FCSTD DOCUMENT  (FreeCAD 1.0R39319 (Git))
Label: Robot 2026 Aichi
License: All rights reserved
LicenseURL: https://en.wikipedia.org/wiki/All_rights_reserved
objects: Part::Feature×493, Part::Box×130, Part::Cylinder×120, Part::MultiFuse×91, Part::Cut×91, App::Part×63, Part::Fillet×11, Part::Chamfer×9, Part::FeaturePython×6, Part::Fuse×2, Part::Part2DObjectPython×2, Part::Extrusion×2, Part::MultiCommon×1, App::FeaturePython×1
note: 958 computed .brp shape members not serialized (recipe doc carries the construction recipe); baked Part::Feature solids carry a one-line shape summary decoded from their .brp

FEATURE [Part::Feature] Part__Feature  label="Tyre Axle LB"
  Placement = pos=(-4,-10,0) rot=(0,0,1;0rad)
  shape: bbox 40.5 x 10 x 10 mm, 8 faces (baked)
FEATURE [Part::Feature] Part__Feature001  label="Bearing LB"
  Placement = pos=(143,0,0) rot=(0,0,1;0rad)
  shape: bbox 4 x 15.6 x 15.6 mm, 6 faces (baked)
FEATURE [Part::Feature] Part__Feature002  label="Gear Axle LB"
  Placement = pos=(-4,-10,0) rot=(0,0,1;0rad)
  shape: bbox 21 x 30 x 30 mm, 121 faces (baked)
FEATURE [Part::Feature] Part__Feature003  label="Gear Motor LB"
  shape: bbox 4 x 26.99 x 26.94 mm, 202 faces (baked)
FEATURE [Part::Feature] Part__Feature004  label="Wheel LB"
  Placement = pos=(42.6,52,10) rot=(0,1,0;1.5708rad)
  shape: bbox 17 x 61.05 x 60.97 mm, 273 faces (baked)
FEATURE [Part::Feature] Part__Feature005  label="Silicon Tires LB"
  Placement = pos=(42.6,53,10) rot=(0,1,0;1.5708rad)
  shape: bbox 15 x 67.95 x 67.92 mm, 56 faces (baked)
FEATURE [App::Part] robot___robcup_ber_5__a  label="Drivetrain LB"
  Group = -> [Part__Feature,Part__Feature001,Part__Feature002,Part__Feature003,Part__Feature004,Part__Feature005]
  Origin = -> Origin
FEATURE [Part::Feature] Part__Feature006  label="Gear Motor LF"
  Placement = pos=(0,-74,0) rot=(0,0,1;0rad)
  shape: bbox 4 x 26.99 x 26.94 mm, 202 faces (baked)
FEATURE [Part::Feature] Part__Feature007  label="Tyre Axle LF001"
  Placement = pos=(-4,10,0) rot=(0,0,1;0rad)
  shape: bbox 40.5 x 10 x 10 mm, 8 faces (baked)
FEATURE [Part::Feature] Part__Feature008  label="Bearing LF"
  Placement = pos=(143,-124,0) rot=(0,0,1;0rad)
  shape: bbox 4 x 15.6 x 15.6 mm, 6 faces (baked)
FEATURE [Part::Feature] Part__Feature009  label="Gear Axle LF"
  Placement = pos=(-4,10,0) rot=(0,0,1;0rad)
  shape: bbox 21 x 30 x 30 mm, 121 faces (baked)
FEATURE [Part::Feature] Part__Feature010  label="Wheel LF"
  Placement = pos=(42.6,-72,10) rot=(0,1,0;1.5708rad)
  shape: bbox 17 x 61.05 x 60.97 mm, 273 faces (baked)
FEATURE [Part::Feature] Part__Feature011  label="Silicon Tires LF"
  Placement = pos=(42.6,-71,10) rot=(0,1,0;1.5708rad)
  shape: bbox 15 x 67.95 x 67.92 mm, 56 faces (baked)
FEATURE [App::Part] robot___robcup_ber_5__a001  label="Drivetrain LF"
  Group = -> [Part__Feature006,Part__Feature007,Part__Feature008,Part__Feature009,Part__Feature010,Part__Feature011]
  Origin = -> Origin001
FEATURE [Part::Feature] Part__Feature012  label="Tyre Axle RB"
  Placement = pos=(4,-10,0) rot=(0,0,1;0rad)
  shape: bbox 40.5 x 10 x 10 mm, 8 faces (baked)
FEATURE [Part::Feature] Part__Feature013  label="Gear Motor RB"
  Placement = pos=(-143,0,0) rot=(0,0,1;0rad)
  shape: bbox 4 x 26.99 x 26.94 mm, 202 faces (baked)
FEATURE [Part::Feature] Part__Feature014  label="Bearing RB"
  shape: bbox 4 x 15.6 x 15.6 mm, 6 faces (baked)
FEATURE [Part::Feature] Part__Feature015  label="Gear Axle RB"
  Placement = pos=(4,-10,0) rot=(0,0,1;0rad)
  shape: bbox 21 x 30 x 30 mm, 121 faces (baked)
FEATURE [Part::Feature] Part__Feature016  label="Wheel RB"
  Placement = pos=(-127.4,52,10) rot=(0,1,0;1.5708rad)
  shape: bbox 17 x 61.05 x 60.97 mm, 273 faces (baked)
FEATURE [Part::Feature] Part__Feature017  label="Silicon Tires RB"
  Placement = pos=(-127.4,53,10) rot=(0,1,0;1.5708rad)
  shape: bbox 15 x 67.95 x 67.92 mm, 56 faces (baked)
FEATURE [App::Part] robot___robcup_ber_5__a002  label="Drivetrain RB"
  Group = -> [Part__Feature012,Part__Feature013,Part__Feature014,Part__Feature015,Part__Feature016,Part__Feature017]
  Origin = -> Origin002
FEATURE [Part::Feature] Part__Feature018  label="Gear Motor RF"
  Placement = pos=(-143,-74,0) rot=(0,0,1;0rad)
  shape: bbox 4 x 26.99 x 26.94 mm, 202 faces (baked)
FEATURE [Part::Feature] Part__Feature019  label="Gear Axle RF"
  Placement = pos=(4,10,0) rot=(0,0,1;0rad)
  shape: bbox 21 x 30 x 30 mm, 121 faces (baked)
FEATURE [Part::Feature] Part__Feature020  label="Bearing RF"
  Placement = pos=(0,-124,0) rot=(0,0,1;0rad)
  shape: bbox 4 x 15.6 x 15.6 mm, 6 faces (baked)
FEATURE [Part::Feature] Part__Feature021  label="Tyre Axle RF"
  Placement = pos=(4,10,0) rot=(0,0,1;0rad)
  shape: bbox 40.5 x 10 x 10 mm, 8 faces (baked)
FEATURE [Part::Feature] Part__Feature022  label="Wheel RF"
  Placement = pos=(-127.4,-72,10) rot=(0,1,0;1.5708rad)
  shape: bbox 17 x 61.05 x 60.97 mm, 273 faces (baked)
FEATURE [Part::Feature] Part__Feature023  label="Silicon Tires RF"
  Placement = pos=(-127.4,-71,10) rot=(0,1,0;1.5708rad)
  shape: bbox 15 x 67.95 x 67.92 mm, 56 faces (baked)
FEATURE [App::Part] robot___robcup_ber_5__a003  label="Drivetrain RF"
  Group = -> [Part__Feature018,Part__Feature019,Part__Feature020,Part__Feature021,Part__Feature022,Part__Feature023]
  Origin = -> Origin003
FEATURE [Part::Box] Box069  label="立方体048"
  AttacherType = Attacher::AttachEngine3D
  Height = 20.1
  Length = 38.8
  Placement = pos=(82,-93,0) rot=(0,0,1;0rad)
  Width = 40.1
FEATURE [Part::Box] Box084  label="立方体063"
  AttacherType = Attacher::AttachEngine3D
  Height = 20.1
  Length = 2.7
  Placement = pos=(90.8,-99.95,0) rot=(0,0,1;0rad)
  Width = 54
FEATURE [Part::FeaturePython] CycloidGear025  # WARN: FeaturePython — macro-defined, semantics opaque (R4)
  AttacherType = Attacher::AttachEngine3D
  Placement = pos=(-107.4,-47,10) rot=(0,1,0;1.5708rad)
  angular_backlash = 0
  backlash = 0
  clearance = 0.25
  double_helix = false
  head = 0
  head_fillet = 0
  height = 6
  helix_angle = 0
  inner_diameter = 12.5
  module = 0.24
  num_teeth = 25
  numpoints = 20
  outer_diameter = 7.5
  pitch_diameter = 6
  root_fillet = 0
  version = 1.3.0
  expr: angular_backlash = backlash / pitch_diameter * 360 ° / pi
  expr: inner_diameter = num_teeth / 2
  expr: pitch_diameter = num_teeth * module
FEATURE [Part::Cylinder] Cylinder175  label="円柱175"
  Angle = 360
  AttacherType = Attacher::AttachEngine3D
  FirstAngle = 0
  Height = 20
  Placement = pos=(-97.2,-22.1,5) rot=(0,1,0;1.5708rad)
  Radius = 2
  SecondAngle = 0
FEATURE [Part::Cylinder] Cylinder176  label="円柱176"
  Angle = 360
  AttacherType = Attacher::AttachEngine3D
  FirstAngle = 0
  Height = 20
  Placement = pos=(-97.2,-22.1,15) rot=(0,1,0;1.5708rad)
  Radius = 2
  SecondAngle = 0
FEATURE [Part::Cylinder] Cylinder177  label="円柱177"
  Angle = 360
  AttacherType = Attacher::AttachEngine3D
  FirstAngle = 0
  Height = 20
  Placement = pos=(-97.2,-71.8,15) rot=(0,1,0;1.5708rad)
  Radius = 2
  SecondAngle = 0
FEATURE [Part::Cylinder] Cylinder178  label="円柱178"
  Angle = 360
  AttacherType = Attacher::AttachEngine3D
  FirstAngle = 0
  Height = 20
  Placement = pos=(-97.2,-71.8,5) rot=(0,1,0;1.5708rad)
  Radius = 2
  SecondAngle = 0
FEATURE [Part::MultiFuse] Fusion084
  Placement = pos=(-188,26,0) rot=(0,0,1;0rad)
  Shapes = -> [Box084,Box069]
FEATURE [Part::Cut] Cut128
  Base = -> Fusion084
  Tool = -> Cylinder176
FEATURE [Part::Cut] Cut129
  Base = -> Cut128
  Tool = -> Cylinder175
FEATURE [Part::Cut] Cut130
  Base = -> Cut129
  Tool = -> Cylinder177
FEATURE [Part::Cut] Cut131
  Base = -> Cut130
  Placement = pos=(4,10,0) rot=(0,0,1;0rad)
  Tool = -> Cylinder178
FEATURE [Part::MultiFuse] Fusion344  label="Motor RF"
  Refine = true
  Shapes = -> [Cut131,CycloidGear025]
FEATURE [Part::Box] Box075  label="立方体054"
  AttacherType = Attacher::AttachEngine3D
  Height = 20.1
  Length = 38.8
  Placement = pos=(82,-93,0) rot=(0,0,1;0rad)
  Width = 40.1
FEATURE [Part::Box] Box223  label="立方体201"
  AttacherType = Attacher::AttachEngine3D
  Height = 20.1
  Length = 2.7
  Placement = pos=(90.8,-99.95,0) rot=(0,0,1;0rad)
  Width = 54
FEATURE [Part::FeaturePython] CycloidGear019  # WARN: FeaturePython — macro-defined, semantics opaque (R4)
  AttacherType = Attacher::AttachEngine3D
  Placement = pos=(-107.4,27,10) rot=(0,1,0;1.5708rad)
  angular_backlash = 0
  backlash = 0
  clearance = 0.25
  double_helix = false
  head = 0
  head_fillet = 0
  height = 6
  helix_angle = 0
  inner_diameter = 12.5
  module = 0.24
  num_teeth = 25
  numpoints = 20
  outer_diameter = 7.5
  pitch_diameter = 6
  root_fillet = 0
  version = 1.3.0
  expr: angular_backlash = backlash / pitch_diameter * 360 ° / pi
  expr: inner_diameter = num_teeth / 2
  expr: pitch_diameter = num_teeth * module
FEATURE [Part::Cylinder] Cylinder171  label="円柱171"
  Angle = 360
  AttacherType = Attacher::AttachEngine3D
  FirstAngle = 0
  Height = 20
  Placement = pos=(-97.2,51.9,5) rot=(0,1,0;1.5708rad)
  Radius = 2
  SecondAngle = 0
FEATURE [Part::Cylinder] Cylinder172  label="円柱172"
  Angle = 360
  AttacherType = Attacher::AttachEngine3D
  FirstAngle = 0
  Height = 20
  Placement = pos=(-97.2,51.9,15) rot=(0,1,0;1.5708rad)
  Radius = 2
  SecondAngle = 0
FEATURE [Part::Cylinder] Cylinder173  label="円柱173"
  Angle = 360
  AttacherType = Attacher::AttachEngine3D
  FirstAngle = 0
  Height = 20
  Placement = pos=(-97.2,2.2,15) rot=(0,1,0;1.5708rad)
  Radius = 2
  SecondAngle = 0
FEATURE [Part::Cylinder] Cylinder174  label="円柱174"
  Angle = 360
  AttacherType = Attacher::AttachEngine3D
  FirstAngle = 0
  Height = 20
  Placement = pos=(-97.2,2.2,5) rot=(0,1,0;1.5708rad)
  Radius = 2
  SecondAngle = 0
FEATURE [Part::MultiFuse] Fusion085
  Placement = pos=(-188,100,0) rot=(0,0,1;0rad)
  Shapes = -> [Box223,Box075]
FEATURE [Part::Cut] Cut124
  Base = -> Fusion085
  Tool = -> Cylinder172
FEATURE [Part::Cut] Cut125
  Base = -> Cut124
  Tool = -> Cylinder171
FEATURE [Part::Cut] Cut126
  Base = -> Cut125
  Tool = -> Cylinder173
FEATURE [Part::Cut] Cut127
  Base = -> Cut126
  Placement = pos=(4,-10,0) rot=(0,0,1;0rad)
  Tool = -> Cylinder174
FEATURE [Part::MultiFuse] Fusion345  label="Motor RB"
  Refine = true
  Shapes = -> [CycloidGear019,Cut127]
FEATURE [Part::Box] Box225  label="立方体203"
  AttacherType = Attacher::AttachEngine3D
  Height = 20.1
  Length = 2.7
  Placement = pos=(109.3,-99.95,0) rot=(0,0,1;0rad)
  Width = 54
FEATURE [Part::Box] Box226  label="立方体204"
  AttacherType = Attacher::AttachEngine3D
  Height = 20.1
  Length = 38.8
  Placement = pos=(82,-93,0) rot=(0,0,1;0rad)
  Width = 40.1
FEATURE [Part::FeaturePython] CycloidGear022  # WARN: FeaturePython — macro-defined, semantics opaque (R4)
  AttacherType = Attacher::AttachEngine3D
  Placement = pos=(33.6,-47,10) rot=(0,1,0;1.5708rad)
  angular_backlash = 0
  backlash = 0
  clearance = 0.25
  double_helix = false
  head = 0
  head_fillet = 0
  height = 6
  helix_angle = 0
  inner_diameter = 12.5
  module = 0.24
  num_teeth = 25
  numpoints = 20
  outer_diameter = 7.5
  pitch_diameter = 6
  root_fillet = 0
  version = 1.3.0
  expr: angular_backlash = backlash / pitch_diameter * 360 ° / pi
  expr: inner_diameter = num_teeth / 2
  expr: pitch_diameter = num_teeth * module
FEATURE [Part::Cylinder] Cylinder167  label="円柱167"
  Angle = 360
  AttacherType = Attacher::AttachEngine3D
  FirstAngle = 0
  Height = 20
  Placement = pos=(9.4,-22.1,5) rot=(0,1,0;1.5708rad)
  Radius = 2
  SecondAngle = 0
FEATURE [Part::Cylinder] Cylinder168  label="円柱168"
  Angle = 360
  AttacherType = Attacher::AttachEngine3D
  FirstAngle = 0
  Height = 20
  Placement = pos=(9.4,-22.1,15) rot=(0,1,0;1.5708rad)
  Radius = 2
  SecondAngle = 0
FEATURE [Part::Cylinder] Cylinder169  label="円柱169"
  Angle = 360
  AttacherType = Attacher::AttachEngine3D
  FirstAngle = 0
  Height = 20
  Placement = pos=(9.4,-71.8,15) rot=(0,1,0;1.5708rad)
  Radius = 2
  SecondAngle = 0
FEATURE [Part::Cylinder] Cylinder170  label="円柱170"
  Angle = 360
  AttacherType = Attacher::AttachEngine3D
  FirstAngle = 0
  Height = 20
  Placement = pos=(9.4,-71.8,5) rot=(0,1,0;1.5708rad)
  Radius = 2
  SecondAngle = 0
FEATURE [Part::MultiFuse] Fusion086
  Placement = pos=(-82.6,26,0) rot=(0,0,1;0rad)
  Shapes = -> [Box226,Box225]
FEATURE [Part::Cut] Cut120
  Base = -> Fusion086
  Tool = -> Cylinder168
FEATURE [Part::Cut] Cut121
  Base = -> Cut120
  Tool = -> Cylinder167
FEATURE [Part::Cut] Cut122
  Base = -> Cut121
  Tool = -> Cylinder169
FEATURE [Part::Cut] Cut123
  Base = -> Cut122
  Placement = pos=(-4,10,0) rot=(0,0,1;0rad)
  Tool = -> Cylinder170
FEATURE [Part::MultiFuse] Fusion347  label="Motor LF"
  Refine = true
  Shapes = -> [Cut123,CycloidGear022]
FEATURE [Part::Box] Box076  label="立方体055"
  AttacherType = Attacher::AttachEngine3D
  Height = 20.1
  Length = 2.7
  Placement = pos=(109.3,-99.95,0) rot=(0,0,1;0rad)
  Width = 54
FEATURE [Part::Box] Box227  label="立方体205"
  AttacherType = Attacher::AttachEngine3D
  Height = 20.1
  Length = 38.8
  Placement = pos=(82,-93,0) rot=(0,0,1;0rad)
  Width = 40.1
FEATURE [Part::FeaturePython] CycloidGear017  # WARN: FeaturePython — macro-defined, semantics opaque (R4)
  AttacherType = Attacher::AttachEngine3D
  Placement = pos=(33.6,27,10) rot=(0,1,0;1.5708rad)
  angular_backlash = 0
  backlash = 0
  clearance = 0.25
  double_helix = false
  head = 0
  head_fillet = 0
  height = 6
  helix_angle = 0
  inner_diameter = 12.5
  module = 0.24
  num_teeth = 25
  numpoints = 20
  outer_diameter = 7.5
  pitch_diameter = 6
  root_fillet = 0
  version = 1.3.0
  expr: angular_backlash = backlash / pitch_diameter * 360 ° / pi
  expr: inner_diameter = num_teeth / 2
  expr: pitch_diameter = num_teeth * module
FEATURE [Part::Cylinder] Cylinder163  label="円柱163"
  Angle = 360
  AttacherType = Attacher::AttachEngine3D
  FirstAngle = 0
  Height = 20
  Placement = pos=(9.4,51.9,5) rot=(0,1,0;1.5708rad)
  Radius = 2
  SecondAngle = 0
FEATURE [Part::Cylinder] Cylinder164  label="円柱164"
  Angle = 360
  AttacherType = Attacher::AttachEngine3D
  FirstAngle = 0
  Height = 20
  Placement = pos=(9.4,51.9,15) rot=(0,1,0;1.5708rad)
  Radius = 2
  SecondAngle = 0
FEATURE [Part::Cylinder] Cylinder165  label="円柱165"
  Angle = 360
  AttacherType = Attacher::AttachEngine3D
  FirstAngle = 0
  Height = 20
  Placement = pos=(9.4,2.2,15) rot=(0,1,0;1.5708rad)
  Radius = 2
  SecondAngle = 0
FEATURE [Part::Cylinder] Cylinder166  label="円柱166"
  Angle = 360
  AttacherType = Attacher::AttachEngine3D
  FirstAngle = 0
  Height = 20
  Placement = pos=(9.4,2.2,5) rot=(0,1,0;1.5708rad)
  Radius = 2
  SecondAngle = 0
FEATURE [Part::MultiFuse] Fusion087
  Placement = pos=(-82.6,100,0) rot=(0,0,1;0rad)
  Shapes = -> [Box076,Box227]
FEATURE [Part::Cut] Cut116
  Base = -> Fusion087
  Tool = -> Cylinder164
FEATURE [Part::Cut] Cut117
  Base = -> Cut116
  Tool = -> Cylinder163
FEATURE [Part::Cut] Cut118
  Base = -> Cut117
  Tool = -> Cylinder165
FEATURE [Part::Cut] Cut119
  Base = -> Cut118
  Placement = pos=(-4,-10,0) rot=(0,0,1;0rad)
  Tool = -> Cylinder166
FEATURE [Part::MultiFuse] Fusion346  label="Motor LB"
  Refine = true
  Shapes = -> [CycloidGear017,Cut119]
FEATURE [Part::Box] Box016  label="機体底面"
  AttacherType = Attacher::AttachEngine3D
  Height = 5
  Length = 136.2
  Placement = pos=(-102,-108,-5) rot=(0,0,1;0rad)
  Width = 184
FEATURE [Part::Box] Box027  label="立方体007"
  AttacherType = Attacher::AttachEngine3D
  Height = 20.4
  Length = 45.2
  Placement = pos=(-48.6,-98,10) rot=(0,0,1;0rad)
  Width = 5
FEATURE [Part::Box] Box102  label="立方体081"
  AttacherType = Attacher::AttachEngine3D
  Height = 5
  Length = 60
  Placement = pos=(-63.9,-96,-5) rot=(0,0,1;0rad)
  Width = 64
FEATURE [Part::Box] Box213  label="立方体191"
  AttacherType = Attacher::AttachEngine3D
  Height = 12
  Length = 3
  Placement = pos=(-65.9,-16.9,0) rot=(0,0,1;0rad)
  Width = 13.9
FEATURE [Part::Box] Box214  label="立方体192"
  AttacherType = Attacher::AttachEngine3D
  Height = 12
  Length = 3
  Placement = pos=(-4.9,-16.9,0) rot=(0,0,1;0rad)
  Width = 13.9
FEATURE [Part::Box] Box229  label="立方体208"
  AttacherType = Attacher::AttachEngine3D
  Height = 20
  Length = 10
  Placement = pos=(16.7,47.1,0) rot=(0,0,1;0rad)
  Width = 7
FEATURE [Part::Box] Box235  label="立方体214"
  AttacherType = Attacher::AttachEngine3D
  Height = 12
  Length = 58.6
  Placement = pos=(-63.2,-30,0) rot=(0,0,1;0rad)
  Width = 3
FEATURE [Part::Box] Box242  label="立方体220"
  AttacherType = Attacher::AttachEngine3D
  Height = 20
  Length = 21.5
  Placement = pos=(16,57.1,0) rot=(0,0,1;0rad)
  Width = 13
FEATURE [Part::Box] Box254  label="立方体229"
  AttacherType = Attacher::AttachEngine3D
  Height = 22
  Length = 54
  Placement = pos=(-60.9,-108,-3) rot=(0,0,1;0rad)
  Width = 12
FEATURE [Part::Box] Box302  label="立方体274"
  AttacherType = Attacher::AttachEngine3D
  Height = 20
  Length = 21.5
  Placement = pos=(-106,-90,0) rot=(0,0,1;0rad)
  Width = 13
FEATURE [Part::Box] Box307  label="立方体279"
  AttacherType = Attacher::AttachEngine3D
  Height = 20
  Length = 21.5
  Placement = pos=(16.7,-90,0) rot=(0,0,1;0rad)
  Width = 13
FEATURE [Part::Box] Box312  label="立方体284"
  AttacherType = Attacher::AttachEngine3D
  Height = 20
  Length = 21.5
  Placement = pos=(-106,57.1,0) rot=(0,0,1;0rad)
  Width = 13
FEATURE [Part::Box] Box315  label="立方体287"
  AttacherType = Attacher::AttachEngine3D
  Height = 20
  Length = 12.7
  Placement = pos=(16.7,54.1,0) rot=(0,0,1;0rad)
  Width = 3
FEATURE [Part::Box] Box344  label="立方体316"
  AttacherType = Attacher::AttachEngine3D
  Height = 20
  Length = 10
  Placement = pos=(16.7,-74,0) rot=(0,0,1;0rad)
  Width = 7
FEATURE [Part::Box] Box345  label="立方体317"
  AttacherType = Attacher::AttachEngine3D
  Height = 20
  Length = 10
  Placement = pos=(-94.5,47.1,0) rot=(0,0,1;0rad)
  Width = 7
FEATURE [Part::Box] Box346  label="立方体318"
  AttacherType = Attacher::AttachEngine3D
  Height = 20
  Length = 10
  Placement = pos=(-94.5,-74,0) rot=(0,0,1;0rad)
  Width = 7
FEATURE [Part::Box] Box347  label="立方体319"
  AttacherType = Attacher::AttachEngine3D
  Height = 20
  Length = 12.7
  Placement = pos=(16.7,-77,0) rot=(0,0,1;0rad)
  Width = 3
FEATURE [Part::Box] Box348  label="立方体320"
  AttacherType = Attacher::AttachEngine3D
  Height = 20
  Length = 12.7
  Placement = pos=(-97.2,54.1,0) rot=(0,0,1;0rad)
  Width = 3
FEATURE [Part::Box] Box349  label="立方体321"
  AttacherType = Attacher::AttachEngine3D
  Height = 20
  Length = 12.7
  Placement = pos=(-97.2,-77,0) rot=(0,0,1;0rad)
  Width = 3
FEATURE [Part::Box] Box351  label="立方体323"
  AttacherType = Attacher::AttachEngine3D
  Height = 20.1
  Length = 12
  Placement = pos=(10.7,-16.9,0) rot=(0,0,1;0rad)
  Width = 13.9
FEATURE [Part::Box] Box358  label="立方体330"
  AttacherType = Attacher::AttachEngine3D
  Height = 27
  Length = 3
  Placement = pos=(-4.9,-14.9,0) rot=(0,0,1;0rad)
  Width = 10
FEATURE [Part::Box] Box360  label="立方体331"
  AttacherType = Attacher::AttachEngine3D
  Height = 27
  Length = 3
  Placement = pos=(-65.9,-14.9,0) rot=(0,0,1;0rad)
  Width = 10
FEATURE [Part::Box] Box361  label="立方体332"
  AttacherType = Attacher::AttachEngine3D
  Height = 2
  Length = 64
  Placement = pos=(-65.9,-14.9,27) rot=(0,0,1;0rad)
  Width = 10
FEATURE [Part::Box] Box362  label="立方体333"
  AttacherType = Attacher::AttachEngine3D
  Height = 20.1
  Length = 8.8
  Placement = pos=(25.4,-16.9,0) rot=(0,0,1;0rad)
  Width = 13.9
FEATURE [Part::Box] Box363  label="立方体334"
  AttacherType = Attacher::AttachEngine3D
  Height = 20.1
  Length = 12
  Placement = pos=(-90.5,-16.9,0) rot=(0,0,1;0rad)
  Width = 13.9
FEATURE [Part::Box] Box364  label="立方体335"
  AttacherType = Attacher::AttachEngine3D
  Height = 20.1
  Length = 8.8
  Placement = pos=(-102,-16.9,0) rot=(0,0,1;0rad)
  Width = 13.9
FEATURE [Part::Box] Box388  label="立方体358"
  AttacherType = Attacher::AttachEngine3D
  Height = 32
  Length = 6
  Placement = pos=(-66.9,-96,0) rot=(0,0,1;0rad)
  Width = 16
FEATURE [Part::Box] Box390  label="立方体360"
  AttacherType = Attacher::AttachEngine3D
  Height = 32
  Length = 6
  Placement = pos=(-6.9,-96,0) rot=(0,0,1;0rad)
  Width = 16
FEATURE [Part::Box] Box391  label="立方体361"
  AttacherType = Attacher::AttachEngine3D
  Height = 32
  Length = 60
  Placement = pos=(-63.9,-93,0) rot=(0,0,1;0rad)
  Width = 13
FEATURE [Part::Box] Box401  label="立方体371"
  AttacherType = Attacher::AttachEngine3D
  Height = 12
  Length = 3
  Placement = pos=(-65.9,-16.9,0) rot=(0,0,1;0rad)
  Width = 10
FEATURE [Part::Box] Box402  label="立方体372"
  AttacherType = Attacher::AttachEngine3D
  Height = 12
  Length = 3
  Placement = pos=(-4.9,-16.9,0) rot=(0,0,1;0rad)
  Width = 10
FEATURE [Part::Cylinder] Cylinder004  label="円柱004"
  Angle = 360
  AttacherType = Attacher::AttachEngine3D
  FirstAngle = 0
  Height = 15
  Placement = pos=(-13,-93,20.2) rot=(1,0,0;1.5708rad)
  Radius = 8
  SecondAngle = 0
FEATURE [Part::Cylinder] Cylinder005  label="円柱005"
  Angle = 360
  AttacherType = Attacher::AttachEngine3D
  FirstAngle = 0
  Height = 15
  Placement = pos=(-39,-93,20.2) rot=(1,0,0;1.5708rad)
  Radius = 8
  SecondAngle = 0
FEATURE [Part::Cylinder] Cylinder137  label="円柱137"
  Angle = 360
  AttacherType = Attacher::AttachEngine3D
  FirstAngle = 0
  Height = 47.8
  Placement = pos=(9.4,62,10) rot=(0,1,0;1.5708rad)
  Radius = 4
  SecondAngle = 0
FEATURE [Part::Cut] Cut093
  Base = -> Box242
  Placement = pos=(-3.3,-10,0) rot=(0,0,1;0rad)
  Tool = -> Cylinder137
FEATURE [Part::Cylinder] Cylinder139  label="円柱139"
  Angle = 360
  AttacherType = Attacher::AttachEngine3D
  FirstAngle = 0
  Height = 47.8
  Placement = pos=(-125,62,10) rot=(0,1,0;1.5708rad)
  Radius = 4
  SecondAngle = 0
FEATURE [Part::Cut] Cut245
  Base = -> Box312
  Placement = pos=(4,-10,0) rot=(0,0,1;0rad)
  Tool = -> Cylinder139
FEATURE [Part::Cylinder] Cylinder140  label="円柱140"
  Angle = 360
  AttacherType = Attacher::AttachEngine3D
  FirstAngle = 0
  Height = 47.8
  Placement = pos=(9.4,-82,10) rot=(0,1,0;1.5708rad)
  Radius = 4
  SecondAngle = 0
FEATURE [Part::Cut] Cut247
  Base = -> Box307
  Placement = pos=(-4,10,0) rot=(0,0,1;0rad)
  Tool = -> Cylinder140
FEATURE [Part::Cylinder] Cylinder146  label="円柱146"
  Angle = 360
  AttacherType = Attacher::AttachEngine3D
  FirstAngle = 0
  Height = 47.8
  Placement = pos=(-125,-82,10) rot=(0,1,0;1.5708rad)
  Radius = 4
  SecondAngle = 0
FEATURE [Part::Cut] Cut246
  Base = -> Box302
  Placement = pos=(4,10,0) rot=(0,0,1;0rad)
  Tool = -> Cylinder146
FEATURE [Part::Cylinder] Cylinder147  label="円柱147"
  Angle = 360
  AttacherType = Attacher::AttachEngine3D
  FirstAngle = 0
  Height = 20
  Placement = pos=(9.4,51.9,5) rot=(0,1,0;1.5708rad)
  Radius = 2
  SecondAngle = 0
FEATURE [Part::Cylinder] Cylinder148  label="円柱148"
  Angle = 360
  AttacherType = Attacher::AttachEngine3D
  FirstAngle = 0
  Height = 20
  Placement = pos=(9.4,51.9,15) rot=(0,1,0;1.5708rad)
  Radius = 2
  SecondAngle = 0
FEATURE [Part::Cylinder] Cylinder153  label="円柱153"
  Angle = 360
  AttacherType = Attacher::AttachEngine3D
  FirstAngle = 0
  Height = 20
  Placement = pos=(9.4,-71.8,15) rot=(0,1,0;1.5708rad)
  Radius = 2
  SecondAngle = 0
FEATURE [Part::Cylinder] Cylinder154  label="円柱154"
  Angle = 360
  AttacherType = Attacher::AttachEngine3D
  FirstAngle = 0
  Height = 20
  Placement = pos=(9.4,-71.8,5) rot=(0,1,0;1.5708rad)
  Radius = 2
  SecondAngle = 0
FEATURE [Part::Cylinder] Cylinder155  label="円柱155"
  Angle = 360
  AttacherType = Attacher::AttachEngine3D
  FirstAngle = 0
  Height = 20
  Placement = pos=(-97.2,51.9,5) rot=(0,1,0;1.5708rad)
  Radius = 2
  SecondAngle = 0
FEATURE [Part::Cylinder] Cylinder156  label="円柱156"
  Angle = 360
  AttacherType = Attacher::AttachEngine3D
  FirstAngle = 0
  Height = 20
  Placement = pos=(-97.2,51.9,15) rot=(0,1,0;1.5708rad)
  Radius = 2
  SecondAngle = 0
FEATURE [Part::Cylinder] Cylinder161  label="円柱161"
  Angle = 360
  AttacherType = Attacher::AttachEngine3D
  FirstAngle = 0
  Height = 20
  Placement = pos=(-97.2,-71.8,15) rot=(0,1,0;1.5708rad)
  Radius = 2
  SecondAngle = 0
FEATURE [Part::Cylinder] Cylinder162  label="円柱162"
  Angle = 360
  AttacherType = Attacher::AttachEngine3D
  FirstAngle = 0
  Height = 20
  Placement = pos=(-97.2,-71.8,5) rot=(0,1,0;1.5708rad)
  Radius = 2
  SecondAngle = 0
FEATURE [Part::Cylinder] Cylinder212  label="円柱212"
  Angle = 360
  AttacherType = Attacher::AttachEngine3D
  FirstAngle = 0
  Height = 47
  Placement = pos=(7,-98,-5) rot=(0,0,1;0rad)
  Radius = 2
  SecondAngle = 0
FEATURE [Part::Cylinder] Cylinder227  label="円柱227"
  Angle = 360
  AttacherType = Attacher::AttachEngine3D
  FirstAngle = 0
  Height = 42
  Placement = pos=(-81.9,72,-5) rot=(0,0,1;0rad)
  Radius = 2
  SecondAngle = 0
FEATURE [Part::Cylinder] Cylinder229  label="円柱229"
  Angle = 360
  AttacherType = Attacher::AttachEngine3D
  FirstAngle = 0
  Height = 42
  Placement = pos=(14.1,72,-5) rot=(0,0,1;0rad)
  Radius = 2
  SecondAngle = 0
FEATURE [Part::Cylinder] Cylinder279  label="円柱279"
  Angle = 360
  AttacherType = Attacher::AttachEngine3D
  FirstAngle = 0
  Height = 5
  Placement = pos=(30.2,-10,15.1) rot=(0,0,1;0rad)
  Radius = 4
  SecondAngle = 0
FEATURE [Part::Cut] Cut262
  Base = -> Box362
  Tool = -> Cylinder279
FEATURE [Part::Cylinder] Cylinder280  label="円柱280"
  Angle = 360
  AttacherType = Attacher::AttachEngine3D
  FirstAngle = 0
  Height = 25.1
  Placement = pos=(17.2,-10,-5) rot=(0,0,1;0rad)
  Radius = 2
  SecondAngle = 0
FEATURE [Part::Cut] Cut261
  Base = -> Box351
  Tool = -> Cylinder280
FEATURE [Part::Cylinder] Cylinder283  label="円柱283"
  Angle = 360
  AttacherType = Attacher::AttachEngine3D
  FirstAngle = 0
  Height = 5
  Placement = pos=(17.2,-10,-5) rot=(0,0,1;0rad)
  Radius = 4
  SecondAngle = 0
FEATURE [Part::Cylinder] Cylinder287  label="円柱287"
  Angle = 360
  AttacherType = Attacher::AttachEngine3D
  FirstAngle = 0
  Height = 10
  Placement = pos=(-98,-10,15.1) rot=(0,0,1;0rad)
  Radius = 4
  SecondAngle = 0
FEATURE [Part::Cut] Cut263
  Base = -> Box364
  Tool = -> Cylinder287
FEATURE [Part::Cylinder] Cylinder288  label="円柱288"
  Angle = 360
  AttacherType = Attacher::AttachEngine3D
  FirstAngle = 0
  Height = 30.1
  Placement = pos=(-85,-10,-5) rot=(0,0,1;0rad)
  Radius = 2
  SecondAngle = 0
FEATURE [Part::Cut] Cut264
  Base = -> Box363
  Tool = -> Cylinder288
FEATURE [Part::Cylinder] Cylinder289  label="円柱289"
  Angle = 360
  AttacherType = Attacher::AttachEngine3D
  FirstAngle = 0
  Height = 5
  Placement = pos=(-85,-10,-5) rot=(0,0,1;0rad)
  Radius = 4
  SecondAngle = 0
FEATURE [Part::Cylinder] Cylinder304  label="円柱304"
  Angle = 360
  AttacherType = Attacher::AttachEngine3D
  FirstAngle = 0
  Height = 12
  Placement = pos=(1.4,70,0) rot=(0,0,1;0rad)
  Radius = 2
  SecondAngle = 0
FEATURE [Part::Cylinder] Cylinder305  label="円柱305"
  Angle = 360
  AttacherType = Attacher::AttachEngine3D
  FirstAngle = 0
  Height = 12
  Placement = pos=(-70.2,70,0) rot=(0,0,1;0rad)
  Radius = 2
  SecondAngle = 0
FEATURE [Part::Cylinder] Cylinder311  label="円柱311"
  Angle = 360
  AttacherType = Attacher::AttachEngine3D
  FirstAngle = 0
  Height = 47
  Placement = pos=(-75,-98,-5) rot=(0,0,1;0rad)
  Radius = 2
  SecondAngle = 0
FEATURE [Part::Fillet] Fillet
  Base = -> Box102
  EdgeLinks = -> Box102 [Edge1,Edge3,Edge5,Edge7]
  Edges = 4 edges r=2: [Edge1,Edge3,Edge5,Edge7]
FEATURE [Part::Cut] Cut334
  Base = -> Box016
  Refine = true
  Tool = -> Fillet
FEATURE [Part::Fillet] Fillet015
  Base = -> Box391
  EdgeLinks = -> Box391 [Edge1,Edge5]
  Edges = 2 edges r=2: [Edge1,Edge5]
FEATURE [Part::MultiFuse] Fusion040
  Placement = pos=(-7.9,-3,-13) rot=(0,0,1;0rad)
  Refine = true
  Shapes = -> [Box027,Cylinder004,Cylinder005]
FEATURE [Part::MultiFuse] Fusion184
  Shapes = -> [Box344,Box347]
FEATURE [Part::Cut] Cut229
  Base = -> Fusion184
  Tool = -> Cylinder153
FEATURE [Part::Cut] Cut230
  Base = -> Cut229
  Placement = pos=(-4,10,0) rot=(0,0,1;0rad)
  Tool = -> Cylinder154
FEATURE [Part::MultiFuse] Fusion187
  Shapes = -> [Box315,Box229]
FEATURE [Part::Cut] Cut235
  Base = -> Fusion187
  Tool = -> Cylinder148
FEATURE [Part::Cut] Cut236
  Base = -> Cut235
  Placement = pos=(-4,-10,0) rot=(0,0,1;0rad)
  Tool = -> Cylinder147
FEATURE [Part::MultiFuse] Fusion188
  Shapes = -> [Box349,Box346]
FEATURE [Part::Cut] Cut237
  Base = -> Fusion188
  Tool = -> Cylinder161
FEATURE [Part::Cut] Cut238
  Base = -> Cut237
  Placement = pos=(4,10,0) rot=(0,0,1;0rad)
  Tool = -> Cylinder162
FEATURE [Part::MultiFuse] Fusion191
  Shapes = -> [Box348,Box345]
FEATURE [Part::Cut] Cut243
  Base = -> Fusion191
  Tool = -> Cylinder156
FEATURE [Part::Cut] Cut244
  Base = -> Cut243
  Placement = pos=(4,-10,0) rot=(0,0,1;0rad)
  Tool = -> Cylinder155
FEATURE [Part::MultiFuse] Fusion216
  Shapes = -> [Cylinder289,Cylinder283]
FEATURE [Part::MultiFuse] Fusion234
  Shapes = -> [Box360,Box361,Box358]
FEATURE [Part::MultiFuse] Fusion235
  Shapes = -> [Box213,Box214]
FEATURE [Part::MultiFuse] Fusion236
  Placement = pos=(0,54,0) rot=(0,0,1;0rad)
  Shapes = -> [Box401,Box402]
FEATURE [Part::MultiFuse] Fusion237
  Shapes = -> [Box235,Fusion234,Fusion235,Fusion236]
FEATURE [Part::MultiFuse] Fusion238
  Shapes = -> [Cut264,Cut261]
FEATURE [Part::MultiFuse] Fusion239
  Shapes = -> [Cut262,Cut263]
FEATURE [Part::MultiFuse] Fusion240
  Shapes = -> [Fusion238,Fusion239]
FEATURE [Part::MultiFuse] Fusion241
  Shapes = -> [Cut246,Cut247,Cut093,Cut245]
FEATURE [Part::MultiFuse] Fusion242
  Shapes = -> [Cut238,Cut244,Cut230,Cut236]
FEATURE [Part::MultiFuse] Fusion243
  Shapes = -> [Fusion240,Fusion241,Fusion242]
FEATURE [Part::MultiFuse] Fusion271
  Shapes = -> [Cylinder305,Cylinder304]
FEATURE [Part::MultiFuse] Fusion273
  Placement = pos=(0,-5,0) rot=(0,0,1;0rad)
  Shapes = -> [Cylinder227,Cylinder229]
FEATURE [Part::MultiFuse] Fusion307
  Refine = true
  Shapes = -> [Box390,Box388]
FEATURE [Part::Cut] Cut331
  Base = -> Fusion307
  Placement = pos=(0,-3,0) rot=(0,0,1;0rad)
  Refine = true
  Tool = -> Fillet015
FEATURE [Part::Chamfer] Chamfer
  Base = -> Cut331
  EdgeLinks = -> Cut331 [Edge8,Edge29]
  Edges = 2 edges r=10: [Edge8,Edge29]
FEATURE [Part::MultiFuse] Fusion311
  Refine = true
  Shapes = -> [Box254,Cut334]
FEATURE [Part::Cut] Cut335
  Base = -> Fusion311
  Refine = true
  Tool = -> Fusion040
FEATURE [Part::Chamfer] Chamfer036
  Base = -> Cut335
  EdgeLinks = -> Cut335 [Edge1,Edge8]
  Edges = 2 edges r=20: [Edge1,Edge8]
FEATURE [Part::Chamfer] Chamfer037
  Base = -> Chamfer036
  EdgeLinks = -> Chamfer036 [Edge3,Edge25]
  Edges = 2 edges r=15: [Edge3,Edge25]
FEATURE [Part::MultiFuse] Fusion313
  Refine = true
  Shapes = -> [Cylinder212,Cylinder311]
FEATURE [Part::MultiFuse] Fusion318
  Refine = true
  Shapes = -> [Fusion273,Fusion313]
FEATURE [Part::MultiFuse] Fusion320
  Refine = true
  Shapes = -> [Fusion243,Fusion237,Fusion271,Chamfer]
FEATURE [Part::MultiFuse] Fusion327
  Refine = true
  Shapes = -> [Fusion216,Fusion318]
FEATURE [Part::MultiFuse] Fusion333
  Refine = true
  Shapes = -> [Chamfer037,Fusion320]
FEATURE [Part::Cut] Cut340  label="Chassis 1"
  Base = -> Fusion333
  Refine = true
  Tool = -> Fusion327
FEATURE [Part::Box] Box  label="リポバッテリー"
  AttacherType = Attacher::AttachEngine3D
  Height = 17
  Length = 36
  Placement = pos=(-11,-17,37) rot=(0,0,1;0rad)
  Width = 80
FEATURE [Part::Box] Box100  label="立方体079"
  AttacherType = Attacher::AttachEngine3D
  Height = 25
  Length = 25
  Placement = pos=(-38.5,-94,16) rot=(0,0,1;0rad)
  Width = 1
FEATURE [Part::Box] Box101  label="立方体080"
  AttacherType = Attacher::AttachEngine3D
  Height = 25
  Length = 15
  Placement = pos=(-33.5,-101,16) rot=(0,0,1;0rad)
  Width = 7
FEATURE [Part::Box] Box211  label="二段目　"
  AttacherType = Attacher::AttachEngine3D
  Height = 5
  Length = 144.2
  Placement = pos=(-106,-108,32) rot=(0,0,1;0rad)
  Width = 184
FEATURE [Part::Box] Box215  label="立方体193"
  AttacherType = Attacher::AttachEngine3D
  Height = 5
  Length = 54
  Placement = pos=(-60.9,-108,32) rot=(0,0,1;0rad)
  Width = 71
FEATURE [Part::Box] Box263  label="立方体237"
  AttacherType = Attacher::AttachEngine3D
  Height = 20.4
  Length = 45.2
  Placement = pos=(-48.6,-98,10) rot=(0,0,1;0rad)
  Width = 5
FEATURE [Part::Box] Box264  label="立方体238"
  AttacherType = Attacher::AttachEngine3D
  Height = 20.4
  Length = 45.2
  Placement = pos=(-48.6,-98,10) rot=(0,0,1;0rad)
  Width = 5
FEATURE [Part::Box] Box266  label="立方体240"
  AttacherType = Attacher::AttachEngine3D
  Height = 50
  Length = 12
  Placement = pos=(-106,-58,37) rot=(1,0,0;1.5708rad)
  Width = 36
FEATURE [Part::Box] Box268  label="立方体242"
  AttacherType = Attacher::AttachEngine3D
  Height = 50
  Length = 12
  Placement = pos=(26.2,-58,37) rot=(1,0,0;1.5708rad)
  Width = 36
FEATURE [Part::Box] Box294  label="立方体266"
  AttacherType = Attacher::AttachEngine3D
  Height = 3
  Length = 3
  Placement = pos=(-57,-22,37) rot=(0,0,1;0rad)
  Width = 68
FEATURE [Part::Box] Box296  label="立方体268"
  AttacherType = Attacher::AttachEngine3D
  Height = 3
  Length = 36
  Placement = pos=(-90,43,37) rot=(0,0,1;0rad)
  Width = 3
FEATURE [Part::Box] Box298  label="立方体270"
  AttacherType = Attacher::AttachEngine3D
  Height = 12
  Length = 10
  Placement = pos=(-62,66,37) rot=(0,0,1;0rad)
  Width = 10
FEATURE [Part::Box] Box299  label="立方体271"
  AttacherType = Attacher::AttachEngine3D
  Height = 12
  Length = 10
  Placement = pos=(-62,-32,37) rot=(0,0,1;0rad)
  Width = 10
FEATURE [Part::Box] Box300  label="立方体272"
  AttacherType = Attacher::AttachEngine3D
  Height = 12
  Length = 10
  Placement = pos=(-106,-32,37) rot=(0,0,1;0rad)
  Width = 10
FEATURE [Part::Box] Box301  label="立方体273"
  AttacherType = Attacher::AttachEngine3D
  Height = 12
  Length = 10
  Placement = pos=(-106,66,37) rot=(0,0,1;0rad)
  Width = 10
FEATURE [Part::Box] Box324  label="立方体296"
  AttacherType = Attacher::AttachEngine3D
  Height = 3
  Length = 3
  Placement = pos=(-90,-22,37) rot=(0,0,1;0rad)
  Width = 68
FEATURE [Part::Box] Box327  label="立方体299"
  AttacherType = Attacher::AttachEngine3D
  Height = 20
  Length = 10
  Placement = pos=(28,-32,37) rot=(0,0,1;0rad)
  Width = 10
FEATURE [Part::Box] Box328  label="立方体300"
  AttacherType = Attacher::AttachEngine3D
  Height = 20
  Length = 10
  Placement = pos=(-52,-32,37) rot=(0,0,1;0rad)
  Width = 10
FEATURE [Part::Box] Box329  label="立方体301"
  AttacherType = Attacher::AttachEngine3D
  Height = 20
  Length = 10
  Placement = pos=(28,58,37) rot=(0,0,1;0rad)
  Width = 10
FEATURE [Part::Box] Box330  label="立方体302"
  AttacherType = Attacher::AttachEngine3D
  Height = 20
  Length = 10
  Placement = pos=(-52,58,37) rot=(0,0,1;0rad)
  Width = 10
FEATURE [Part::Box] Box343  label="立方体315"
  AttacherType = Attacher::AttachEngine3D
  Height = 25
  Length = 54
  Placement = pos=(-60.9,-98,22) rot=(0,0,1;0rad)
  Width = 5
FEATURE [Part::Box] Box359  label="リボバッテリーケース"
  AttacherType = Attacher::AttachEngine3D
  Height = 20
  Length = 42
  Placement = pos=(-14,-20,37) rot=(0,0,1;0rad)
  Width = 83
FEATURE [Part::Box] Box377  label="立方体"
  AttacherType = Attacher::AttachEngine3D
  Height = 8
  Length = 74
  Placement = pos=(-71,-79,37) rot=(0,0,1;0rad)
  Width = 35
FEATURE [Part::Box] Box378  label="立方体348"
  AttacherType = Attacher::AttachEngine3D
  Height = 8
  Length = 36
  Placement = pos=(-52,-55,32) rot=(0,0,1;0rad)
  Width = 31
FEATURE [Part::Box] Box379  label="立方体349"
  AttacherType = Attacher::AttachEngine3D
  Height = 6.9
  Length = 16
  Placement = pos=(22.2,-14,25.1) rot=(0,0,1;0rad)
  Width = 8
FEATURE [Part::Box] Box380  label="立方体350"
  AttacherType = Attacher::AttachEngine3D
  Height = 6.9
  Length = 16
  Placement = pos=(-106,-14,25.1) rot=(0,0,1;0rad)
  Width = 8
FEATURE [Part::Box] Box381  label="立方体351"
  AttacherType = Attacher::AttachEngine3D
  Height = 25
  Length = 15
  Placement = pos=(-41.9,-108,30) rot=(0,0,1;0rad)
  Width = 15
FEATURE [Part::Box] Box382  label="立方体352"
  AttacherType = Attacher::AttachEngine3D
  Height = 25
  Length = 25
  Placement = pos=(-46.9,-94,30) rot=(0,0,1;0rad)
  Width = 1
FEATURE [Part::Box] Box383  label="立方体353"
  AttacherType = Attacher::AttachEngine3D
  Height = 7
  Length = 84
  Placement = pos=(-75.9,-86,32) rot=(0,0,1;0rad)
  Width = 10
FEATURE [Part::Box] Box386  label="立方体356"
  AttacherType = Attacher::AttachEngine3D
  Height = 31
  Length = 54
  Placement = pos=(-60.9,-108,19) rot=(0,0,1;0rad)
  Width = 12
FEATURE [Part::Box] Box387  label="立方体357"
  AttacherType = Attacher::AttachEngine3D
  Height = 3
  Length = 54
  Placement = pos=(-60.9,-98,47) rot=(0,0,1;0rad)
  Width = 5
FEATURE [Part::Box] Box392  label="立方体362"
  AttacherType = Attacher::AttachEngine3D
  Height = 14
  Length = 84
  Placement = pos=(-75.9,-87,32) rot=(-1,0,0;1.22173rad)
  Width = 10
FEATURE [Part::Box] Box395  label="立方体365"
  AttacherType = Attacher::AttachEngine3D
  Height = 10
  Length = 120
  Placement = pos=(-93.9,-86,27) rot=(0,0,1;0rad)
  Width = 10
FEATURE [Part::Box] Box398  label="立方体368"
  AttacherType = Attacher::AttachEngine3D
  Height = 3
  Length = 6
  Placement = pos=(-9,59,54) rot=(0,0,1;0rad)
  Width = 4
FEATURE [Part::Box] Box399  label="立方体369"
  AttacherType = Attacher::AttachEngine3D
  Height = 20
  Length = 3
  Placement = pos=(-3,59,37) rot=(0,0,1;0rad)
  Width = 4
FEATURE [Part::Box] Box403  label="立方体373"
  AttacherType = Attacher::AttachEngine3D
  Height = 25
  Length = 30
  Placement = pos=(-48.9,-108,22) rot=(0,0,1;0rad)
  Width = 5
FEATURE [Part::Box] Box404  label="立方体374"
  AttacherType = Attacher::AttachEngine3D
  Height = 15
  Length = 10
  Placement = pos=(-70.9,-108,22) rot=(0,0,1;0rad)
  Width = 9
FEATURE [Part::Box] Box405  label="立方体375"
  AttacherType = Attacher::AttachEngine3D
  Height = 15
  Length = 10
  Placement = pos=(-6.9,-108,22) rot=(0,0,1;0rad)
  Width = 9
FEATURE [Part::Box] Box413  label="立方体383"
  AttacherType = Attacher::AttachEngine3D
  Height = 5
  Length = 8.9
  Placement = pos=(-60.9,-45,32) rot=(0,0,1;0rad)
  Width = 8
FEATURE [Part::Box] Box414  label="立方体384"
  AttacherType = Attacher::AttachEngine3D
  Height = 5
  Length = 9.1
  Placement = pos=(-16,-45,32) rot=(0,0,1;0rad)
  Width = 8
FEATURE [Part::Box] Box415  label="立方体385"
  AttacherType = Attacher::AttachEngine3D
  Height = 3
  Length = 36
  Placement = pos=(-52,-45,54) rot=(0,0,1;0rad)
  Width = 21
FEATURE [Part::Box] Box416  label="立方体386"
  AttacherType = Attacher::AttachEngine3D
  Height = 25
  Length = 3
  Placement = pos=(-52,-45,32) rot=(0,0,1;0rad)
  Width = 21
FEATURE [Part::Box] Box417  label="立方体387"
  AttacherType = Attacher::AttachEngine3D
  Height = 25
  Length = 3
  Placement = pos=(-19,-45,32) rot=(0,0,1;0rad)
  Width = 21
FEATURE [Part::Box] Box427  label="立方体397"
  AttacherType = Attacher::AttachEngine3D
  Height = 13
  Length = 30
  Placement = pos=(-94,-22,34) rot=(0,0,1;0rad)
  Width = 65
FEATURE [Part::Box] Box428  label="立方体398"
  AttacherType = Attacher::AttachEngine3D
  Height = 13
  Length = 12
  Placement = pos=(-85,-32,34) rot=(0,0,1;0rad)
  Width = 10
FEATURE [Part::Box] Box435  label="立方体405"
  AttacherType = Attacher::AttachEngine3D
  Height = 5
  Length = 22
  Placement = pos=(0,-24,32) rot=(0,0,1;0rad)
  Width = 84
FEATURE [Part::Box] Box436  label="立方体406"
  AttacherType = Attacher::AttachEngine3D
  Height = 5
  Length = 28
  Placement = pos=(-70,-14,32) rot=(0,0,1;0rad)
  Width = 75
FEATURE [Part::Box] Box437  label="立方体407"
  AttacherType = Attacher::AttachEngine3D
  Height = 10
  Length = 12
  Placement = pos=(26.2,-90,37) rot=(0,0,1;0rad)
  Width = 34
FEATURE [Part::Box] Box438  label="立方体408"
  AttacherType = Attacher::AttachEngine3D
  Height = 10
  Length = 12
  Placement = pos=(-106,-90,37) rot=(0,0,1;0rad)
  Width = 34
FEATURE [Part::Box] Box439  label="立方体409"
  AttacherType = Attacher::AttachEngine3D
  Height = 25
  Length = 6
  Placement = pos=(-66.9,-64.9,37) rot=(0,0,1;0rad)
  Width = 15
FEATURE [Part::Box] Box440  label="立方体410"
  AttacherType = Attacher::AttachEngine3D
  Height = 5
  Length = 16
  Placement = pos=(-82.9,-64.9,37) rot=(0,0,1;0rad)
  Width = 15
FEATURE [Part::Box] Box441  label="立方体411"
  AttacherType = Attacher::AttachEngine3D
  Height = 25
  Length = 6
  Placement = pos=(-6.9,-64.9,37) rot=(0,0,1;0rad)
  Width = 15
FEATURE [Part::Box] Box442  label="立方体412"
  AttacherType = Attacher::AttachEngine3D
  Height = 5
  Length = 16
  Placement = pos=(-0.9,-64.9,37) rot=(0,0,1;0rad)
  Width = 15
FEATURE [Part::Chamfer] Chamfer029
  Base = -> Box404
  EdgeLinks = -> Box404 [Edge4]
  Edges = 1 edges r=9.99: [Edge4]
FEATURE [Part::Chamfer] Chamfer030
  Base = -> Box405
  EdgeLinks = -> Box405 [Edge8]
  Edges = 1 edges r=9.99: [Edge8]
FEATURE [Part::Cut] Cut250  label="リボケース"
  Base = -> Box359
  Placement = pos=(-28,-4,0) rot=(0,0,1;0rad)
  Tool = -> Box
FEATURE [Part::Cut] Cut257
  Base = -> Box211
  Tool = -> Box215
FEATURE [Part::Cut] Cut269
  Base = -> Box386
  Tool = -> Box343
FEATURE [Part::Cut] Cut273
  Base = -> Box383
  Tool = -> Box392
FEATURE [Part::Cut] Cut324
  Base = -> Cut257
  Refine = true
  Tool = -> Box378
FEATURE [Part::Cut] Cut345
  Base = -> Cut324
  Refine = true
  Tool = -> Box395
FEATURE [Part::Cylinder] Cylinder068  label="円柱068"
  Angle = 360
  AttacherType = Attacher::AttachEngine3D
  FirstAngle = 0
  Height = 15
  Placement = pos=(-13,-93,20.2) rot=(1,0,0;1.5708rad)
  Radius = 8
  SecondAngle = 0
FEATURE [Part::Cylinder] Cylinder069  label="円柱069"
  Angle = 360
  AttacherType = Attacher::AttachEngine3D
  FirstAngle = 0
  Height = 15
  Placement = pos=(-39,-93,20.2) rot=(1,0,0;1.5708rad)
  Radius = 8
  SecondAngle = 0
FEATURE [Part::Cylinder] Cylinder070  label="円柱070"
  Angle = 360
  AttacherType = Attacher::AttachEngine3D
  FirstAngle = 0
  Height = 15
  Placement = pos=(-13,-93,20.2) rot=(1,0,0;1.5708rad)
  Radius = 8
  SecondAngle = 0
FEATURE [Part::Cylinder] Cylinder071  label="円柱071"
  Angle = 360
  AttacherType = Attacher::AttachEngine3D
  FirstAngle = 0
  Height = 15
  Placement = pos=(-39,-93,20.2) rot=(1,0,0;1.5708rad)
  Radius = 8
  SecondAngle = 0
FEATURE [Part::Cylinder] Cylinder189  label="円柱189"
  Angle = 360
  AttacherType = Attacher::AttachEngine3D
  FirstAngle = 0
  Height = 20
  Placement = pos=(-53,-88,43) rot=(1,0,0;1.5708rad)
  Radius = 2
  SecondAngle = 0
FEATURE [Part::Cylinder] Cylinder190  label="円柱190"
  Angle = 360
  AttacherType = Attacher::AttachEngine3D
  FirstAngle = 0
  Height = 20
  Placement = pos=(-16,-88,43) rot=(1,0,0;1.5708rad)
  Radius = 2
  SecondAngle = 0
FEATURE [Part::Cylinder] Cylinder191  label="円柱191"
  Angle = 360
  AttacherType = Attacher::AttachEngine3D
  FirstAngle = 0
  Height = 13
  Placement = pos=(-55,-69,-5) rot=(0,0,1;0rad)
  Radius = 2
  SecondAngle = 0
FEATURE [Part::Cylinder] Cylinder192  label="円柱192"
  Angle = 360
  AttacherType = Attacher::AttachEngine3D
  FirstAngle = 0
  Height = 13
  Placement = pos=(-12,-69,-5) rot=(0,0,1;0rad)
  Radius = 2
  SecondAngle = 0
FEATURE [Part::Cylinder] Cylinder195  label="円柱195"
  Angle = 360
  AttacherType = Attacher::AttachEngine3D
  FirstAngle = 0
  Height = 19
  Placement = pos=(-101,-27,32) rot=(0,0,1;0rad)
  Radius = 2
  SecondAngle = 0
FEATURE [Part::Cylinder] Cylinder200  label="円柱200"
  Angle = 360
  AttacherType = Attacher::AttachEngine3D
  FirstAngle = 0
  Height = 19
  Placement = pos=(-57,-27,32) rot=(0,0,1;0rad)
  Radius = 2
  SecondAngle = 0
FEATURE [Part::Cylinder] Cylinder201  label="円柱201"
  Angle = 360
  AttacherType = Attacher::AttachEngine3D
  FirstAngle = 0
  Height = 19
  Placement = pos=(-101,71,32) rot=(0,0,1;0rad)
  Radius = 2
  SecondAngle = 0
FEATURE [Part::Cylinder] Cylinder202  label="円柱202"
  Angle = 360
  AttacherType = Attacher::AttachEngine3D
  FirstAngle = 0
  Height = 19
  Placement = pos=(-57,71,32) rot=(0,0,1;0rad)
  Radius = 2
  SecondAngle = 0
FEATURE [Part::Cylinder] Cylinder207  label="円柱207"
  Angle = 360
  AttacherType = Attacher::AttachEngine3D
  FirstAngle = 0
  Height = 25
  Placement = pos=(33,-27,32) rot=(0,0,1;0rad)
  Radius = 2
  SecondAngle = 0
FEATURE [Part::Cylinder] Cylinder208  label="円柱208"
  Angle = 360
  AttacherType = Attacher::AttachEngine3D
  FirstAngle = 0
  Height = 25
  Placement = pos=(33,63,32) rot=(0,0,1;0rad)
  Radius = 2
  SecondAngle = 0
FEATURE [Part::Cylinder] Cylinder209  label="円柱209"
  Angle = 360
  AttacherType = Attacher::AttachEngine3D
  FirstAngle = 0
  Height = 25
  Placement = pos=(-47,63,32) rot=(0,0,1;0rad)
  Radius = 2
  SecondAngle = 0
FEATURE [Part::Cylinder] Cylinder210  label="円柱210"
  Angle = 360
  AttacherType = Attacher::AttachEngine3D
  FirstAngle = 0
  Height = 25
  Placement = pos=(-47,-27,32) rot=(0,0,1;0rad)
  Radius = 2
  SecondAngle = 0
FEATURE [Part::Cylinder] Cylinder271  label="円柱271"
  Angle = 360
  AttacherType = Attacher::AttachEngine3D
  FirstAngle = 0
  Height = 5
  Placement = pos=(-101,-27,32) rot=(0,0,1;0rad)
  Radius = 4
  SecondAngle = 0
FEATURE [Part::Cylinder] Cylinder272  label="円柱272"
  Angle = 360
  AttacherType = Attacher::AttachEngine3D
  FirstAngle = 0
  Height = 5
  Placement = pos=(-57,-27,32) rot=(0,0,1;0rad)
  Radius = 4
  SecondAngle = 0
FEATURE [Part::Cylinder] Cylinder273  label="円柱273"
  Angle = 360
  AttacherType = Attacher::AttachEngine3D
  FirstAngle = 0
  Height = 5
  Placement = pos=(-57,71,32) rot=(0,0,1;0rad)
  Radius = 4
  SecondAngle = 0
FEATURE [Part::Cylinder] Cylinder274  label="円柱274"
  Angle = 360
  AttacherType = Attacher::AttachEngine3D
  FirstAngle = 0
  Height = 5
  Placement = pos=(-101,71,32) rot=(0,0,1;0rad)
  Radius = 4
  SecondAngle = 0
FEATURE [Part::Cylinder] Cylinder275  label="円柱275"
  Angle = 360
  AttacherType = Attacher::AttachEngine3D
  FirstAngle = 0
  Height = 5
  Placement = pos=(-47,-27,32) rot=(0,0,1;0rad)
  Radius = 4
  SecondAngle = 0
FEATURE [Part::Cylinder] Cylinder276  label="円柱276"
  Angle = 360
  AttacherType = Attacher::AttachEngine3D
  FirstAngle = 0
  Height = 5
  Placement = pos=(33,-27,32) rot=(0,0,1;0rad)
  Radius = 4
  SecondAngle = 0
FEATURE [Part::Cylinder] Cylinder277  label="円柱277"
  Angle = 360
  AttacherType = Attacher::AttachEngine3D
  FirstAngle = 0
  Height = 5
  Placement = pos=(-47,63,32) rot=(0,0,1;0rad)
  Radius = 4
  SecondAngle = 0
FEATURE [Part::Cylinder] Cylinder278  label="円柱278"
  Angle = 360
  AttacherType = Attacher::AttachEngine3D
  FirstAngle = 0
  Height = 5
  Placement = pos=(33,63,32) rot=(0,0,1;0rad)
  Radius = 4
  SecondAngle = 0
FEATURE [Part::Cylinder] Cylinder285  label="円柱285"
  Angle = 360
  AttacherType = Attacher::AttachEngine3D
  FirstAngle = 0
  Height = 10
  Placement = pos=(30.2,-10,15.1) rot=(0,0,1;0rad)
  Radius = 4
  SecondAngle = 0
FEATURE [Part::Cylinder] Cylinder286  label="円柱286"
  Angle = 360
  AttacherType = Attacher::AttachEngine3D
  FirstAngle = 0
  Height = 10
  Placement = pos=(-98,-10,15.1) rot=(0,0,1;0rad)
  Radius = 4
  SecondAngle = 0
FEATURE [Part::Cylinder] Cylinder292  label="円柱292"
  Angle = 360
  AttacherType = Attacher::AttachEngine3D
  FirstAngle = 0
  Height = 10
  Placement = pos=(-36,72,32) rot=(0,0,1;0rad)
  Radius = 2
  SecondAngle = 0
FEATURE [Part::Cylinder] Cylinder293  label="円柱293"
  Angle = 360
  AttacherType = Attacher::AttachEngine3D
  FirstAngle = 0
  Height = 10
  Placement = pos=(-15,72,32) rot=(0,0,1;0rad)
  Radius = 2
  SecondAngle = 0
FEATURE [Part::Cylinder] Cylinder308  label="円柱308"
  Angle = 360
  AttacherType = Attacher::AttachEngine3D
  FirstAngle = 0
  Height = 42
  Placement = pos=(-81.9,72,-5) rot=(0,0,1;0rad)
  Radius = 2
  SecondAngle = 0
FEATURE [Part::Cylinder] Cylinder309  label="円柱309"
  Angle = 360
  AttacherType = Attacher::AttachEngine3D
  FirstAngle = 0
  Height = 42
  Placement = pos=(14.1,72,-5) rot=(0,0,1;0rad)
  Radius = 2
  SecondAngle = 0
FEATURE [Part::Cylinder] Cylinder327  label="円柱327"
  Angle = 360
  AttacherType = Attacher::AttachEngine3D
  FirstAngle = 0
  Height = 47
  Placement = pos=(7,-98,-5) rot=(0,0,1;0rad)
  Radius = 2
  SecondAngle = 0
FEATURE [Part::Cylinder] Cylinder328  label="円柱328"
  Angle = 360
  AttacherType = Attacher::AttachEngine3D
  FirstAngle = 0
  Height = 47
  Placement = pos=(-75,-98,-5) rot=(0,0,1;0rad)
  Radius = 2
  SecondAngle = 0
FEATURE [Part::Cylinder] Cylinder329  label="円柱329"
  Angle = 360
  AttacherType = Attacher::AttachEngine3D
  FirstAngle = 0
  Height = 47
  Placement = pos=(7,-98,-5) rot=(0,0,1;0rad)
  Radius = 2
  SecondAngle = 0
FEATURE [Part::Cylinder] Cylinder330  label="円柱330"
  Angle = 360
  AttacherType = Attacher::AttachEngine3D
  FirstAngle = 0
  Height = 47
  Placement = pos=(-75,-98,-5) rot=(0,0,1;0rad)
  Radius = 2
  SecondAngle = 0
FEATURE [Part::Fillet] Fillet007
  Base = -> Cut273
  EdgeLinks = -> Cut273 [Edge5]
  Edges = 1 edges r=1: [Edge5]
FEATURE [Part::MultiFuse] Fusion112
  Placement = pos=(-1,-109,40) rot=(0,0,-1;1.5708rad)
  Refine = true
  Shapes = -> [Box263,Cylinder069,Cylinder068]
FEATURE [Part::Cut] Cut333
  Base = -> Box266
  Refine = true
  Tool = -> Fusion112
FEATURE [Part::Chamfer] Chamfer038
  Base = -> Cut333
  EdgeLinks = -> Cut333 [Edge16,Edge18]
  Edges = 2 edges r=1.5: [Edge16,Edge18]
  Placement = pos=(0,10,0) rot=(0,0,1;0rad)
FEATURE [Part::Cut] Cut346
  Base = -> Chamfer038
  Placement = pos=(0,10,0) rot=(0,0,1;0rad)
  Refine = true
  Tool = -> Box438
FEATURE [Part::MultiFuse] Fusion113
  Placement = pos=(-66.8,-57,40) rot=(0,0,1;1.5708rad)
  Refine = true
  Shapes = -> [Box264,Cylinder071,Cylinder070]
FEATURE [Part::Cut] Cut332
  Base = -> Box268
  Refine = true
  Tool = -> Fusion113
FEATURE [Part::Chamfer] Chamfer035
  Base = -> Cut332
  EdgeLinks = -> Cut332 [Edge27,Edge28]
  Edges = 2 edges r=1.5: [Edge27,Edge28]
  Placement = pos=(0,10,0) rot=(0,0,1;0rad)
FEATURE [Part::Cut] Cut344
  Base = -> Chamfer035
  Placement = pos=(0,10,0) rot=(0,0,1;0rad)
  Refine = true
  Tool = -> Box437
FEATURE [Part::MultiFuse] Fusion192
  Placement = pos=(-16,0,0) rot=(0,0,1;0rad)
  Shapes = -> [Box294,Box296,Box324]
FEATURE [Part::MultiFuse] Fusion198
  Shapes = -> [Cylinder271,Cylinder272,Cylinder273,Cylinder274]
FEATURE [Part::MultiFuse] Fusion199
  Shapes = -> [Cylinder200,Cylinder195,Cylinder201,Cylinder202]
FEATURE [Part::MultiFuse] Fusion200
  Shapes = -> [Box300,Box299,Box298,Box301]
FEATURE [Part::Cut] Cut328
  Base = -> Fusion200
  Refine = true
  Tool = -> Fusion199
FEATURE [Part::MultiFuse] Fusion204
  Shapes = -> [Box328,Box327,Box329,Box330]
FEATURE [Part::MultiFuse] Fusion207
  Shapes = -> [Cylinder210,Cylinder207,Cylinder208,Cylinder209]
FEATURE [Part::Cut] Cut322
  Base = -> Fusion204
  Placement = pos=(0,8,0) rot=(0,0,1;0rad)
  Refine = true
  Tool = -> Fusion207
FEATURE [Part::MultiFuse] Fusion208
  Placement = pos=(0,8,0) rot=(0,0,1;0rad)
  Shapes = -> [Cylinder275,Cylinder276,Cylinder277,Cylinder278]
FEATURE [Part::MultiFuse] Fusion209
  Placement = pos=(0,5,42) rot=(0,0,1;0rad)
  Shapes = -> [Cylinder192,Cylinder191]
FEATURE [Part::MultiFuse] Fusion211
  Placement = pos=(-8.5,-35,138) rot=(1,0,0;1.5708rad)
  Shapes = -> [Box100,Box101]
FEATURE [Part::Cut] Cut259
  Base = -> Box377
  Tool = -> Fusion211
FEATURE [Part::Cut] Cut260
  Base = -> Cut259
  Placement = pos=(0,3,0) rot=(0,0,1;0rad)
  Tool = -> Fusion209
FEATURE [Part::Chamfer] Chamfer025
  Base = -> Cut260
  EdgeLinks = -> Cut260 [Edge2,Edge9]
  Edges = 2 edges r=7.99: [Edge2,Edge9]
FEATURE [Part::MultiFuse] Fusion217
  Shapes = -> [Cylinder285,Box379]
FEATURE [Part::MultiFuse] Fusion218
  Shapes = -> [Cylinder286,Box380]
FEATURE [Part::MultiFuse] Fusion219
  Shapes = -> [Fusion217,Fusion218]
FEATURE [Part::MultiFuse] Fusion221
  Placement = pos=(0,-5,-8) rot=(0,0,1;0rad)
  Shapes = -> [Box381,Box382]
FEATURE [Part::Cut] Cut270
  Base = -> Cut269
  Tool = -> Fusion221
FEATURE [Part::Cut] Cut279
  Base = -> Cut270
  Tool = -> Box387
FEATURE [Part::MultiFuse] Fusion228
  Shapes = -> [Box398,Box399,Cut250]
FEATURE [Part::MultiFuse] Fusion230
  Shapes = -> [Cylinder292,Cylinder293]
FEATURE [Part::MultiFuse] Fusion232
  Shapes = -> [Cylinder189,Cylinder190]
FEATURE [Part::Cut] Cut281
  Base = -> Cut279
  Tool = -> Fusion232
FEATURE [Part::Cut] Cut282
  Base = -> Cut281
  Tool = -> Box403
FEATURE [Part::MultiFuse] Fusion244
  Shapes = -> [Cut282,Chamfer029,Chamfer030]
FEATURE [Part::MultiFuse] Fusion257
  Shapes = -> [Box413,Box414,Box415,Box416,Box417]
FEATURE [Part::MultiFuse] Fusion275
  Placement = pos=(0,-5,0) rot=(0,0,1;0rad)
  Shapes = -> [Cylinder308,Cylinder309]
FEATURE [Part::MultiFuse] Fusion281  label=" Coral001"
  Placement = pos=(-9,0,0) rot=(0,0,1;0rad)
  Shapes = -> [Box427,Box428]
FEATURE [Part::Cut] Cut347
  Base = -> Cut345
  Refine = true
  Tool = -> Fusion281
FEATURE [Part::Chamfer] Chamfer039
  Base = -> Cut347
  EdgeLinks = -> Cut347 [Edge1,Edge54]
  Edges = 2 edges r=20: [Edge1,Edge54]
FEATURE [Part::Fuse] Fusion300
  Base = -> Fusion198
  Refine = true
  Tool = -> Fusion208
FEATURE [Part::Fuse] Fusion301
  Base = -> Fusion230
  Refine = true
  Tool = -> Fusion300
FEATURE [Part::MultiFuse] Fusion304
  Refine = true
  Shapes = -> [Fusion219,Cut322]
FEATURE [Part::MultiFuse] Fusion305
  Refine = true
  Shapes = -> [Fusion304,Cut328]
FEATURE [Part::MultiFuse] Fusion316
  Refine = true
  Shapes = -> [Cylinder327,Cylinder328]
FEATURE [Part::MultiFuse] Fusion317
  Placement = pos=(0,41,0) rot=(0,0,1;0rad)
  Refine = true
  Shapes = -> [Cylinder329,Cylinder330]
FEATURE [Part::MultiFuse] Fusion328
  Refine = true
  Shapes = -> [Fusion316,Fusion317,Fusion275]
FEATURE [Part::Cut] Cut349
  Base = -> Chamfer039
  Refine = true
  Tool = -> Fusion328
FEATURE [Part::MultiFuse] Fusion335
  Refine = true
  Shapes = -> [Cut346,Chamfer025,Fillet007,Fusion244,Cut344]
FEATURE [Part::MultiFuse] Fusion336
  Refine = true
  Shapes = -> [Fusion192,Fusion228,Fusion257]
FEATURE [Part::MultiFuse] Fusion337
  Refine = true
  Shapes = -> [Fusion335,Fusion336,Fusion305]
FEATURE [Part::MultiFuse] Fusion338
  Refine = true
  Shapes = -> [Box442,Box441,Box439,Box440]
FEATURE [Part::Cut] Cut348
  Base = -> Fusion337
  Refine = true
  Tool = -> Fusion338
FEATURE [Part::MultiFuse] Fusion339
  Refine = true
  Shapes = -> [Cut348,Cut349]
FEATURE [Part::Cut] Cut350
  Base = -> Fusion339
  Refine = true
  Tool = -> Fusion301
FEATURE [Part::MultiFuse] Fusion340
  Refine = true
  Shapes = -> [Box435,Box436]
FEATURE [Part::Cut] Cut351  label="Chassis 2"
  Base = -> Cut350
  Refine = true
  Tool = -> Fusion340
FEATURE [Part::Box] Box309  label="立方体281"
  AttacherType = Attacher::AttachEngine3D
  Height = 5
  Length = 43
  Placement = pos=(8,-18,0) rot=(0,0,1;0rad)
  Width = 16
FEATURE [Part::Box] Box310  label="立方体282"
  AttacherType = Attacher::AttachEngine3D
  Height = 5
  Length = 43
  Placement = pos=(-119,-18,0) rot=(0,0,1;0rad)
  Width = 16
FEATURE [Part::Cylinder] Cylinder033  label="円柱033"
  Angle = 360
  AttacherType = Attacher::AttachEngine3D
  FirstAngle = 0
  Height = 32
  Placement = pos=(30.2,-10,0) rot=(0,0,1;0rad)
  Radius = 4
  SecondAngle = 0
FEATURE [Part::Cut] Cut187
  Base = -> Box309
  Tool = -> Cylinder033
FEATURE [Part::Cylinder] Cylinder034  label="円柱034"
  Angle = 360
  AttacherType = Attacher::AttachEngine3D
  FirstAngle = 0
  Height = 32
  Placement = pos=(-98,-10,0) rot=(0,0,1;0rad)
  Radius = 4
  SecondAngle = 0
FEATURE [Part::Cut] Cut183
  Base = -> Box310
  Tool = -> Cylinder034
FEATURE [Part::Cylinder] Cylinder127  label="円柱127"
  Angle = 360
  AttacherType = Attacher::AttachEngine3D
  FirstAngle = 0
  Height = 170.2
  Placement = pos=(-119.1,28,146.3) rot=(0,1,0;1.5708rad)
  Radius = 10
  SecondAngle = 0
FEATURE [Part::Cylinder] Cylinder236  label="円柱236"
  Angle = 360
  AttacherType = Attacher::AttachEngine3D
  FirstAngle = 0
  Height = 42
  Placement = pos=(-85,-10,-5) rot=(0,0,1;0rad)
  Radius = 2
  SecondAngle = 0
FEATURE [Part::Cut] Cut202
  Base = -> Cut183
  Tool = -> Cylinder236
FEATURE [Part::Cylinder] Cylinder237  label="円柱237"
  Angle = 360
  AttacherType = Attacher::AttachEngine3D
  FirstAngle = 0
  Height = 42
  Placement = pos=(17.2,-10,-5) rot=(0,0,1;0rad)
  Radius = 2
  SecondAngle = 0
FEATURE [Part::Cut] Cut203
  Base = -> Cut187
  Tool = -> Cylinder237
FEATURE [Part::Part2DObjectPython] Wire004  # Draft 2D object (typed FeaturePython)
  Area = 2400
  ChamferSize = 0
  Closed = true
  End = (40,150,0)
  FilletRadius = 0
  Length = 342.483
  MakeFace = true
  Points = (4) [(0,0,0),(16,0,0),(56,150,0),(40,150,0)]
  Start = (0,0,0)
  Subdivisions = 0
FEATURE [Part::Extrusion] Extrude009
  Base = -> Wire004
  Dir = (0,0,1)
  DirMode = 2
  FaceMakerClass = Part::FaceMakerBullseye
  FaceMakerMode = 3
  LengthFwd = 10
  LengthRev = 0
  Solid = false
  Symmetric = false
FEATURE [Part::Fillet] Fillet002
  Base = -> Extrude009
  EdgeLinks = -> Extrude009 [Edge5,Edge8]
  Edges = 2 edges r=7.72: [Edge5,Edge8]
  Placement = pos=(41,-18,5) rot=(0.57735,0.57735,0.57735;2.0944rad)
FEATURE [Part::Part2DObjectPython] Wire005  # Draft 2D object (typed FeaturePython)
  Area = 2400
  ChamferSize = 0
  Closed = true
  End = (40,150,0)
  FilletRadius = 0
  Length = 342.483
  MakeFace = true
  Points = (4) [(0,0,0),(16,0,0),(56,150,0),(40,150,0)]
  Start = (0,0,0)
  Subdivisions = 0
FEATURE [Part::Extrusion] Extrude010
  Base = -> Wire005
  Dir = (0,0,1)
  DirMode = 2
  FaceMakerClass = Part::FaceMakerBullseye
  FaceMakerMode = 3
  LengthFwd = 10
  LengthRev = 0
  Solid = false
  Symmetric = false
FEATURE [Part::Fillet] Fillet003
  Base = -> Extrude010
  EdgeLinks = -> Extrude010 [Edge5,Edge8]
  Edges = 2 edges r=7.72: [Edge5,Edge8]
  Placement = pos=(-119,-18,5) rot=(0.57735,0.57735,0.57735;2.0944rad)
FEATURE [Part::MultiFuse] Fusion167
  Shapes = -> [Fillet002,Cylinder127,Fillet003]
FEATURE [Part::MultiFuse] Fusion169  label="Handle"
  Placement = pos=(0,0,20.1) rot=(0,0,1;0rad)
  Shapes = -> [Cut202,Fusion167,Cut203]
FEATURE [Part::Box] Box281  label="立方体253"
  AttacherType = Attacher::AttachEngine3D
  Height = 20.1
  Length = 27.3
  Placement = pos=(-71.6,-108,62) rot=(0,0,1;0rad)
  Width = 9
FEATURE [Part::Box] Box283  label="立方体255"
  AttacherType = Attacher::AttachEngine3D
  Height = 3
  Length = 66
  Placement = pos=(-71.6,-108,59) rot=(0,0,1;0rad)
  Width = 58.1
FEATURE [Part::Box] Box286  label="立方体258"
  AttacherType = Attacher::AttachEngine3D
  Height = 25
  Length = 6
  Placement = pos=(-66.9,-108,37) rot=(0,0,1;0rad)
  Width = 20
FEATURE [Part::Box] Box288  label="立方体260"
  AttacherType = Attacher::AttachEngine3D
  Height = 25
  Length = 6
  Placement = pos=(-6.9,-108,37) rot=(0,0,1;0rad)
  Width = 20
FEATURE [Part::Box] Box406  label="立方体376"
  AttacherType = Attacher::AttachEngine3D
  Height = 5
  Length = 16
  Placement = pos=(-82.9,-108,37) rot=(0,0,1;0rad)
  Width = 20
FEATURE [Part::Box] Box407  label="立方体377"
  AttacherType = Attacher::AttachEngine3D
  Height = 5
  Length = 16
  Placement = pos=(-0.9,-108,37) rot=(0,0,1;0rad)
  Width = 20
FEATURE [Part::Box] Box408  label="立方体378"
  AttacherType = Attacher::AttachEngine3D
  Height = 20.1
  Length = 27.3
  Placement = pos=(-71.6,-58.9,62) rot=(0,0,1;0rad)
  Width = 9
FEATURE [Part::Box] Box409  label="立方体379"
  AttacherType = Attacher::AttachEngine3D
  Height = 25
  Length = 6
  Placement = pos=(-66.9,-64.9,37) rot=(0,0,1;0rad)
  Width = 15
FEATURE [Part::Box] Box410  label="立方体380"
  AttacherType = Attacher::AttachEngine3D
  Height = 5
  Length = 16
  Placement = pos=(-82.9,-64.9,37) rot=(0,0,1;0rad)
  Width = 15
FEATURE [Part::Box] Box411  label="立方体381"
  AttacherType = Attacher::AttachEngine3D
  Height = 25
  Length = 6
  Placement = pos=(-6.9,-64.9,37) rot=(0,0,1;0rad)
  Width = 15
FEATURE [Part::Box] Box412  label="立方体382"
  AttacherType = Attacher::AttachEngine3D
  Height = 5
  Length = 16
  Placement = pos=(-0.9,-64.9,37) rot=(0,0,1;0rad)
  Width = 15
FEATURE [Part::Box] Box430  label="立方体400"
  AttacherType = Attacher::AttachEngine3D
  Height = 20.1
  Length = 6
  Placement = pos=(-66.5,-108,62) rot=(0,0,1;0rad)
  Width = 9
FEATURE [Part::Cylinder] Cylinder179  label="円柱179"
  Angle = 360
  AttacherType = Attacher::AttachEngine3D
  FirstAngle = 0
  Height = 30
  Placement = pos=(-71.6,-105.8,73) rot=(0,1,0;1.5708rad)
  Radius = 2
  SecondAngle = 0
FEATURE [Part::Cylinder] Cylinder180  label="円柱180"
  Angle = 360
  AttacherType = Attacher::AttachEngine3D
  FirstAngle = 0
  Height = 33
  Placement = pos=(-74.6,-105.8,63) rot=(0,1,0;1.5708rad)
  Radius = 2
  SecondAngle = 0
FEATURE [Part::Cylinder] Cylinder181  label="円柱181"
  Angle = 360
  AttacherType = Attacher::AttachEngine3D
  FirstAngle = 0
  Height = 30
  Placement = pos=(-71.6,-56.2,73) rot=(0,1,0;1.5708rad)
  Radius = 2
  SecondAngle = 0
FEATURE [Part::Cylinder] Cylinder182  label="円柱182"
  Angle = 360
  AttacherType = Attacher::AttachEngine3D
  FirstAngle = 0
  Height = 33
  Placement = pos=(-74.6,-56.2,63) rot=(0,1,0;1.5708rad)
  Radius = 2
  SecondAngle = 0
FEATURE [Part::Cylinder] Cylinder323  label="円柱323"
  Angle = 360
  AttacherType = Attacher::AttachEngine3D
  FirstAngle = 0
  Height = 47
  Placement = pos=(7,-98,-5) rot=(0,0,1;0rad)
  Radius = 2
  SecondAngle = 0
FEATURE [Part::Cylinder] Cylinder324  label="円柱324"
  Angle = 360
  AttacherType = Attacher::AttachEngine3D
  FirstAngle = 0
  Height = 47
  Placement = pos=(-75,-98,-5) rot=(0,0,1;0rad)
  Radius = 2
  SecondAngle = 0
FEATURE [Part::Cylinder] Cylinder325  label="円柱325"
  Angle = 360
  AttacherType = Attacher::AttachEngine3D
  FirstAngle = 0
  Height = 47
  Placement = pos=(7,-98,-5) rot=(0,0,1;0rad)
  Radius = 2
  SecondAngle = 0
FEATURE [Part::Cylinder] Cylinder326  label="円柱326"
  Angle = 360
  AttacherType = Attacher::AttachEngine3D
  FirstAngle = 0
  Height = 47
  Placement = pos=(-75,-98,-5) rot=(0,0,1;0rad)
  Radius = 2
  SecondAngle = 0
FEATURE [Part::MultiFuse] Fusion246
  Placement = pos=(0,2,4) rot=(0,0,1;0rad)
  Shapes = -> [Cylinder181,Cylinder182]
FEATURE [Part::MultiFuse] Fusion247
  Placement = pos=(0,2,4) rot=(0,0,1;0rad)
  Shapes = -> [Cylinder179,Cylinder180]
FEATURE [Part::MultiFuse] Fusion249
  Shapes = -> [Box406,Box286,Box407,Box288]
FEATURE [Part::MultiFuse] Fusion251
  Shapes = -> [Box283,Box281,Box408]
FEATURE [Part::MultiFuse] Fusion252
  Shapes = -> [Fusion246,Fusion247]
FEATURE [Part::Cut] Cut283
  Base = -> Fusion251
  Tool = -> Fusion252
FEATURE [Part::Cut] Cut336
  Base = -> Cut283
  Placement = pos=(4.7,0,0) rot=(0,0,1;0rad)
  Refine = true
  Tool = -> Box430
FEATURE [Part::MultiFuse] Fusion314
  Placement = pos=(0,41,0) rot=(0,0,1;0rad)
  Refine = true
  Shapes = -> [Cylinder323,Cylinder324]
FEATURE [Part::MultiFuse] Fusion315
  Refine = true
  Shapes = -> [Cylinder325,Cylinder326]
FEATURE [Part::MultiFuse] Fusion322
  Refine = true
  Shapes = -> [Box412,Box411,Box409,Box410]
FEATURE [Part::Cut] Cut338
  Base = -> Fusion322
  Refine = true
  Tool = -> Fusion314
FEATURE [Part::MultiFuse] Fusion323
  Refine = true
  Shapes = -> [Fusion249]
FEATURE [Part::Cut] Cut337
  Base = -> Fusion323
  Refine = true
  Tool = -> Fusion315
FEATURE [Part::MultiFuse] Fusion324  label="Arm saport"
  Refine = true
  Shapes = -> [Cut337,Cut338,Cut336]
FEATURE [Part::Box] Box273  label="立方体246"
  AttacherType = Attacher::AttachEngine3D
  Height = 20.1
  Length = 2.7
  Placement = pos=(109.3,-99.95,0) rot=(0,0,1;0rad)
  Width = 54
FEATURE [Part::Box] Box274  label="立方体247"
  AttacherType = Attacher::AttachEngine3D
  Height = 20.1
  Length = 38.8
  Placement = pos=(82,-93,0) rot=(0,0,1;0rad)
  Width = 40.1
FEATURE [Part::FeaturePython] CycloidGear  # WARN: FeaturePython — macro-defined, semantics opaque (R4)
  AttacherType = Attacher::AttachEngine3D
  Placement = pos=(-32.8,-91,71) rot=(0,1,0;1.5708rad)
  angular_backlash = 0
  backlash = 0
  clearance = 0.25
  double_helix = false
  head = 0
  head_fillet = 0
  height = 5.5
  helix_angle = 0
  inner_diameter = 12.5
  module = 0.24
  num_teeth = 25
  numpoints = 20
  outer_diameter = 7.5
  pitch_diameter = 6
  root_fillet = 0
  version = 1.3.0
  expr: angular_backlash = backlash / pitch_diameter * 360 ° / pi
  expr: inner_diameter = num_teeth / 2
  expr: pitch_diameter = num_teeth * module
FEATURE [Part::Cylinder] Cylinder183  label="円柱183"
  Angle = 360
  AttacherType = Attacher::AttachEngine3D
  FirstAngle = 0
  Height = 30
  Placement = pos=(-71.6,-105.8,73) rot=(0,1,0;1.5708rad)
  Radius = 2
  SecondAngle = 0
FEATURE [Part::Cylinder] Cylinder184  label="円柱184"
  Angle = 360
  AttacherType = Attacher::AttachEngine3D
  FirstAngle = 0
  Height = 33
  Placement = pos=(-74.6,-105.8,63) rot=(0,1,0;1.5708rad)
  Radius = 2
  SecondAngle = 0
FEATURE [Part::Cylinder] Cylinder185  label="円柱185"
  Angle = 360
  AttacherType = Attacher::AttachEngine3D
  FirstAngle = 0
  Height = 30
  Placement = pos=(-71.6,-56.2,73) rot=(0,1,0;1.5708rad)
  Radius = 2
  SecondAngle = 0
FEATURE [Part::Cylinder] Cylinder186  label="円柱186"
  Angle = 360
  AttacherType = Attacher::AttachEngine3D
  FirstAngle = 0
  Height = 33
  Placement = pos=(-74.6,-56.2,63) rot=(0,1,0;1.5708rad)
  Radius = 2
  SecondAngle = 0
FEATURE [Part::MultiFuse] Fusion118
  Placement = pos=(-153.6,-8,61) rot=(0,0,1;0rad)
  Shapes = -> [Box274,Box273]
FEATURE [Part::MultiFuse] Fusion121
  Placement = pos=(0,0,-3) rot=(0,0,1;0rad)
  Shapes = -> [Fusion118,CycloidGear]
FEATURE [Part::Cut] Cut140
  Base = -> Fusion121
  Tool = -> Cylinder183
FEATURE [Part::Cut] Cut141
  Base = -> Cut140
  Tool = -> Cylinder184
FEATURE [Part::Cut] Cut142
  Base = -> Cut141
  Tool = -> Cylinder185
FEATURE [Part::Cut] Cut143  label="Motor Arm"
  Base = -> Cut142
  Placement = pos=(4.7,2,4) rot=(0,0,1;0rad)
  Tool = -> Cylinder186
FEATURE [Part::Box] Box443  label="立方体413"
  AttacherType = Attacher::AttachEngine3D
  Height = 13
  Length = 7
  Placement = pos=(-26.6,-100,65.5) rot=(0,0,1;0rad)
  Width = 30
FEATURE [Part::Box] Box444  label="立方体414"
  AttacherType = Attacher::AttachEngine3D
  Height = 13
  Length = 7
  Placement = pos=(-26.6,-94,65.5) rot=(0,0,1;0rad)
  Width = 25
FEATURE [Part::Box] Box445  label="立方体415"
  AttacherType = Attacher::AttachEngine3D
  Height = 20.1
  Length = 38.8
  Placement = pos=(-66.9,-108,62) rot=(0,0,1;0rad)
  Width = 58.1
FEATURE [Part::Box] Box446  label="立方体416"
  AttacherType = Attacher::AttachEngine3D
  Height = 20.1
  Length = 2.7
  Placement = pos=(109.3,-99.95,0) rot=(0,0,1;0rad)
  Width = 54
FEATURE [Part::Box] Box447  label="立方体417"
  AttacherType = Attacher::AttachEngine3D
  Height = 20.1
  Length = 38.8
  Placement = pos=(82,-93,0) rot=(0,0,1;0rad)
  Width = 40.1
FEATURE [Part::FeaturePython] CycloidGear028  # WARN: FeaturePython — macro-defined, semantics opaque (R4)
  AttacherType = Attacher::AttachEngine3D
  Placement = pos=(-32.8,-91,71) rot=(0,1,0;1.5708rad)
  angular_backlash = 0
  backlash = 0
  clearance = 0.25
  double_helix = false
  head = 0
  head_fillet = 0
  height = 5.5
  helix_angle = 0
  inner_diameter = 12.5
  module = 0.24
  num_teeth = 25
  numpoints = 20
  outer_diameter = 7.5
  pitch_diameter = 6
  root_fillet = 0
  version = 1.3.0
  expr: angular_backlash = backlash / pitch_diameter * 360 ° / pi
  expr: inner_diameter = num_teeth / 2
  expr: pitch_diameter = num_teeth * module
FEATURE [Part::Cylinder] Cylinder344  label="円柱344"
  Angle = 360
  AttacherType = Attacher::AttachEngine3D
  FirstAngle = 0
  Height = 3
  Placement = pos=(-14.6,-89,72) rot=(0,1,0;1.5708rad)
  Radius = 5
  SecondAngle = 0
FEATURE [Part::Cylinder] Cylinder345  label="円柱345"
  Angle = 360
  AttacherType = Attacher::AttachEngine3D
  FirstAngle = 0
  Height = 3
  Placement = pos=(-14.6,-89,72) rot=(0,1,0;1.5708rad)
  Radius = 1.5
  SecondAngle = 0
FEATURE [Part::Cut] Cut363  label="Bearing Arm"
  Base = -> Cylinder344
  Refine = true
  Tool = -> Cylinder345
FEATURE [Part::Cylinder] Cylinder346  label="円柱346"
  Angle = 360
  AttacherType = Attacher::AttachEngine3D
  FirstAngle = 0
  Height = 15
  Placement = pos=(-26.6,-89,72) rot=(0,1,0;1.5708rad)
  Radius = 10
  SecondAngle = 0
FEATURE [Part::MultiCommon] Common
  Refine = true
  Shapes = -> [Cylinder346,Box443]
FEATURE [Part::Cylinder] Cylinder347  label="円柱347"
  Angle = 360
  AttacherType = Attacher::AttachEngine3D
  FirstAngle = 0
  Height = 30
  Placement = pos=(-71.6,-105.8,73) rot=(0,1,0;1.5708rad)
  Radius = 2
  SecondAngle = 0
FEATURE [Part::Cylinder] Cylinder348  label="円柱348"
  Angle = 360
  AttacherType = Attacher::AttachEngine3D
  FirstAngle = 0
  Height = 33
  Placement = pos=(-74.6,-105.8,63) rot=(0,1,0;1.5708rad)
  Radius = 2
  SecondAngle = 0
FEATURE [Part::Cylinder] Cylinder349  label="円柱349"
  Angle = 360
  AttacherType = Attacher::AttachEngine3D
  FirstAngle = 0
  Height = 30
  Placement = pos=(-71.6,-56.2,73) rot=(0,1,0;1.5708rad)
  Radius = 2
  SecondAngle = 0
FEATURE [Part::Cylinder] Cylinder350  label="円柱350"
  Angle = 360
  AttacherType = Attacher::AttachEngine3D
  FirstAngle = 0
  Height = 33
  Placement = pos=(-74.6,-56.2,63) rot=(0,1,0;1.5708rad)
  Radius = 2
  SecondAngle = 0
FEATURE [Part::MultiFuse] Fusion348
  Refine = true
  Shapes = -> [Common,Box444]
FEATURE [Part::MultiFuse] Fusion349
  Placement = pos=(-153.6,-8,61) rot=(0,0,1;0rad)
  Shapes = -> [Box447,Box446]
FEATURE [Part::MultiFuse] Fusion350
  Placement = pos=(0,0,-3) rot=(0,0,1;0rad)
  Shapes = -> [Fusion349,CycloidGear028]
FEATURE [Part::Cut] Cut364
  Base = -> Fusion350
  Tool = -> Cylinder347
FEATURE [Part::Cut] Cut365
  Base = -> Cut364
  Tool = -> Cylinder348
FEATURE [Part::Cut] Cut366
  Base = -> Cut365
  Tool = -> Cylinder349
FEATURE [Part::Cut] Cut367  label="Motor Arm001"
  Base = -> Cut366
  Placement = pos=(4.7,2,4) rot=(0,0,1;0rad)
  Tool = -> Cylinder350
FEATURE [Part::Cut] Cut368
  Base = -> Cut367
  Refine = true
  Tool = -> Box445
FEATURE [Part::Cut] Cut369  label="Servo horn Arm Motor"
  Base = -> Fusion348
  Refine = true
  Tool = -> Cut368
FEATURE [Part::Feature] Part__Feature024  label="SG09 (NoRescueTime)"
  Placement = pos=(0.8,-48,140.3) rot=(0,0.707107,-0.707107;3.14159rad)
  shape: bbox 13.64 x 30.4 x 32.4 mm, 869 faces (baked)
FEATURE [Part::Feature] Part__Feature025  label="Arm (No rescue time)"
  Placement = pos=(0,-178,144) rot=(1,0,0;3.14159rad)
  shape: bbox 77.54 x 115.5 x 104.3 mm, 80 faces (baked)
FEATURE [App::Part] robot___robcup_ber_5__a004  label="Rescue Arm (No rescue time)"
  Group = -> [Part__Feature024,Part__Feature025]
  Origin = -> Origin004
FEATURE [Part::Feature] Part__Feature026  label="SG90 (RescueTime)"
  Placement = pos=(0.8,-130,3.9) rot=(0,0.707107,0.707107;3.14159rad)
  shape: bbox 13.64 x 30.4 x 32.4 mm, 869 faces (baked)
FEATURE [Part::Feature] Part__Feature027  label="Arm (rescue time)"
  shape: bbox 77.54 x 115.5 x 104.3 mm, 80 faces (baked)
FEATURE [App::Part] robot___robcup_ber_5__a005  label="Rescue Arm (Rescue time)"
  Group = -> [Part__Feature026,Part__Feature027]
  Origin = -> Origin005
FEATURE [Part::Cylinder] Cylinder  label="円柱"
  Angle = 360
  AttacherType = Attacher::AttachEngine3D
  FirstAngle = 0
  Height = 14.5
  Radius = 2
  SecondAngle = 0
FEATURE [Part::Cylinder] Cylinder001  label="円柱001"
  Angle = 360
  AttacherType = Attacher::AttachEngine3D
  FirstAngle = 0
  Height = 14.5
  Radius = 4
  SecondAngle = 0
FEATURE [Part::Cut] Cut  label="spacer1"
  Base = -> Cylinder001
  Placement = pos=(-57,71,49) rot=(0,0,1;0rad)
  Refine = true
  Tool = -> Cylinder
FEATURE [Part::Cylinder] Cylinder351  label="円柱351"
  Angle = 360
  AttacherType = Attacher::AttachEngine3D
  FirstAngle = 0
  Height = 14.5
  Radius = 2
  SecondAngle = 0
FEATURE [Part::Cylinder] Cylinder352  label="円柱352"
  Angle = 360
  AttacherType = Attacher::AttachEngine3D
  FirstAngle = 0
  Height = 14.5
  Radius = 4
  SecondAngle = 0
FEATURE [Part::Cut] Cut370  label="spacer2"
  Base = -> Cylinder352
  Placement = pos=(-57,-27,49) rot=(0,0,1;0rad)
  Refine = true
  Tool = -> Cylinder351
FEATURE [Part::Feature] Part__Feature174  label="R_Axial_DIN0204_L3.6mm_D1.6mm_P7.62mm_Horizontal"
  Placement = pos=(180.38,-120.5,1.595) rot=(0,0,1;0rad)
  shape: bbox 8.285 x 1.732 x 4.666 mm, 17 faces (baked)
FEATURE [Part::Feature] Part__Feature175  label="R_Axial_DIN0204_L3.6mm_D1.6mm_P7.62mm_Horizontal001"
  Placement = pos=(168.38,-118.5,1.595) rot=(0,0,1;0rad)
  shape: bbox 8.285 x 1.732 x 4.666 mm, 17 faces (baked)
FEATURE [Part::Feature] Part__Feature176  label="R_Axial_DIN0204_L3.6mm_D1.6mm_P7.62mm_Horizontal002"
  Placement = pos=(180.38,-115,1.595) rot=(0,0,1;0rad)
  shape: bbox 8.285 x 1.732 x 4.666 mm, 17 faces (baked)
FEATURE [Part::Feature] Part__Feature177  label="robocup2025_kicad_data (1)_copper"
  shape: bbox 71.03 x 69.3 x 1.58 mm, 120 faces, 30 solids (baked)
FEATURE [Part::Feature] Part__Feature178  label="robocup2025_kicad_data (1)_pad"
  shape: bbox 79.83 x 81.91 x 1.59 mm, 1418 faces, 285 solids (baked)
FEATURE [Part::Feature] Part__Feature179  label="robocup2025_kicad_data (1)_via"
  shape: bbox 70.73 x 69 x 1.58 mm, 60 faces, 15 solids (baked)
FEATURE [Part::Feature] Part__Feature180  label="robocup2025_kicad_data (1)_silkscreen"
  shape: bbox 84.09 x 92.95 x 2e-07 mm, 244 faces, 0 solids (baked)
FEATURE [Part::Feature] Part__Feature181  label="robocup2025_kicad_data (1)_silkscreen001"
  shape: bbox 12.41 x 2.689 x 2e-07 mm, 22 faces, 0 solids (baked)
FEATURE [Part::Feature] Part__Feature182  label="robocup2025_kicad_data (1)_PCB"
  shape: bbox 88.11 x 96.95 x 1.51 mm, 117 faces (baked)
FEATURE [App::Part] robocup2025_kicad_data__1__1  label="robocup2025_kicad_data (1) 1"
  Group = -> [Part__Feature174,Part__Feature175,Part__Feature176,Part__Feature177,Part__Feature178,Part__Feature179,Part__Feature180,Part__Feature181,Part__Feature182]
  Origin = -> Origin048
  Placement = pos=(141.8,-59,59) rot=(0,0,1;3.14159rad)
FEATURE [Part::Cylinder] Cylinder353  label="円柱353"
  Angle = 360
  AttacherType = Attacher::AttachEngine3D
  FirstAngle = 0
  Height = 2
  Radius = 2
  SecondAngle = 0
FEATURE [Part::Cylinder] Cylinder354  label="円柱354"
  Angle = 360
  AttacherType = Attacher::AttachEngine3D
  FirstAngle = 0
  Height = 2
  Radius = 4
  SecondAngle = 0
FEATURE [Part::Cut] Cut371  label="spacer3"
  Base = -> Cylinder354
  Placement = pos=(-47,-19,57) rot=(0,0,1;0rad)
  Refine = true
  Tool = -> Cylinder353
FEATURE [Part::Cylinder] Cylinder355  label="円柱355"
  Angle = 360
  AttacherType = Attacher::AttachEngine3D
  FirstAngle = 0
  Height = 2
  Radius = 2
  SecondAngle = 0
FEATURE [Part::Cylinder] Cylinder356  label="円柱356"
  Angle = 360
  AttacherType = Attacher::AttachEngine3D
  FirstAngle = 0
  Height = 2
  Radius = 4
  SecondAngle = 0
FEATURE [Part::Cut] Cut372  label="spacer4"
  Base = -> Cylinder356
  Placement = pos=(-47,71,57) rot=(0,0,1;0rad)
  Refine = true
  Tool = -> Cylinder355
FEATURE [Part::Cylinder] Cylinder357  label="円柱357"
  Angle = 360
  AttacherType = Attacher::AttachEngine3D
  FirstAngle = 0
  Height = 2
  Radius = 2
  SecondAngle = 0
FEATURE [Part::Cylinder] Cylinder358  label="円柱358"
  Angle = 360
  AttacherType = Attacher::AttachEngine3D
  FirstAngle = 0
  Height = 2
  Radius = 4
  SecondAngle = 0
FEATURE [Part::Cut] Cut373  label="spacer5"
  Base = -> Cylinder358
  Placement = pos=(33,-19,57) rot=(0,0,1;0rad)
  Refine = true
  Tool = -> Cylinder357
FEATURE [Part::Cylinder] Cylinder359  label="円柱359"
  Angle = 360
  AttacherType = Attacher::AttachEngine3D
  FirstAngle = 0
  Height = 2
  Radius = 2
  SecondAngle = 0
FEATURE [Part::Cylinder] Cylinder360  label="円柱360"
  Angle = 360
  AttacherType = Attacher::AttachEngine3D
  FirstAngle = 0
  Height = 2
  Radius = 4
  SecondAngle = 0
FEATURE [Part::Cut] Cut374  label="spacer6"
  Base = -> Cylinder360
  Placement = pos=(33,71,57) rot=(0,0,1;0rad)
  Refine = true
  Tool = -> Cylinder359
FEATURE [Part::Feature] Part__Feature183  label="Main-PCB"
  Placement = pos=(0,0,0) rot=(-1,0,0;1.5708rad)
  shape: bbox 28.1 x 1.6 x 48.26 mm, 82 faces (baked)
FEATURE [Part::Feature] Part__Feature184  label="zl201-19_p2-54_l48-3_w2-54_h8-9"
  Placement = pos=(-12.78,-0.25,22.86) rot=(0.57735,-0.57735,0.57735;2.0944rad)
  shape: bbox 2.54 x 11.94 x 48.26 mm, 608 faces, 38 solids (baked)
FEATURE [Part::Feature] Part__Feature185  label="zl201-19_p2-54_l48-3_w2-54_h8-010"
  Placement = pos=(12.78,-0.25,-22.86) rot=(0.57735,0.57735,-0.57735;2.0944rad)
  shape: bbox 2.54 x 11.94 x 48.26 mm, 608 faces, 38 solids (baked)
FEATURE [Part::Feature] Part__Feature186  label="Soldering-Contacts"
  Placement = pos=(0,1.6,0) rot=(-1,0,0;1.5708rad)
  shape: bbox 27.34 x 2 x 47.52 mm, 836 faces, 76 solids (baked)
FEATURE [Part::Feature] Part__Feature187  label="ab2_usb_micro_smd.wrl"
  Placement = pos=(0,2.585,24.73) rot=(-1,0,0;1.5708rad)
  shape: bbox 8 x 3.57 x 5.6 mm, 862 faces (baked)
FEATURE [Part::Feature] Part__Feature188  label="ESP32-chip"
  Placement = pos=(0,1.6,0) rot=(-1,0,0;1.5708rad)
  shape: bbox 18 x 3.2 x 25.8 mm, 342 faces, 2 solids (baked)
FEATURE [Part::Feature] Part__Feature189  label="3x4x2mm_tact_button"
  Placement = pos=(9.13466,1.6,18.3459) rot=(0,-1,0;1.5708rad)
  shape: bbox 2.9 x 2 x 5 mm, 81 faces (baked)
FEATURE [Part::Feature] Part__Feature190  label="3x4x2mm_tact_button001"
  Placement = pos=(-7.70534,1.6,18.3459) rot=(0,-1,0;1.5708rad)
  shape: bbox 2.9 x 2 x 5 mm, 81 faces (baked)
FEATURE [App::Part] ESP_WROOM_32D_Assembly  label="ESP-WROOM-32D-Assembly"
  Group = -> [Part__Feature183,Part__Feature184,Part__Feature185,Part__Feature186,Part__Feature187,Part__Feature188,Part__Feature189,Part__Feature190]
  Origin = -> Origin049
  Placement = pos=(14,23.4,63) rot=(0,0.707107,0.707107;3.14159rad)
FEATURE [Part::Feature] Part__Feature191  label="Ultrasonic Sensor Front"
  Placement = pos=(-33.9,-95,7.2) rot=(0,-0.707107,0.707107;3.14159rad)
  shape: bbox 45 x 18 x 26.6 mm, 955 faces, 4 solids (baked)
FEATURE [Part::Feature] Part__Feature192  label="Ultrasonic Sensor Right"
  Placement = pos=(-93.5,-63,60.2) rot=(-0.57735,-0.57735,0.57735;2.0944rad)
  shape: bbox 18 x 45 x 26.6 mm, 955 faces, 4 solids (baked)
  expr: .Placement.Base.x = -93.5 mm
FEATURE [Part::Feature] Part__Feature193  label="Ultrasonic Sensor Left"
  Placement = pos=(25.7,-63,60.2) rot=(-0.57735,0.57735,-0.57735;2.0944rad)
  shape: bbox 18 x 45 x 26.6 mm, 955 faces, 4 solids (baked)
FEATURE [Part::Feature] Part__Feature194  label="/PWDN"
  shape: bbox 0.63 x 0.22 x 0.03048 mm, 6 faces (baked)
FEATURE [Part::Feature] Part__Feature195  label="1"
  shape: bbox 1 x 0.95 x 0.03048 mm, 6 faces (baked)
FEATURE [Part::Feature] Part__Feature196  label="1001"
  shape: bbox 0.95 x 1 x 0.03048 mm, 6 faces (baked)
FEATURE [Part::Feature] Part__Feature197  label="1002"
  shape: bbox 0.57 x 0.58 x 0.03048 mm, 6 faces (baked)
FEATURE [Part::Feature] Part__Feature198  label="1003"
  shape: bbox 0.57 x 0.58 x 0.03048 mm, 6 faces (baked)
FEATURE [Part::Feature] Part__Feature199  label="1004"
  shape: bbox 0.58 x 0.57 x 0.03048 mm, 6 faces (baked)
FEATURE [Part::Feature] Part__Feature200  label="1005"
  shape: bbox 0.57 x 0.58 x 0.03048 mm, 6 faces (baked)
FEATURE [Part::Feature] Part__Feature201  label="1006"
  shape: bbox 0.57 x 0.58 x 0.03048 mm, 6 faces (baked)
FEATURE [Part::Feature] Part__Feature202  label="1007"
  shape: bbox 0.58 x 0.57 x 0.03048 mm, 6 faces (baked)
FEATURE [Part::Feature] Part__Feature203  label="1008"
  shape: bbox 0.45 x 0.275 x 0.03048 mm, 6 faces (baked)
FEATURE [Part::Feature] Part__Feature204  label="1009"
  shape: bbox 0.57 x 0.58 x 0.03048 mm, 6 faces (baked)
FEATURE [Part::Feature] Part__Feature205  label="1010"
  shape: bbox 0.275 x 0.45 x 0.03048 mm, 6 faces (baked)
FEATURE [Part::Feature] Part__Feature206  label="1011"
  shape: bbox 0.57 x 0.58 x 0.03048 mm, 6 faces (baked)
FEATURE [Part::Feature] Part__Feature207  label="1012"
  shape: bbox 0.58 x 0.57 x 0.03048 mm, 6 faces (baked)
FEATURE [Part::Feature] Part__Feature208  label="1013"
  shape: bbox 0.58 x 0.57 x 0.03048 mm, 6 faces (baked)
FEATURE [Part::Feature] Part__Feature209  label="1014"
  shape: bbox 0.57 x 0.58 x 0.03048 mm, 6 faces (baked)
FEATURE [Part::Feature] Part__Feature210  label="1015"
  shape: bbox 1.15 x 1.45 x 0.03048 mm, 6 faces (baked)
FEATURE [Part::Feature] Part__Feature211  label="1016"
  shape: bbox 0.57 x 0.58 x 0.03048 mm, 6 faces (baked)
FEATURE [Part::Feature] Part__Feature212  label="1017"
  shape: bbox 0.85 x 0.9 x 0.03048 mm, 6 faces (baked)
FEATURE [Part::Feature] Part__Feature213  label="1018"
  shape: bbox 0.58 x 0.57 x 0.03048 mm, 6 faces (baked)
FEATURE [Part::Feature] Part__Feature214  label="1019"
  shape: bbox 0.95 x 2.3 x 0.03048 mm, 6 faces (baked)
FEATURE [Part::Feature] Part__Feature215  label="1020"
  shape: bbox 2 x 0.5999 x 0.03048 mm, 6 faces (baked)
FEATURE [Part::Feature] Part__Feature216  label="1021"
  shape: bbox 0.57 x 0.58 x 0.03048 mm, 6 faces (baked)
FEATURE [Part::Feature] Part__Feature217  label="1022"
  shape: bbox 0.57 x 0.58 x 0.03048 mm, 6 faces (baked)
FEATURE [Part::Feature] Part__Feature218  label="1023"
  shape: bbox 0.57 x 0.58 x 0.03048 mm, 6 faces (baked)
FEATURE [Part::Feature] Part__Feature219  label="1024"
  shape: bbox 0.58 x 0.57 x 0.03048 mm, 6 faces (baked)
FEATURE [Part::Feature] Part__Feature220  label="10"
  shape: bbox 2 x 0.5999 x 0.03048 mm, 6 faces (baked)
FEATURE [Part::Feature] Part__Feature221  label="11"
  shape: bbox 2 x 0.5999 x 0.03048 mm, 6 faces (baked)
FEATURE [Part::Feature] Part__Feature222  label="12"
  shape: bbox 2 x 0.5999 x 0.03048 mm, 6 faces (baked)
FEATURE [Part::Feature] Part__Feature223  label="13"
  shape: bbox 2 x 0.5999 x 0.03048 mm, 6 faces (baked)
FEATURE [Part::Feature] Part__Feature224  label="14"
  shape: bbox 2 x 0.5999 x 0.03048 mm, 6 faces (baked)
FEATURE [Part::Feature] Part__Feature225  label="15"
  shape: bbox 2 x 0.5999 x 0.03048 mm, 6 faces (baked)
FEATURE [Part::Feature] Part__Feature226  label="2"
  shape: bbox 0.58 x 0.57 x 0.03048 mm, 6 faces (baked)
FEATURE [Part::Feature] Part__Feature227  label="2001"
  shape: bbox 1.15 x 1.45 x 0.03048 mm, 6 faces (baked)
FEATURE [Part::Feature] Part__Feature228  label="2002"
  shape: bbox 0.85 x 0.9 x 0.03048 mm, 6 faces (baked)
FEATURE [Part::Feature] Part__Feature229  label="2003"
  shape: bbox 0.95 x 2.3 x 0.03048 mm, 6 faces (baked)
FEATURE [Part::Feature] Part__Feature230  label="2004"
  shape: bbox 2 x 0.5999 x 0.03048 mm, 6 faces (baked)
FEATURE [Part::Feature] Part__Feature231  label="2005"
  shape: bbox 0.58 x 0.57 x 0.03048 mm, 6 faces (baked)
FEATURE [Part::Feature] Part__Feature232  label="2006"
  shape: bbox 0.95 x 1 x 0.03048 mm, 6 faces (baked)
FEATURE [Part::Feature] Part__Feature233  label="2007"
  shape: bbox 0.58 x 0.57 x 0.03048 mm, 6 faces (baked)
FEATURE [Part::Feature] Part__Feature234  label="2008"
  shape: bbox 0.57 x 0.58 x 0.03048 mm, 6 faces (baked)
FEATURE [Part::Feature] Part__Feature235  label="2009"
  shape: bbox 0.57 x 0.58 x 0.03048 mm, 6 faces (baked)
FEATURE [Part::Feature] Part__Feature236  label="2010"
  shape: bbox 0.57 x 0.58 x 0.03048 mm, 6 faces (baked)
FEATURE [Part::Feature] Part__Feature237  label="2011"
  shape: bbox 0.57 x 0.58 x 0.03048 mm, 6 faces (baked)
FEATURE [Part::Feature] Part__Feature238  label="2012"
  shape: bbox 0.58 x 0.57 x 0.03048 mm, 6 faces (baked)
FEATURE [Part::Feature] Part__Feature239  label="2013"
  shape: bbox 0.58 x 0.57 x 0.03048 mm, 6 faces (baked)
FEATURE [Part::Feature] Part__Feature240  label="2014"
  shape: bbox 0.57 x 0.58 x 0.03048 mm, 6 faces (baked)
FEATURE [Part::Feature] Part__Feature241  label="2015"
  shape: bbox 0.57 x 0.58 x 0.03048 mm, 6 faces (baked)
FEATURE [Part::Feature] Part__Feature242  label="2016"
  shape: bbox 0.58 x 0.57 x 0.03048 mm, 6 faces (baked)
FEATURE [Part::Feature] Part__Feature243  label="2017"
  shape: bbox 0.57 x 0.58 x 0.03048 mm, 6 faces (baked)
FEATURE [Part::Feature] Part__Feature244  label="2018"
  shape: bbox 0.57 x 0.58 x 0.03048 mm, 6 faces (baked)
FEATURE [Part::Feature] Part__Feature245  label="2019"
  shape: bbox 1 x 0.95 x 0.03048 mm, 6 faces (baked)
FEATURE [Part::Feature] Part__Feature246  label="2020"
  shape: bbox 0.57 x 0.58 x 0.03048 mm, 6 faces (baked)
FEATURE [Part::Feature] Part__Feature247  label="2021"
  shape: bbox 0.57 x 0.58 x 0.03048 mm, 6 faces (baked)
FEATURE [Part::Feature] Part__Feature248  label="2022"
  shape: bbox 0.45 x 0.275 x 0.03048 mm, 6 faces (baked)
FEATURE [Part::Feature] Part__Feature249  label="2023"
  shape: bbox 0.57 x 0.58 x 0.03048 mm, 6 faces (baked)
FEATURE [Part::Feature] Part__Feature250  label="2024"
  shape: bbox 0.275 x 0.45 x 0.03048 mm, 6 faces (baked)
FEATURE [Part::Feature] Part__Feature251  label="3"
  shape: bbox 2 x 0.5999 x 0.03048 mm, 6 faces (baked)
FEATURE [Part::Feature] Part__Feature252  label="4"
  shape: bbox 2 x 0.5999 x 0.03048 mm, 6 faces (baked)
FEATURE [Part::Feature] Part__Feature253  label="5"
  shape: bbox 2 x 0.5999 x 0.03048 mm, 6 faces (baked)
FEATURE [Part::Feature] Part__Feature254  label="6"
  shape: bbox 2 x 0.5999 x 0.03048 mm, 6 faces (baked)
FEATURE [Part::Feature] Part__Feature255  label="7"
  shape: bbox 2 x 0.5999 x 0.03048 mm, 6 faces (baked)
FEATURE [Part::Feature] Part__Feature256  label="8"
  shape: bbox 2 x 0.5999 x 0.03048 mm, 6 faces (baked)
FEATURE [Part::Feature] Part__Feature257  label="9"
  shape: bbox 2 x 0.5999 x 0.03048 mm, 6 faces (baked)
FEATURE [Part::Feature] Part__Feature258  label="AFVDD"
  shape: bbox 0.63 x 0.22 x 0.03048 mm, 6 faces (baked)
FEATURE [Part::Feature] Part__Feature259  label="AGND"
  shape: bbox 0.63 x 0.22 x 0.03048 mm, 6 faces (baked)
FEATURE [Part::Feature] Part__Feature260  label="D2"
  shape: bbox 0.3 x 0.5 x 0.03048 mm, 6 faces (baked)
FEATURE [Part::Feature] Part__Feature261  label="D003"
  shape: bbox 0.3 x 0.5 x 0.03048 mm, 6 faces (baked)
FEATURE [Part::Feature] Part__Feature262  label="DGND1"
  shape: bbox 0.63 x 0.22 x 0.03048 mm, 6 faces (baked)
FEATURE [Part::Feature] Part__Feature263  label="DGND2"
  shape: bbox 0.63 x 0.22 x 0.03048 mm, 6 faces (baked)
FEATURE [Part::Feature] Part__Feature264  label="DGND3"
  shape: bbox 0.63 x 0.22 x 0.03048 mm, 6 faces (baked)
FEATURE [Part::Feature] Part__Feature265  label="DGND4"
  shape: bbox 0.63 x 0.22 x 0.03048 mm, 6 faces (baked)
FEATURE [Part::Feature] Part__Feature266  label="DGND5"
  shape: bbox 0.63 x 0.22 x 0.03048 mm, 6 faces (baked)
FEATURE [Part::Feature] Part__Feature267  label="DGND6"
  shape: bbox 0.63 x 0.22 x 0.03048 mm, 6 faces (baked)
FEATURE [Part::Feature] Part__Feature268  label="DGND7"
  shape: bbox 0.63 x 0.22 x 0.03048 mm, 6 faces (baked)
FEATURE [Part::Feature] Part__Feature269  label="DGND8"
  shape: bbox 0.63 x 0.22 x 0.03048 mm, 6 faces (baked)
FEATURE [Part::Feature] Part__Feature270  label="DGND9"
  shape: bbox 0.63 x 0.22 x 0.03048 mm, 6 faces (baked)
FEATURE [Part::Feature] Part__Feature271  label="DVDD"
  shape: bbox 0.63 x 0.22 x 0.03048 mm, 6 faces (baked)
FEATURE [Part::Feature] Part__Feature272  label="DVDD/GPIO"
  shape: bbox 0.63 x 0.22 x 0.03048 mm, 6 faces (baked)
FEATURE [Part::Feature] Part__Feature273  label="EN"
  shape: bbox 1.1 x 0.6 x 0.03048 mm, 6 faces (baked)
FEATURE [Part::Feature] Part__Feature274  label="EN001"
  shape: bbox 1.1 x 0.6 x 0.03048 mm, 6 faces (baked)
FEATURE [Part::Feature] Part__Feature275  label="EN002"
  shape: bbox 1.1 x 0.6 x 0.03048 mm, 6 faces (baked)
FEATURE [Part::Feature] Part__Feature276  label="EXP_PAD"
  shape: bbox 1.6 x 1.4 x 0.03048 mm, 6 faces (baked)
FEATURE [Part::Feature] Part__Feature277  label="FB"
  shape: bbox 1.1 x 0.6 x 0.03048 mm, 6 faces (baked)
FEATURE [Part::Feature] Part__Feature278  label="G2"
  shape: bbox 0.3 x 0.5 x 0.03048 mm, 6 faces (baked)
FEATURE [Part::Feature] Part__Feature279  label="G003"
  shape: bbox 0.3 x 0.5 x 0.03048 mm, 6 faces (baked)
FEATURE [Part::Feature] Part__Feature280  label="GND"
  shape: bbox 0.63 x 0.22 x 0.03048 mm, 6 faces (baked)
FEATURE [Part::Feature] Part__Feature281  label="GND001"
  shape: bbox 1.1 x 0.6 x 0.03048 mm, 6 faces (baked)
FEATURE [Part::Feature] Part__Feature282  label="GND002"
  shape: bbox 0.8999 x 0.8001 x 0.03048 mm, 6 faces (baked)
FEATURE [Part::Feature] Part__Feature283  label="GND003"
  shape: bbox 1.1 x 0.6 x 0.03048 mm, 6 faces (baked)
FEATURE [Part::Feature] Part__Feature284  label="GND004"
  shape: bbox 1.5 x 0.6 x 0.03048 mm, 6 faces (baked)
FEATURE [Part::Feature] Part__Feature285  label="GND005"
  shape: bbox 0.3 x 0.85 x 0.03048 mm, 6 faces (baked)
FEATURE [Part::Feature] Part__Feature286  label="GND006"
  shape: bbox 1.1 x 0.6 x 0.03048 mm, 6 faces (baked)
FEATURE [Part::Feature] Part__Feature287  label="IN"
  shape: bbox 1.1 x 0.6 x 0.03048 mm, 6 faces (baked)
FEATURE [Part::Feature] Part__Feature288  label="IN001"
  shape: bbox 1.1 x 0.6 x 0.03048 mm, 6 faces (baked)
FEATURE [Part::Feature] Part__Feature289  label="LX"
  shape: bbox 1.1 x 0.6 x 0.03048 mm, 6 faces (baked)
FEATURE [Part::Feature] Part__Feature290  label="MCKN"
  shape: bbox 0.63 x 0.22 x 0.03048 mm, 6 faces (baked)
FEATURE [Part::Feature] Part__Feature291  label="MCKP"
  shape: bbox 0.63 x 0.22 x 0.03048 mm, 6 faces (baked)
FEATURE [Part::Feature] Part__Feature292  label="MCLK"
  shape: bbox 0.63 x 0.22 x 0.03048 mm, 6 faces (baked)
FEATURE [Part::Feature] Part__Feature293  label="MD0N"
  shape: bbox 0.63 x 0.22 x 0.03048 mm, 6 faces (baked)
FEATURE [Part::Feature] Part__Feature294  label="MD0P"
  shape: bbox 0.63 x 0.22 x 0.03048 mm, 6 faces (baked)
FEATURE [Part::Feature] Part__Feature295  label="MD1N"
  shape: bbox 0.63 x 0.22 x 0.03048 mm, 6 faces (baked)
FEATURE [Part::Feature] Part__Feature296  label="MD1P"
  shape: bbox 0.63 x 0.22 x 0.03048 mm, 6 faces (baked)
FEATURE [Part::Feature] Part__Feature297  label="MECHANICAL PIN"
  shape: bbox 1.5 x 1.5 x 0.03048 mm, 4 faces (baked)
FEATURE [Part::Feature] Part__Feature298  label="MECHANICAL PIN001"
  shape: bbox 3.6 x 2.68 x 0.03048 mm, 6 faces (baked)
FEATURE [Part::Feature] Part__Feature299  label="MECHANICAL PIN002"
  shape: bbox 3.6 x 2.68 x 0.03048 mm, 6 faces (baked)
FEATURE [Part::Feature] Part__Feature300  label="MECHANICAL PIN003"
  shape: bbox 4.2 x 0.7 x 0.03048 mm, 6 faces (baked)
FEATURE [Part::Feature] Part__Feature301  label="MECHANICAL PIN004"
  shape: bbox 4.2 x 0.7 x 0.03048 mm, 6 faces (baked)
FEATURE [Part::Feature] Part__Feature302  label="MECHANICAL PIN005"
  shape: bbox 1.5 x 1.5 x 0.03048 mm, 4 faces (baked)
FEATURE [Part::Feature] Part__Feature303  label="NC"
  shape: bbox 1.1 x 0.6 x 0.03048 mm, 6 faces (baked)
FEATURE [Part::Feature] Part__Feature304  label="NC001"
  shape: bbox 1.1 x 0.6 x 0.03048 mm, 6 faces (baked)
FEATURE [Part::Feature] Part__Feature305  label="NC1"
  shape: bbox 1.5 x 0.6 x 0.03048 mm, 6 faces (baked)
FEATURE [Part::Feature] Part__Feature306  label="NC002"
  shape: bbox 0.63 x 0.22 x 0.03048 mm, 6 faces (baked)
FEATURE [Part::Feature] Part__Feature307  label="NC003"
  shape: bbox 0.3 x 0.85 x 0.03048 mm, 6 faces (baked)
FEATURE [Part::Feature] Part__Feature308  label="NC2"
  shape: bbox 1.5 x 0.6 x 0.03048 mm, 6 faces (baked)
FEATURE [Part::Feature] Part__Feature309  label="NC004"
  shape: bbox 0.63 x 0.22 x 0.03048 mm, 6 faces (baked)
FEATURE [Part::Feature] Part__Feature310  label="NC005"
  shape: bbox 0.3 x 0.85 x 0.03048 mm, 6 faces (baked)
FEATURE [Part::Feature] Part__Feature311  label="NC3"
  shape: bbox 0.3 x 0.85 x 0.03048 mm, 6 faces (baked)
FEATURE [Part::Feature] Part__Feature312  label="NC006"
  shape: bbox 1.5 x 0.6 x 0.03048 mm, 6 faces (baked)
FEATURE [Part::Feature] Part__Feature313  label="NC4"
  shape: bbox 1.5 x 0.6 x 0.03048 mm, 6 faces (baked)
FEATURE [Part::Feature] Part__Feature314  label="NC6"
  shape: bbox 0.63 x 0.22 x 0.03048 mm, 6 faces (baked)
FEATURE [Part::Feature] Part__Feature315  label="NC7"
  shape: bbox 0.63 x 0.22 x 0.03048 mm, 6 faces (baked)
FEATURE [Part::Feature] Part__Feature316  label="NC007"
  shape: bbox 0.3 x 0.85 x 0.03048 mm, 6 faces (baked)
FEATURE [Part::Feature] Part__Feature317  label="OE"
  shape: bbox 0.8999 x 0.8001 x 0.03048 mm, 6 faces (baked)
FEATURE [Part::Feature] Part__Feature318  label="OUT"
  shape: bbox 1.1 x 0.6 x 0.03048 mm, 6 faces (baked)
FEATURE [Part::Feature] Part__Feature319  label="OUT001"
  shape: bbox 1.1 x 0.6 x 0.03048 mm, 6 faces (baked)
FEATURE [Part::Feature] Part__Feature320  label="OUTPUT"
  shape: bbox 0.8999 x 0.8001 x 0.03048 mm, 6 faces (baked)
FEATURE [Part::Feature] Part__Feature321  label="P1"
  shape: bbox 0.7 x 0.28 x 0.03048 mm, 6 faces (baked)
FEATURE [Part::Feature] Part__Feature322  label="P002"
  shape: bbox 0.7 x 0.28 x 0.03048 mm, 6 faces (baked)
FEATURE [Part::Feature] Part__Feature323  label="P003"
  shape: bbox 0.7 x 0.28 x 0.03048 mm, 6 faces (baked)
FEATURE [Part::Feature] Part__Feature324  label="P2"
  shape: bbox 0.7 x 0.28 x 0.03048 mm, 6 faces (baked)
FEATURE [Part::Feature] Part__Feature325  label="P004"
  shape: bbox 0.7 x 0.28 x 0.03048 mm, 6 faces (baked)
FEATURE [Part::Feature] Part__Feature326  label="P005"
  shape: bbox 0.7 x 0.28 x 0.03048 mm, 6 faces (baked)
FEATURE [Part::Feature] Part__Feature327  label="P3"
  shape: bbox 0.7 x 0.28 x 0.03048 mm, 6 faces (baked)
FEATURE [Part::Feature] Part__Feature328  label="P006"
  shape: bbox 0.7 x 0.28 x 0.03048 mm, 6 faces (baked)
FEATURE [Part::Feature] Part__Feature329  label="P007"
  shape: bbox 0.7 x 0.28 x 0.03048 mm, 6 faces (baked)
FEATURE [Part::Feature] Part__Feature330  label="P4"
  shape: bbox 0.7 x 0.28 x 0.03048 mm, 6 faces (baked)
FEATURE [Part::Feature] Part__Feature331  label="P008"
  shape: bbox 0.7 x 0.28 x 0.03048 mm, 6 faces (baked)
FEATURE [Part::Feature] Part__Feature332  label="P009"
  shape: bbox 0.7 x 0.28 x 0.03048 mm, 6 faces (baked)
FEATURE [Part::Feature] Part__Feature333  label="PG"
  shape: bbox 1.1 x 0.6 x 0.03048 mm, 6 faces (baked)
FEATURE [Part::Feature] Part__Feature334  label="S2"
  shape: bbox 0.3 x 0.5 x 0.03048 mm, 6 faces (baked)
FEATURE [Part::Feature] Part__Feature335  label="S003"
  shape: bbox 0.3 x 0.5 x 0.03048 mm, 6 faces (baked)
FEATURE [Part::Feature] Part__Feature336  label="SCL"
  shape: bbox 1.5 x 0.6 x 0.03048 mm, 6 faces (baked)
FEATURE [Part::Feature] Part__Feature337  label="SCL001"
  shape: bbox 0.3 x 0.85 x 0.03048 mm, 6 faces (baked)
FEATURE [Part::Feature] Part__Feature338  label="SCL002"
  shape: bbox 0.63 x 0.22 x 0.03048 mm, 6 faces (baked)
FEATURE [Part::Feature] Part__Feature339  label="SDA"
  shape: bbox 0.63 x 0.22 x 0.03048 mm, 6 faces (baked)
FEATURE [Part::Feature] Part__Feature340  label="SDA001"
  shape: bbox 0.3 x 0.85 x 0.03048 mm, 6 faces (baked)
FEATURE [Part::Feature] Part__Feature341  label="SDA002"
  shape: bbox 1.5 x 0.6 x 0.03048 mm, 6 faces (baked)
FEATURE [Part::Feature] Part__Feature342  label="VA2V8"
  shape: bbox 0.63 x 0.22 x 0.03048 mm, 6 faces (baked)
FEATURE [Part::Feature] Part__Feature343  label="VCC"
  shape: bbox 0.3 x 0.85 x 0.03048 mm, 6 faces (baked)
FEATURE [Part::Feature] Part__Feature344  label="VCC001"
  shape: bbox 1.5 x 0.6 x 0.03048 mm, 6 faces (baked)
FEATURE [Part::Feature] Part__Feature345  label="VDD"
  shape: bbox 0.8999 x 0.8001 x 0.03048 mm, 6 faces (baked)
FEATURE [Part::Feature] Part__Feature346  label="VIN"
  shape: bbox 1.1 x 0.6 x 0.03048 mm, 6 faces (baked)
FEATURE [Part::Feature] Part__Feature347  label="VO1V8"
  shape: bbox 0.63 x 0.22 x 0.03048 mm, 6 faces (baked)
FEATURE [App::Part] Pins
  Group = -> [Part__Feature194,Part__Feature195,Part__Feature196,Part__Feature197,Part__Feature198,Part__Feature199,Part__Feature200,Part__Feature201,Part__Feature202,Part__Feature203,Part__Feature204,Part__Feature205,Part__Feature206,Part__Feature207,Part__Feature208,Part__Feature209,Part__Feature210,Part__Feature211,Part__Feature212,Part__Feature213,Part__Feature214,Part__Feature215,Part__Feature216,+131 more]
  Origin = -> Origin050
FEATURE [Part::Feature] Part__Feature348  label="SILKSCREEN_TOP"
  shape: bbox 18.45 x 22.65 x 0.0127 mm, 5790 faces, 166 solids (baked)
FEATURE [Part::Feature] Part__Feature349  label="PASTEMASK_TOP"
  shape: bbox 21.25 x 22.68 x 0.0001002 mm, 726 faces, 121 solids (baked)
FEATURE [Part::Feature] Part__Feature350  label="SOLDERMASK_TOP"
  shape: bbox 23.86 x 25 x 0.0127 mm, 504 faces (baked)
FEATURE [Part::Feature] Part__Feature351  label="Dielectric"
  shape: bbox 23.86 x 25 x 0.6706 mm, 18 faces (baked)
FEATURE [Part::Feature] Part__Feature352  label="SOLDERMASK_BOTTOM"
  shape: bbox 23.86 x 25 x 0.0127 mm, 140 faces (baked)
FEATURE [Part::Feature] Part__Feature353  label="PASTEMASK_BOTTOM"
  shape: bbox 3.28 x 5.82 x 0.0001002 mm, 180 faces, 30 solids (baked)
FEATURE [Part::Feature] Part__Feature354  label="SILKSCREEN_BOTTOM"
  shape: bbox 22.46 x 14.76 x 0.0127 mm, 1962 faces, 60 solids (baked)
FEATURE [App::Part] Shapes
  Group = -> [Part__Feature348,Part__Feature349,Part__Feature350,Part__Feature351,Part__Feature352,Part__Feature353,Part__Feature354]
  Origin = -> Origin051
FEATURE [Part::Feature] Part__Feature355  label="AP3445"
  shape: bbox 2.8 x 2.9 x 1.51 mm, 88 faces (baked)
FEATURE [Part::Feature] Part__Feature356  label="ATMEL_ATSHA204A_8UDFN"
  shape: bbox 18.15 x 11.2 x 6.694 mm, 2460 faces, 7 solids (baked)
FEATURE [Part::Feature] Part__Feature357  label="ATMEL_ATSHA204A_SOIC8"
  shape: bbox 6 x 4.9 x 1.848 mm, 130 faces (baked)
FEATURE [Part::Feature] Part__Feature358  label="BOURNS_SRN2512"
  shape: bbox 2.5 x 2 x 0.9 mm, 126 faces (baked)
FEATURE [Part::Feature] Part__Feature359  label="CAPC1005X55N"
  shape: bbox 1 x 0.5 x 0.5 mm, 40 faces (baked)
FEATURE [Part::Feature] Part__Feature360  label="CAPC1005X55N001"
  shape: bbox 1 x 0.5 x 0.5 mm, 40 faces (baked)
FEATURE [Part::Feature] Part__Feature361  label="CAPC1005X55N002"
  shape: bbox 1 x 0.5 x 0.5 mm, 40 faces (baked)
FEATURE [Part::Feature] Part__Feature362  label="CAPC1005X55N003"
  shape: bbox 1 x 0.5 x 0.5 mm, 40 faces (baked)
FEATURE [Part::Feature] Part__Feature363  label="CAPC1005X55N004"
  shape: bbox 0.5 x 1 x 0.5 mm, 40 faces (baked)
FEATURE [Part::Feature] Part__Feature364  label="CAPC1005X55N005"
  shape: bbox 0.5 x 1 x 0.5 mm, 40 faces (baked)
FEATURE [Part::Feature] Part__Feature365  label="CAPC1005X55N006"
  shape: bbox 0.5 x 1 x 0.5 mm, 40 faces (baked)
FEATURE [Part::Feature] Part__Feature366  label="CAPC1005X55N007"
  shape: bbox 1 x 0.5 x 0.5 mm, 40 faces (baked)
FEATURE [Part::Feature] Part__Feature367  label="CAPC1005X55N008"
  shape: bbox 1 x 0.5 x 0.5 mm, 40 faces (baked)
FEATURE [Part::Feature] Part__Feature368  label="CAPC1005X55N009"
  shape: bbox 1 x 0.5 x 0.5 mm, 40 faces (baked)
FEATURE [Part::Feature] Part__Feature369  label="CAPC1005X55N010"
  shape: bbox 0.5 x 1 x 0.5 mm, 40 faces (baked)
FEATURE [Part::Feature] Part__Feature370  label="CAPC1005X55N011"
  shape: bbox 0.5 x 1 x 0.5 mm, 40 faces (baked)
FEATURE [Part::Feature] Part__Feature371  label="CAPC1608"
  shape: bbox 1.6 x 0.8 x 0.8 mm, 40 faces (baked)
FEATURE [Part::Feature] Part__Feature372  label="CAPC1608X90N"
  shape: bbox 0.8 x 1.6 x 0.45 mm, 40 faces, 4 solids (baked)
FEATURE [Part::Feature] Part__Feature373  label="CAPC1608X90N001"
  shape: bbox 1.6 x 0.8 x 0.45 mm, 40 faces, 4 solids (baked)
FEATURE [Part::Feature] Part__Feature374  label="CAPC2012"
  shape: bbox 2 x 1.25 x 0.6 mm, 40 faces (baked)
FEATURE [Part::Feature] Part__Feature375  label="FCI_SFW15R-1STE1LF"
  shape: bbox 6.54 x 22.92 x 2.56 mm, 759 faces (baked)
FEATURE [Part::Feature] Part__Feature376  label="HIROSE_DF37NC-30DS-04V"
  shape: bbox 2.98 x 8.22 x 0.98 mm, 1577 faces (baked)
FEATURE [Part::Feature] Part__Feature377  label="MURATA_DLP11SNXXXHL2"
  shape: bbox 1.3 x 1 x 1.508 mm, 128 faces (baked)
FEATURE [Part::Feature] Part__Feature378  label="MURATA_DLP11SNXXXHL003"
  shape: bbox 1.3 x 1 x 1.508 mm, 128 faces (baked)
FEATURE [Part::Feature] Part__Feature379  label="MURATA_DLP11SNXXXHL004"
  shape: bbox 1.3 x 1 x 1.508 mm, 128 faces (baked)
FEATURE [Part::Feature] Part__Feature380  label="OSC_2P5X2MM"
  shape: bbox 3.2 x 2.5 x 0.92 mm, 26 faces (baked)
FEATURE [Part::Feature] Part__Feature381  label="RESC0603"
  shape: bbox 0.6 x 0.3 x 0.15 mm, 138 faces, 2 solids (baked)
FEATURE [Part::Feature] Part__Feature382  label="RESC0604"
  shape: bbox 0.3 x 0.6 x 0.15 mm, 138 faces, 2 solids (baked)
FEATURE [Part::Feature] Part__Feature383  label="RESC1005X40N"
  shape: bbox 1 x 0.5 x 0.5 mm, 40 faces (baked)
FEATURE [Part::Feature] Part__Feature384  label="RESC1005X40N001"
  shape: bbox 0.5 x 1 x 0.5 mm, 40 faces (baked)
FEATURE [Part::Feature] Part__Feature385  label="RESC1005X40N002"
  shape: bbox 1 x 0.5 x 0.5 mm, 40 faces (baked)
FEATURE [Part::Feature] Part__Feature386  label="RESC1005X40N003"
  shape: bbox 1 x 0.5 x 0.5 mm, 40 faces (baked)
FEATURE [Part::Feature] Part__Feature387  label="RESC1005X40N004"
  shape: bbox 1 x 0.5 x 0.5 mm, 40 faces (baked)
FEATURE [Part::Feature] Part__Feature388  label="SOT50P160X60-6N"
  shape: bbox 1.6 x 1.6 x 0.6 mm, 104 faces, 7 solids (baked)
FEATURE [Part::Feature] Part__Feature389  label="SOT95P280X145-5N"
  shape: bbox 2.8 x 2.9 x 1.51 mm, 88 faces (baked)
FEATURE [Part::Feature] Part__Feature390  label="SOT95P280X145-5N001"
  shape: bbox 2.8 x 2.9 x 1.51 mm, 88 faces (baked)
FEATURE [App::Part] Symbols
  Group = -> [Part__Feature355,Part__Feature356,Part__Feature357,Part__Feature358,Part__Feature359,Part__Feature360,Part__Feature361,Part__Feature362,Part__Feature363,Part__Feature364,Part__Feature365,Part__Feature366,Part__Feature367,Part__Feature368,Part__Feature369,Part__Feature370,Part__Feature371,Part__Feature372,Part__Feature373,Part__Feature374,Part__Feature375,Part__Feature376,Part__Feature377,+13 more]
  Origin = -> Origin052
FEATURE [App::Part] rpi_cam_v3_day_r1_brd  label=" camera module-3-wide"
  Group = -> [Pins,Shapes,Symbols]
  Origin = -> Origin053
  Placement = pos=(-47,-48.5,45) rot=(0,0,-1;1.5708rad)
FEATURE [Part::Feature] Part__Feature391  label="/PWDN001"
  shape: bbox 0.63 x 0.22 x 0.03048 mm, 6 faces (baked)
FEATURE [Part::Feature] Part__Feature392  label="1025"
  shape: bbox 1 x 0.95 x 0.03048 mm, 6 faces (baked)
FEATURE [Part::Feature] Part__Feature393  label="1026"
  shape: bbox 0.95 x 1 x 0.03048 mm, 6 faces (baked)
FEATURE [Part::Feature] Part__Feature394  label="1027"
  shape: bbox 0.57 x 0.58 x 0.03048 mm, 6 faces (baked)
FEATURE [Part::Feature] Part__Feature395  label="1028"
  shape: bbox 0.57 x 0.58 x 0.03048 mm, 6 faces (baked)
FEATURE [Part::Feature] Part__Feature396  label="1029"
  shape: bbox 0.58 x 0.57 x 0.03048 mm, 6 faces (baked)
FEATURE [Part::Feature] Part__Feature397  label="1030"
  shape: bbox 0.57 x 0.58 x 0.03048 mm, 6 faces (baked)
FEATURE [Part::Feature] Part__Feature398  label="1031"
  shape: bbox 0.57 x 0.58 x 0.03048 mm, 6 faces (baked)
FEATURE [Part::Feature] Part__Feature399  label="1032"
  shape: bbox 0.58 x 0.57 x 0.03048 mm, 6 faces (baked)
FEATURE [Part::Feature] Part__Feature400  label="1033"
  shape: bbox 0.45 x 0.275 x 0.03048 mm, 6 faces (baked)
FEATURE [Part::Feature] Part__Feature401  label="1034"
  shape: bbox 0.57 x 0.58 x 0.03048 mm, 6 faces (baked)
FEATURE [Part::Feature] Part__Feature402  label="1035"
  shape: bbox 0.275 x 0.45 x 0.03048 mm, 6 faces (baked)
FEATURE [Part::Feature] Part__Feature403  label="1036"
  shape: bbox 0.57 x 0.58 x 0.03048 mm, 6 faces (baked)
FEATURE [Part::Feature] Part__Feature404  label="1037"
  shape: bbox 0.58 x 0.57 x 0.03048 mm, 6 faces (baked)
FEATURE [Part::Feature] Part__Feature405  label="1038"
  shape: bbox 0.58 x 0.57 x 0.03048 mm, 6 faces (baked)
FEATURE [Part::Feature] Part__Feature406  label="1039"
  shape: bbox 0.57 x 0.58 x 0.03048 mm, 6 faces (baked)
FEATURE [Part::Feature] Part__Feature407  label="1040"
  shape: bbox 1.15 x 1.45 x 0.03048 mm, 6 faces (baked)
FEATURE [Part::Feature] Part__Feature408  label="1041"
  shape: bbox 0.57 x 0.58 x 0.03048 mm, 6 faces (baked)
FEATURE [Part::Feature] Part__Feature409  label="1042"
  shape: bbox 0.85 x 0.9 x 0.03048 mm, 6 faces (baked)
FEATURE [Part::Feature] Part__Feature410  label="1043"
  shape: bbox 0.58 x 0.57 x 0.03048 mm, 6 faces (baked)
FEATURE [Part::Feature] Part__Feature411  label="1044"
  shape: bbox 0.95 x 2.3 x 0.03048 mm, 6 faces (baked)
FEATURE [Part::Feature] Part__Feature412  label="1045"
  shape: bbox 2 x 0.5999 x 0.03048 mm, 6 faces (baked)
FEATURE [Part::Feature] Part__Feature413  label="1046"
  shape: bbox 0.57 x 0.58 x 0.03048 mm, 6 faces (baked)
FEATURE [Part::Feature] Part__Feature414  label="1047"
  shape: bbox 0.57 x 0.58 x 0.03048 mm, 6 faces (baked)
FEATURE [Part::Feature] Part__Feature415  label="1048"
  shape: bbox 0.57 x 0.58 x 0.03048 mm, 6 faces (baked)
FEATURE [Part::Feature] Part__Feature416  label="1049"
  shape: bbox 0.58 x 0.57 x 0.03048 mm, 6 faces (baked)
FEATURE [Part::Feature] Part__Feature417  label="10050"
  shape: bbox 2 x 0.5999 x 0.03048 mm, 6 faces (baked)
FEATURE [Part::Feature] Part__Feature418  label="11001"
  shape: bbox 2 x 0.5999 x 0.03048 mm, 6 faces (baked)
FEATURE [Part::Feature] Part__Feature419  label="12001"
  shape: bbox 2 x 0.5999 x 0.03048 mm, 6 faces (baked)
FEATURE [Part::Feature] Part__Feature420  label="13001"
  shape: bbox 2 x 0.5999 x 0.03048 mm, 6 faces (baked)
FEATURE [Part::Feature] Part__Feature421  label="14001"
  shape: bbox 2 x 0.5999 x 0.03048 mm, 6 faces (baked)
FEATURE [Part::Feature] Part__Feature422  label="15001"
  shape: bbox 2 x 0.5999 x 0.03048 mm, 6 faces (baked)
FEATURE [Part::Feature] Part__Feature423  label="2025"
  shape: bbox 0.58 x 0.57 x 0.03048 mm, 6 faces (baked)
FEATURE [Part::Feature] Part__Feature424  label="2026"
  shape: bbox 1.15 x 1.45 x 0.03048 mm, 6 faces (baked)
FEATURE [Part::Feature] Part__Feature425  label="2027"
  shape: bbox 0.85 x 0.9 x 0.03048 mm, 6 faces (baked)
FEATURE [Part::Feature] Part__Feature426  label="2028"
  shape: bbox 0.95 x 2.3 x 0.03048 mm, 6 faces (baked)
FEATURE [Part::Feature] Part__Feature427  label="2029"
  shape: bbox 2 x 0.5999 x 0.03048 mm, 6 faces (baked)
FEATURE [Part::Feature] Part__Feature428  label="2030"
  shape: bbox 0.58 x 0.57 x 0.03048 mm, 6 faces (baked)
FEATURE [Part::Feature] Part__Feature429  label="2031"
  shape: bbox 0.95 x 1 x 0.03048 mm, 6 faces (baked)
FEATURE [Part::Feature] Part__Feature430  label="2032"
  shape: bbox 0.58 x 0.57 x 0.03048 mm, 6 faces (baked)
FEATURE [Part::Feature] Part__Feature431  label="2033"
  shape: bbox 0.57 x 0.58 x 0.03048 mm, 6 faces (baked)
FEATURE [Part::Feature] Part__Feature432  label="2034"
  shape: bbox 0.57 x 0.58 x 0.03048 mm, 6 faces (baked)
FEATURE [Part::Feature] Part__Feature433  label="2035"
  shape: bbox 0.57 x 0.58 x 0.03048 mm, 6 faces (baked)
FEATURE [Part::Feature] Part__Feature434  label="2036"
  shape: bbox 0.57 x 0.58 x 0.03048 mm, 6 faces (baked)
FEATURE [Part::Feature] Part__Feature435  label="2037"
  shape: bbox 0.58 x 0.57 x 0.03048 mm, 6 faces (baked)
FEATURE [Part::Feature] Part__Feature436  label="2038"
  shape: bbox 0.58 x 0.57 x 0.03048 mm, 6 faces (baked)
FEATURE [Part::Feature] Part__Feature437  label="2039"
  shape: bbox 0.57 x 0.58 x 0.03048 mm, 6 faces (baked)
FEATURE [Part::Feature] Part__Feature438  label="2040"
  shape: bbox 0.57 x 0.58 x 0.03048 mm, 6 faces (baked)
FEATURE [Part::Feature] Part__Feature439  label="2041"
  shape: bbox 0.58 x 0.57 x 0.03048 mm, 6 faces (baked)
FEATURE [Part::Feature] Part__Feature440  label="2042"
  shape: bbox 0.57 x 0.58 x 0.03048 mm, 6 faces (baked)
FEATURE [Part::Feature] Part__Feature441  label="2043"
  shape: bbox 0.57 x 0.58 x 0.03048 mm, 6 faces (baked)
FEATURE [Part::Feature] Part__Feature442  label="2044"
  shape: bbox 1 x 0.95 x 0.03048 mm, 6 faces (baked)
FEATURE [Part::Feature] Part__Feature443  label="2045"
  shape: bbox 0.57 x 0.58 x 0.03048 mm, 6 faces (baked)
FEATURE [Part::Feature] Part__Feature444  label="2046"
  shape: bbox 0.57 x 0.58 x 0.03048 mm, 6 faces (baked)
FEATURE [Part::Feature] Part__Feature445  label="2047"
  shape: bbox 0.45 x 0.275 x 0.03048 mm, 6 faces (baked)
FEATURE [Part::Feature] Part__Feature446  label="2048"
  shape: bbox 0.57 x 0.58 x 0.03048 mm, 6 faces (baked)
FEATURE [Part::Feature] Part__Feature447  label="2049"
  shape: bbox 0.275 x 0.45 x 0.03048 mm, 6 faces (baked)
FEATURE [Part::Feature] Part__Feature448  label="3001"
  shape: bbox 2 x 0.5999 x 0.03048 mm, 6 faces (baked)
FEATURE [Part::Feature] Part__Feature449  label="4001"
  shape: bbox 2 x 0.5999 x 0.03048 mm, 6 faces (baked)
FEATURE [Part::Feature] Part__Feature450  label="5001"
  shape: bbox 2 x 0.5999 x 0.03048 mm, 6 faces (baked)
FEATURE [Part::Feature] Part__Feature451  label="6001"
  shape: bbox 2 x 0.5999 x 0.03048 mm, 6 faces (baked)
FEATURE [Part::Feature] Part__Feature452  label="7001"
  shape: bbox 2 x 0.5999 x 0.03048 mm, 6 faces (baked)
FEATURE [Part::Feature] Part__Feature453  label="8001"
  shape: bbox 2 x 0.5999 x 0.03048 mm, 6 faces (baked)
FEATURE [Part::Feature] Part__Feature454  label="9001"
  shape: bbox 2 x 0.5999 x 0.03048 mm, 6 faces (baked)
FEATURE [Part::Feature] Part__Feature455  label="AFVDD001"
  shape: bbox 0.63 x 0.22 x 0.03048 mm, 6 faces (baked)
FEATURE [Part::Feature] Part__Feature456  label="AGND001"
  shape: bbox 0.63 x 0.22 x 0.03048 mm, 6 faces (baked)
FEATURE [Part::Feature] Part__Feature457  label="D004"
  shape: bbox 0.3 x 0.5 x 0.03048 mm, 6 faces (baked)
FEATURE [Part::Feature] Part__Feature458  label="D005"
  shape: bbox 0.3 x 0.5 x 0.03048 mm, 6 faces (baked)
FEATURE [Part::Feature] Part__Feature459  label="DGND010"
  shape: bbox 0.63 x 0.22 x 0.03048 mm, 6 faces (baked)
FEATURE [Part::Feature] Part__Feature460  label="DGND011"
  shape: bbox 0.63 x 0.22 x 0.03048 mm, 6 faces (baked)
FEATURE [Part::Feature] Part__Feature461  label="DGND012"
  shape: bbox 0.63 x 0.22 x 0.03048 mm, 6 faces (baked)
FEATURE [Part::Feature] Part__Feature462  label="DGND013"
  shape: bbox 0.63 x 0.22 x 0.03048 mm, 6 faces (baked)
FEATURE [Part::Feature] Part__Feature463  label="DGND014"
  shape: bbox 0.63 x 0.22 x 0.03048 mm, 6 faces (baked)
FEATURE [Part::Feature] Part__Feature464  label="DGND015"
  shape: bbox 0.63 x 0.22 x 0.03048 mm, 6 faces (baked)
FEATURE [Part::Feature] Part__Feature465  label="DGND016"
  shape: bbox 0.63 x 0.22 x 0.03048 mm, 6 faces (baked)
FEATURE [Part::Feature] Part__Feature466  label="DGND017"
  shape: bbox 0.63 x 0.22 x 0.03048 mm, 6 faces (baked)
FEATURE [Part::Feature] Part__Feature467  label="DGND018"
  shape: bbox 0.63 x 0.22 x 0.03048 mm, 6 faces (baked)
FEATURE [Part::Feature] Part__Feature468  label="DVDD001"
  shape: bbox 0.63 x 0.22 x 0.03048 mm, 6 faces (baked)
FEATURE [Part::Feature] Part__Feature469  label="DVDD/GPIO001"
  shape: bbox 0.63 x 0.22 x 0.03048 mm, 6 faces (baked)
FEATURE [Part::Feature] Part__Feature470  label="EN003"
  shape: bbox 1.1 x 0.6 x 0.03048 mm, 6 faces (baked)
FEATURE [Part::Feature] Part__Feature471  label="EN004"
  shape: bbox 1.1 x 0.6 x 0.03048 mm, 6 faces (baked)
FEATURE [Part::Feature] Part__Feature472  label="EN005"
  shape: bbox 1.1 x 0.6 x 0.03048 mm, 6 faces (baked)
FEATURE [Part::Feature] Part__Feature473  label="EXP_PAD001"
  shape: bbox 1.6 x 1.4 x 0.03048 mm, 6 faces (baked)
FEATURE [Part::Feature] Part__Feature474  label="FB001"
  shape: bbox 1.1 x 0.6 x 0.03048 mm, 6 faces (baked)
FEATURE [Part::Feature] Part__Feature475  label="G004"
  shape: bbox 0.3 x 0.5 x 0.03048 mm, 6 faces (baked)
FEATURE [Part::Feature] Part__Feature476  label="G005"
  shape: bbox 0.3 x 0.5 x 0.03048 mm, 6 faces (baked)
FEATURE [Part::Feature] Part__Feature477  label="GND007"
  shape: bbox 0.63 x 0.22 x 0.03048 mm, 6 faces (baked)
FEATURE [Part::Feature] Part__Feature478  label="GND008"
  shape: bbox 1.1 x 0.6 x 0.03048 mm, 6 faces (baked)
FEATURE [Part::Feature] Part__Feature479  label="GND009"
  shape: bbox 0.8999 x 0.8001 x 0.03048 mm, 6 faces (baked)
FEATURE [Part::Feature] Part__Feature480  label="GND010"
  shape: bbox 1.1 x 0.6 x 0.03048 mm, 6 faces (baked)
FEATURE [Part::Feature] Part__Feature481  label="GND011"
  shape: bbox 1.5 x 0.6 x 0.03048 mm, 6 faces (baked)
FEATURE [Part::Feature] Part__Feature482  label="GND012"
  shape: bbox 0.3 x 0.85 x 0.03048 mm, 6 faces (baked)
FEATURE [Part::Feature] Part__Feature483  label="GND013"
  shape: bbox 1.1 x 0.6 x 0.03048 mm, 6 faces (baked)
FEATURE [Part::Feature] Part__Feature484  label="IN002"
  shape: bbox 1.1 x 0.6 x 0.03048 mm, 6 faces (baked)
FEATURE [Part::Feature] Part__Feature485  label="IN003"
  shape: bbox 1.1 x 0.6 x 0.03048 mm, 6 faces (baked)
FEATURE [Part::Feature] Part__Feature486  label="LX001"
  shape: bbox 1.1 x 0.6 x 0.03048 mm, 6 faces (baked)
FEATURE [Part::Feature] Part__Feature487  label="MCKN001"
  shape: bbox 0.63 x 0.22 x 0.03048 mm, 6 faces (baked)
FEATURE [Part::Feature] Part__Feature488  label="MCKP001"
  shape: bbox 0.63 x 0.22 x 0.03048 mm, 6 faces (baked)
FEATURE [Part::Feature] Part__Feature489  label="MCLK001"
  shape: bbox 0.63 x 0.22 x 0.03048 mm, 6 faces (baked)
FEATURE [Part::Feature] Part__Feature490  label="MD0N001"
  shape: bbox 0.63 x 0.22 x 0.03048 mm, 6 faces (baked)
FEATURE [Part::Feature] Part__Feature491  label="MD0P001"
  shape: bbox 0.63 x 0.22 x 0.03048 mm, 6 faces (baked)
FEATURE [Part::Feature] Part__Feature492  label="MD1N001"
  shape: bbox 0.63 x 0.22 x 0.03048 mm, 6 faces (baked)
FEATURE [Part::Feature] Part__Feature493  label="MD1P001"
  shape: bbox 0.63 x 0.22 x 0.03048 mm, 6 faces (baked)
FEATURE [Part::Feature] Part__Feature494  label="MECHANICAL PIN006"
  shape: bbox 1.5 x 1.5 x 0.03048 mm, 4 faces (baked)
FEATURE [Part::Feature] Part__Feature495  label="MECHANICAL PIN007"
  shape: bbox 3.6 x 2.68 x 0.03048 mm, 6 faces (baked)
FEATURE [Part::Feature] Part__Feature496  label="MECHANICAL PIN008"
  shape: bbox 3.6 x 2.68 x 0.03048 mm, 6 faces (baked)
FEATURE [Part::Feature] Part__Feature497  label="MECHANICAL PIN009"
  shape: bbox 4.2 x 0.7 x 0.03048 mm, 6 faces (baked)
FEATURE [Part::Feature] Part__Feature498  label="MECHANICAL PIN010"
  shape: bbox 4.2 x 0.7 x 0.03048 mm, 6 faces (baked)
FEATURE [Part::Feature] Part__Feature499  label="MECHANICAL PIN011"
  shape: bbox 1.5 x 1.5 x 0.03048 mm, 4 faces (baked)
FEATURE [Part::Feature] Part__Feature500  label="NC008"
  shape: bbox 1.1 x 0.6 x 0.03048 mm, 6 faces (baked)
FEATURE [Part::Feature] Part__Feature501  label="NC009"
  shape: bbox 1.1 x 0.6 x 0.03048 mm, 6 faces (baked)
FEATURE [Part::Feature] Part__Feature502  label="NC010"
  shape: bbox 1.5 x 0.6 x 0.03048 mm, 6 faces (baked)
FEATURE [Part::Feature] Part__Feature503  label="NC011"
  shape: bbox 0.63 x 0.22 x 0.03048 mm, 6 faces (baked)
FEATURE [Part::Feature] Part__Feature504  label="NC012"
  shape: bbox 0.3 x 0.85 x 0.03048 mm, 6 faces (baked)
FEATURE [Part::Feature] Part__Feature505  label="NC013"
  shape: bbox 1.5 x 0.6 x 0.03048 mm, 6 faces (baked)
FEATURE [Part::Feature] Part__Feature506  label="NC014"
  shape: bbox 0.63 x 0.22 x 0.03048 mm, 6 faces (baked)
FEATURE [Part::Feature] Part__Feature507  label="NC015"
  shape: bbox 0.3 x 0.85 x 0.03048 mm, 6 faces (baked)
FEATURE [Part::Feature] Part__Feature508  label="NC016"
  shape: bbox 0.3 x 0.85 x 0.03048 mm, 6 faces (baked)
FEATURE [Part::Feature] Part__Feature509  label="NC017"
  shape: bbox 1.5 x 0.6 x 0.03048 mm, 6 faces (baked)
FEATURE [Part::Feature] Part__Feature510  label="NC018"
  shape: bbox 1.5 x 0.6 x 0.03048 mm, 6 faces (baked)
FEATURE [Part::Feature] Part__Feature511  label="NC019"
  shape: bbox 0.63 x 0.22 x 0.03048 mm, 6 faces (baked)
FEATURE [Part::Feature] Part__Feature512  label="NC020"
  shape: bbox 0.63 x 0.22 x 0.03048 mm, 6 faces (baked)
FEATURE [Part::Feature] Part__Feature513  label="NC021"
  shape: bbox 0.3 x 0.85 x 0.03048 mm, 6 faces (baked)
FEATURE [Part::Feature] Part__Feature514  label="OE001"
  shape: bbox 0.8999 x 0.8001 x 0.03048 mm, 6 faces (baked)
FEATURE [Part::Feature] Part__Feature515  label="OUT002"
  shape: bbox 1.1 x 0.6 x 0.03048 mm, 6 faces (baked)
FEATURE [Part::Feature] Part__Feature516  label="OUT003"
  shape: bbox 1.1 x 0.6 x 0.03048 mm, 6 faces (baked)
FEATURE [Part::Feature] Part__Feature517  label="OUTPUT001"
  shape: bbox 0.8999 x 0.8001 x 0.03048 mm, 6 faces (baked)
FEATURE [Part::Feature] Part__Feature518  label="P010"
  shape: bbox 0.7 x 0.28 x 0.03048 mm, 6 faces (baked)
FEATURE [Part::Feature] Part__Feature519  label="P011"
  shape: bbox 0.7 x 0.28 x 0.03048 mm, 6 faces (baked)
FEATURE [Part::Feature] Part__Feature520  label="P012"
  shape: bbox 0.7 x 0.28 x 0.03048 mm, 6 faces (baked)
FEATURE [Part::Feature] Part__Feature521  label="P013"
  shape: bbox 0.7 x 0.28 x 0.03048 mm, 6 faces (baked)
FEATURE [Part::Feature] Part__Feature522  label="P014"
  shape: bbox 0.7 x 0.28 x 0.03048 mm, 6 faces (baked)
FEATURE [Part::Feature] Part__Feature523  label="P015"
  shape: bbox 0.7 x 0.28 x 0.03048 mm, 6 faces (baked)
FEATURE [Part::Feature] Part__Feature524  label="P016"
  shape: bbox 0.7 x 0.28 x 0.03048 mm, 6 faces (baked)
FEATURE [Part::Feature] Part__Feature525  label="P017"
  shape: bbox 0.7 x 0.28 x 0.03048 mm, 6 faces (baked)
FEATURE [Part::Feature] Part__Feature526  label="P018"
  shape: bbox 0.7 x 0.28 x 0.03048 mm, 6 faces (baked)
FEATURE [Part::Feature] Part__Feature527  label="P019"
  shape: bbox 0.7 x 0.28 x 0.03048 mm, 6 faces (baked)
FEATURE [Part::Feature] Part__Feature528  label="P020"
  shape: bbox 0.7 x 0.28 x 0.03048 mm, 6 faces (baked)
FEATURE [Part::Feature] Part__Feature529  label="P021"
  shape: bbox 0.7 x 0.28 x 0.03048 mm, 6 faces (baked)
FEATURE [Part::Feature] Part__Feature530  label="PG001"
  shape: bbox 1.1 x 0.6 x 0.03048 mm, 6 faces (baked)
FEATURE [Part::Feature] Part__Feature531  label="S004"
  shape: bbox 0.3 x 0.5 x 0.03048 mm, 6 faces (baked)
FEATURE [Part::Feature] Part__Feature532  label="S005"
  shape: bbox 0.3 x 0.5 x 0.03048 mm, 6 faces (baked)
FEATURE [Part::Feature] Part__Feature533  label="SCL003"
  shape: bbox 1.5 x 0.6 x 0.03048 mm, 6 faces (baked)
FEATURE [Part::Feature] Part__Feature534  label="SCL004"
  shape: bbox 0.3 x 0.85 x 0.03048 mm, 6 faces (baked)
FEATURE [Part::Feature] Part__Feature535  label="SCL005"
  shape: bbox 0.63 x 0.22 x 0.03048 mm, 6 faces (baked)
FEATURE [Part::Feature] Part__Feature536  label="SDA003"
  shape: bbox 0.63 x 0.22 x 0.03048 mm, 6 faces (baked)
FEATURE [Part::Feature] Part__Feature537  label="SDA004"
  shape: bbox 0.3 x 0.85 x 0.03048 mm, 6 faces (baked)
FEATURE [Part::Feature] Part__Feature538  label="SDA005"
  shape: bbox 1.5 x 0.6 x 0.03048 mm, 6 faces (baked)
FEATURE [Part::Feature] Part__Feature539  label="VA2V009"
  shape: bbox 0.63 x 0.22 x 0.03048 mm, 6 faces (baked)
FEATURE [Part::Feature] Part__Feature540  label="VCC002"
  shape: bbox 0.3 x 0.85 x 0.03048 mm, 6 faces (baked)
FEATURE [Part::Feature] Part__Feature541  label="VCC003"
  shape: bbox 1.5 x 0.6 x 0.03048 mm, 6 faces (baked)
FEATURE [Part::Feature] Part__Feature542  label="VDD001"
  shape: bbox 0.8999 x 0.8001 x 0.03048 mm, 6 faces (baked)
FEATURE [Part::Feature] Part__Feature543  label="VIN001"
  shape: bbox 1.1 x 0.6 x 0.03048 mm, 6 faces (baked)
FEATURE [Part::Feature] Part__Feature544  label="VO1V009"
  shape: bbox 0.63 x 0.22 x 0.03048 mm, 6 faces (baked)
FEATURE [App::Part] Pins001
  Group = -> [Part__Feature391,Part__Feature392,Part__Feature393,Part__Feature394,Part__Feature395,Part__Feature396,Part__Feature397,Part__Feature398,Part__Feature399,Part__Feature400,Part__Feature401,Part__Feature402,Part__Feature403,Part__Feature404,Part__Feature405,Part__Feature406,Part__Feature407,Part__Feature408,Part__Feature409,Part__Feature410,Part__Feature411,Part__Feature412,Part__Feature413,+131 more]
  Origin = -> Origin054
FEATURE [Part::Feature] Part__Feature545  label="SILKSCREEN_TOP001"
  shape: bbox 18.45 x 22.65 x 0.0127 mm, 5798 faces, 168 solids (baked)
FEATURE [Part::Feature] Part__Feature546  label="PASTEMASK_TOP001"
  shape: bbox 21.25 x 22.68 x 0.0001002 mm, 726 faces, 121 solids (baked)
FEATURE [Part::Feature] Part__Feature547  label="SOLDERMASK_TOP001"
  shape: bbox 23.86 x 25 x 0.0127 mm, 504 faces (baked)
FEATURE [Part::Feature] Part__Feature548  label="Dielectric001"
  shape: bbox 23.86 x 25 x 0.6706 mm, 18 faces (baked)
FEATURE [Part::Feature] Part__Feature549  label="SOLDERMASK_BOTTOM001"
  shape: bbox 23.86 x 25 x 0.0127 mm, 140 faces (baked)
FEATURE [Part::Feature] Part__Feature550  label="PASTEMASK_BOTTOM001"
  shape: bbox 3.28 x 5.82 x 0.0001002 mm, 180 faces, 30 solids (baked)
FEATURE [Part::Feature] Part__Feature551  label="SILKSCREEN_BOTTOM001"
  shape: bbox 22.98 x 17.08 x 0.0127 mm, 2334 faces, 92 solids (baked)
FEATURE [App::Part] Shapes001
  Group = -> [Part__Feature545,Part__Feature546,Part__Feature547,Part__Feature548,Part__Feature549,Part__Feature550,Part__Feature551]
  Origin = -> Origin055
FEATURE [Part::Feature] Part__Feature552  label="AP3446"
  shape: bbox 2.8 x 2.9 x 1.51 mm, 88 faces (baked)
FEATURE [Part::Feature] Part__Feature553  label="ATMEL_ATSHA204A_8UDFN001"
  shape: bbox 18.1 x 11.15 x 7.812 mm, 1804 faces, 14 solids (baked)
FEATURE [Part::Feature] Part__Feature554  label="ATMEL_ATSHA204A_SOIC009"
  shape: bbox 6 x 4.9 x 1.848 mm, 130 faces (baked)
FEATURE [Part::Feature] Part__Feature555  label="BOURNS_SRN2513"
  shape: bbox 2.5 x 2 x 0.9 mm, 126 faces (baked)
FEATURE [Part::Feature] Part__Feature556  label="CAPC1005X55N012"
  shape: bbox 1 x 0.5 x 0.5 mm, 40 faces (baked)
FEATURE [Part::Feature] Part__Feature557  label="CAPC1005X55N013"
  shape: bbox 1 x 0.5 x 0.5 mm, 40 faces (baked)
FEATURE [Part::Feature] Part__Feature558  label="CAPC1005X55N014"
  shape: bbox 1 x 0.5 x 0.5 mm, 40 faces (baked)
FEATURE [Part::Feature] Part__Feature559  label="CAPC1005X55N015"
  shape: bbox 1 x 0.5 x 0.5 mm, 40 faces (baked)
FEATURE [Part::Feature] Part__Feature560  label="CAPC1005X55N016"
  shape: bbox 0.5 x 1 x 0.5 mm, 40 faces (baked)
FEATURE [Part::Feature] Part__Feature561  label="CAPC1005X55N017"
  shape: bbox 0.5 x 1 x 0.5 mm, 40 faces (baked)
FEATURE [Part::Feature] Part__Feature562  label="CAPC1005X55N018"
  shape: bbox 0.5 x 1 x 0.5 mm, 40 faces (baked)
FEATURE [Part::Feature] Part__Feature563  label="CAPC1005X55N019"
  shape: bbox 1 x 0.5 x 0.5 mm, 40 faces (baked)
FEATURE [Part::Feature] Part__Feature564  label="CAPC1005X55N020"
  shape: bbox 1 x 0.5 x 0.5 mm, 40 faces (baked)
FEATURE [Part::Feature] Part__Feature565  label="CAPC1005X55N021"
  shape: bbox 1 x 0.5 x 0.5 mm, 40 faces (baked)
FEATURE [Part::Feature] Part__Feature566  label="CAPC1005X55N022"
  shape: bbox 0.5 x 1 x 0.5 mm, 40 faces (baked)
FEATURE [Part::Feature] Part__Feature567  label="CAPC1005X55N023"
  shape: bbox 0.5 x 1 x 0.5 mm, 40 faces (baked)
FEATURE [Part::Feature] Part__Feature568  label="CAPC2013"
  shape: bbox 1.6 x 0.8 x 0.8 mm, 40 faces (baked)
FEATURE [Part::Feature] Part__Feature569  label="CAPC1608X90N002"
  shape: bbox 0.8 x 1.6 x 0.45 mm, 40 faces, 4 solids (baked)
FEATURE [Part::Feature] Part__Feature570  label="CAPC1608X90N003"
  shape: bbox 1.6 x 0.8 x 0.45 mm, 40 faces, 4 solids (baked)
FEATURE [Part::Feature] Part__Feature571  label="CAPC2014"
  shape: bbox 2 x 1.25 x 0.6 mm, 40 faces (baked)
FEATURE [Part::Feature] Part__Feature572  label="FCI_SFW15R-1STE1LF001"
  shape: bbox 6.54 x 22.92 x 2.56 mm, 759 faces (baked)
FEATURE [Part::Feature] Part__Feature573  label="HIROSE_DF37NC-30DS-04V001"
  shape: bbox 2.98 x 8.22 x 0.98 mm, 1577 faces (baked)
FEATURE [Part::Feature] Part__Feature574  label="MURATA_DLP11SNXXXHL005"
  shape: bbox 1.3 x 1 x 1.508 mm, 128 faces (baked)
FEATURE [Part::Feature] Part__Feature575  label="MURATA_DLP11SNXXXHL006"
  shape: bbox 1.3 x 1 x 1.508 mm, 128 faces (baked)
FEATURE [Part::Feature] Part__Feature576  label="MURATA_DLP11SNXXXHL007"
  shape: bbox 1.3 x 1 x 1.508 mm, 128 faces (baked)
FEATURE [Part::Feature] Part__Feature577  label="OSC_2P5X2MM001"
  shape: bbox 3.2 x 2.5 x 0.92 mm, 26 faces (baked)
FEATURE [Part::Feature] Part__Feature578  label="RESC0605"
  shape: bbox 0.6 x 0.3 x 0.15 mm, 138 faces, 2 solids (baked)
FEATURE [Part::Feature] Part__Feature579  label="RESC0606"
  shape: bbox 0.3 x 0.6 x 0.15 mm, 138 faces, 2 solids (baked)
FEATURE [Part::Feature] Part__Feature580  label="RESC1005X40N005"
  shape: bbox 1 x 0.5 x 0.5 mm, 40 faces (baked)
FEATURE [Part::Feature] Part__Feature581  label="RESC1005X40N006"
  shape: bbox 0.5 x 1 x 0.5 mm, 40 faces (baked)
FEATURE [Part::Feature] Part__Feature582  label="RESC1005X40N007"
  shape: bbox 1 x 0.5 x 0.5 mm, 40 faces (baked)
FEATURE [Part::Feature] Part__Feature583  label="RESC1005X40N008"
  shape: bbox 1 x 0.5 x 0.5 mm, 40 faces (baked)
FEATURE [Part::Feature] Part__Feature584  label="RESC1005X40N009"
  shape: bbox 1 x 0.5 x 0.5 mm, 40 faces (baked)
FEATURE [Part::Feature] Part__Feature585  label="SOT50P160X60-6N001"
  shape: bbox 1.6 x 1.6 x 0.6 mm, 104 faces, 7 solids (baked)
FEATURE [Part::Feature] Part__Feature586  label="SOT95P280X145-5N002"
  shape: bbox 2.8 x 2.9 x 1.51 mm, 88 faces (baked)
FEATURE [Part::Feature] Part__Feature587  label="SOT95P280X145-5N003"
  shape: bbox 2.8 x 2.9 x 1.51 mm, 88 faces (baked)
FEATURE [App::Part] Symbols001
  Group = -> [Part__Feature552,Part__Feature553,Part__Feature554,Part__Feature555,Part__Feature556,Part__Feature557,Part__Feature558,Part__Feature559,Part__Feature560,Part__Feature561,Part__Feature562,Part__Feature563,Part__Feature564,Part__Feature565,Part__Feature566,Part__Feature567,Part__Feature568,Part__Feature569,Part__Feature570,Part__Feature571,Part__Feature572,Part__Feature573,Part__Feature574,+13 more]
  Origin = -> Origin056
FEATURE [App::Part] rpi_cam_v3_day_r1_brd001  label=" camera module-3"
  Group = -> [Pins001,Shapes001,Symbols001]
  Origin = -> Origin057
  Placement = pos=(-47,-98,22.5) rot=(-0.57735,-0.57735,-0.57735;2.0944rad)
FEATURE [Part::Box] Box024  label="立方体004"
  AttacherType = Attacher::AttachEngine3D
  Height = 25
  Length = 51
  Placement = pos=(-51,-93,16) rot=(0,0,1;0rad)
  Width = 5
FEATURE [Part::Box] Box025  label="立方体005"
  AttacherType = Attacher::AttachEngine3D
  Height = 25
  Length = 23
  Placement = pos=(-37,-93,16) rot=(0,0,1;0rad)
  Width = 5
FEATURE [Part::Box] Box026  label="立方体006"
  AttacherType = Attacher::AttachEngine3D
  Height = 10
  Length = 51
  Placement = pos=(-51,-90,31) rot=(0,0,1;0rad)
  Width = 5
FEATURE [Part::Box] Box384  label="立方体354"
  AttacherType = Attacher::AttachEngine3D
  Height = 2
  Length = 2
  Placement = pos=(-47,-93,26) rot=(0,0,1;0rad)
  Width = 5
FEATURE [Part::Box] Box385  label="立方体355"
  AttacherType = Attacher::AttachEngine3D
  Height = 2
  Length = 2
  Placement = pos=(-24,-93,26) rot=(0,0,1;0rad)
  Width = 5
FEATURE [Part::Cylinder] Cylinder294  label="円柱294"
  Angle = 360
  AttacherType = Attacher::AttachEngine3D
  FirstAngle = 0
  Height = 20
  Placement = pos=(-53,-88,43) rot=(1,0,0;1.5708rad)
  Radius = 2
  SecondAngle = 0
FEATURE [Part::Cylinder] Cylinder295  label="円柱295"
  Angle = 360
  AttacherType = Attacher::AttachEngine3D
  FirstAngle = 0
  Height = 20
  Placement = pos=(-16,-88,43) rot=(1,0,0;1.5708rad)
  Radius = 2
  SecondAngle = 0
FEATURE [Part::MultiFuse] Fusion223
  Shapes = -> [Box024,Box026]
FEATURE [Part::Cut] Cut268
  Base = -> Fusion223
  Placement = pos=(-9,0,10) rot=(0,0,1;0rad)
  Tool = -> Box025
FEATURE [Part::MultiFuse] Fusion224
  Placement = pos=(0,-5,-4) rot=(0,0,1;0rad)
  Shapes = -> [Box384,Box385,Cut268]
FEATURE [Part::MultiFuse] Fusion233
  Shapes = -> [Cylinder294,Cylinder295]
FEATURE [Part::Cut] Cut413  label="Comera cover 1"
  Base = -> Fusion224
  Refine = true
  Tool = -> Fusion233
FEATURE [Part::Box] Box097  label="立方体076"
  AttacherType = Attacher::AttachEngine3D
  Height = 25
  Length = 52
  Placement = pos=(-60,-93,16) rot=(0,0,1;0rad)
  Width = 5
FEATURE [Part::Box] Box098  label="立方体077"
  AttacherType = Attacher::AttachEngine3D
  Height = 25
  Length = 35
  Placement = pos=(-52,-88,16) rot=(0,0,1;0rad)
  Width = 5
FEATURE [Part::Box] Box321  label="立方体293"
  AttacherType = Attacher::AttachEngine3D
  Height = 25
  Length = 23
  Placement = pos=(-46,-93,16) rot=(0,0,1;0rad)
  Width = 5
FEATURE [Part::Cylinder] Cylinder187  label="円柱187"
  Angle = 360
  AttacherType = Attacher::AttachEngine3D
  FirstAngle = 0
  Height = 13
  Placement = pos=(-55,-69,-5) rot=(0,0,1;0rad)
  Radius = 2
  SecondAngle = 0
FEATURE [Part::Cylinder] Cylinder188  label="円柱188"
  Angle = 360
  AttacherType = Attacher::AttachEngine3D
  FirstAngle = 0
  Height = 13
  Placement = pos=(-12,-69,-5) rot=(0,0,1;0rad)
  Radius = 2
  SecondAngle = 0
FEATURE [Part::MultiFuse] Fusion
  Shapes = -> [Box097,Box098]
FEATURE [Part::Cut] Cut144
  Base = -> Fusion
  Placement = pos=(0,-40,96) rot=(1,0,0;1.5708rad)
  Tool = -> Box321
FEATURE [Part::Cut] Cut147
  Base = -> Cut144
  Tool = -> Cylinder187
FEATURE [Part::Cut] Cut148  label="Comera cover 2"
  Base = -> Cut147
  Placement = pos=(0,8,42) rot=(0,0,1;0rad)
  Tool = -> Cylinder188
FEATURE [Part::Box] Box060
  AttacherType = Attacher::AttachEngine3D
  Height = 26.5
  Length = 58
  Placement = pos=(-62.9,-27,0) rot=(0,0,1;0rad)
  Width = 81.5
FEATURE [Part::Fillet] Fillet016  label="portable charger"
  Base = -> Box060
  EdgeLinks = -> Box060 [Edge1,Edge2,Edge3,Edge4,Edge5,Edge6,Edge7,Edge8,Edge9,Edge10,Edge11,Edge12]
  Edges = 12 edges r=5: [Edge1,Edge2,Edge3,Edge4,Edge5,Edge6,Edge7,Edge8,Edge9,Edge10,Edge11,Edge12]
FEATURE [Part::Box] Box531  label="立方体501"
  AttacherType = Attacher::AttachEngine3D
  Height = 13.5
  Length = 34
  Width = 71
FEATURE [Part::Fillet] Fillet039  label="Lipo battery"
  Base = -> Box531
  EdgeLinks = -> Box531 [Edge1,Edge2,Edge3,Edge4,Edge5,Edge6,Edge7,Edge8,Edge9,Edge10,Edge11,Edge12]
  Edges = 12 edges r=2: [Edge1,Edge2,Edge3,Edge4,Edge5,Edge6,Edge7,Edge8,Edge9,Edge10,Edge11,Edge12]
  Placement = pos=(-38,-14,37) rot=(0,0,1;0rad)
FEATURE [Part::Box] Box397  label="立方体367"
  AttacherType = Attacher::AttachEngine3D
  Height = 20
  Length = 33
  Placement = pos=(-42,59,37) rot=(0,0,1;0rad)
  Width = 4
FEATURE [Part::Box] Box400  label="立方体370"
  AttacherType = Attacher::AttachEngine3D
  Height = 5
  Length = 33
  Placement = pos=(-42,59,37) rot=(0,0,1;0rad)
  Width = 22
FEATURE [Part::Cylinder] Cylinder290  label="円柱290"
  Angle = 360
  AttacherType = Attacher::AttachEngine3D
  FirstAngle = 0
  Height = 10
  Placement = pos=(-36,72,32) rot=(0,0,1;0rad)
  Radius = 2
  SecondAngle = 0
FEATURE [Part::Cylinder] Cylinder291  label="円柱291"
  Angle = 360
  AttacherType = Attacher::AttachEngine3D
  FirstAngle = 0
  Height = 10
  Placement = pos=(-15,72,32) rot=(0,0,1;0rad)
  Radius = 2
  SecondAngle = 0
FEATURE [Part::MultiFuse] Fusion229
  Shapes = -> [Cylinder290,Cylinder291]
FEATURE [Part::Cut] Cut277
  Base = -> Box400
  Tool = -> Fusion229
FEATURE [Part::MultiFuse] Fusion231  label="Lipo cover"
  Shapes = -> [Box397,Cut277]
FEATURE [Part::Box] Box422  label="立方体392"
  AttacherType = Attacher::AttachEngine3D
  Height = 4
  Length = 81.6
  Placement = pos=(-75.2,65,0) rot=(0,0,1;0rad)
  Width = 10
FEATURE [Part::Box] Box423  label="立方体393"
  AttacherType = Attacher::AttachEngine3D
  Height = 12
  Length = 25
  Placement = pos=(-75.2,65,0) rot=(0,0,1;0rad)
  Width = 10
FEATURE [Part::Box] Box424  label="立方体394"
  AttacherType = Attacher::AttachEngine3D
  Height = 12
  Length = 25
  Placement = pos=(-18.6,65,0) rot=(0,0,1;0rad)
  Width = 10
FEATURE [Part::Box] Box425  label="立方体395"
  AttacherType = Attacher::AttachEngine3D
  Height = 12
  Length = 10
  Placement = pos=(-60.2,54.6,0) rot=(0,0,1;0rad)
  Width = 20.4
FEATURE [Part::Box] Box426  label="立方体396"
  AttacherType = Attacher::AttachEngine3D
  Height = 12
  Length = 10
  Placement = pos=(-18.6,54.6,0) rot=(0,0,1;0rad)
  Width = 20.4
FEATURE [Part::Cylinder] Cylinder264  label="円柱264"
  Angle = 360
  AttacherType = Attacher::AttachEngine3D
  FirstAngle = 0
  Height = 12
  Placement = pos=(1.4,70,0) rot=(0,0,1;0rad)
  Radius = 2
  SecondAngle = 0
FEATURE [Part::Cylinder] Cylinder265  label="円柱265"
  Angle = 360
  AttacherType = Attacher::AttachEngine3D
  FirstAngle = 0
  Height = 12
  Placement = pos=(-70.2,70,0) rot=(0,0,1;0rad)
  Radius = 2
  SecondAngle = 0
FEATURE [Part::MultiFuse] Fusion269
  Shapes = -> [Box422,Box423,Box424,Box425,Box426]
FEATURE [Part::Fillet] Fillet010
  Base = -> Fusion269
  EdgeLinks = -> Fusion269 [Edge8,Edge10]
  Edges = 2 edges r=4.99: [Edge8,Edge10]
FEATURE [Part::Fillet] Fillet011
  Base = -> Fillet010
  EdgeLinks = -> Fillet010 [Edge88,Edge90]
  Edges = 2 edges r=4.99: [Edge88,Edge90]
FEATURE [Part::Fillet] Fillet012
  Base = -> Fillet011
  EdgeLinks = -> Fillet011 [Edge38,Edge55,Edge73,Edge90]
  Edges = 4 edges r=3: [Edge38,Edge55,Edge73,Edge90]
FEATURE [Part::Fillet] Fillet013
  Base = -> Fillet012
  EdgeLinks = -> Fillet012 [Edge28,Edge48]
  Edges = 2 edges r=2: [Edge28,Edge48]
FEATURE [Part::MultiFuse] Fusion270
  Shapes = -> [Cylinder265,Cylinder264]
FEATURE [Part::Cut] Cut414
  Base = -> Fillet013
  Refine = true
  Tool = -> Fusion270
FEATURE [Part::Feature] Part__Feature588  label="18650 Lipo battery 2"
  Placement = pos=(-90.4,54,72.5) rot=(0,0,1;3.14159rad)
  shape: bbox 19.84 x 64.7 x 19.84 mm, 42 faces (baked)
FEATURE [Part::Feature] Part__Feature589  label="18650 Lipo battery 1"
  Placement = pos=(-71.4,54,72.5) rot=(0,0,1;3.14159rad)
  shape: bbox 19.84 x 64.7 x 19.84 mm, 42 faces (baked)
FEATURE [Part::Feature] Part__Feature057  label="Cut"
  Placement = pos=(-62,-32,63.5) rot=(0,0,1;0rad)
  shape: bbox 10 x 108 x 4 mm, 20 faces (baked)
FEATURE [App::Part] Folder_135  label="Folder 135"
  Origin = -> Origin010
FEATURE [App::Part] Folder_136  label="Folder 136"
  Origin = -> Origin009
FEATURE [App::Part] Folder_155  label="Folder 155"
  Origin = -> Origin058
FEATURE [App::Part] Folder_43  label="Folder 43"
  Origin = -> Origin034
FEATURE [App::Part] Folder_61  label="Folder 61"
  Origin = -> Origin032
FEATURE [App::Part] Folder_96  label="Folder 96"
  Origin = -> Origin031
FEATURE [App::Part] MO_178AB  label="MO-178AB"
  Origin = -> Origin023
FEATURE [App::Part] Folder_114  label="Folder 114"
  Group = -> [MO_178AB]
  Origin = -> Origin024
FEATURE [App::Part] MO_178AB__1_  label="MO-178AB (1)"
  Origin = -> Origin021
FEATURE [App::Part] MO_178AB__2_  label="MO-178AB (2)"
  Origin = -> Origin020
FEATURE [App::Part] Folder_117  label="Folder 117"
  Group = -> [MO_178AB__2_,MO_178AB__1_]
  Origin = -> Origin022
FEATURE [App::Part] MS_012AA  label="MS-012AA"
  Origin = -> Origin018
FEATURE [App::Part] MS_012AA__1_  label="MS-012AA (1)"
  Origin = -> Origin017
FEATURE [App::Part] MS_012AA__2_  label="MS-012AA (2)"
  Origin = -> Origin016
FEATURE [App::Part] Folder_122  label="Folder 122"
  Group = -> [MS_012AA__2_,MS_012AA__1_,MS_012AA]
  Origin = -> Origin019
FEATURE [Part::Feature] Part__Feature590  label="USB-C port"
  shape: bbox 8.941 x 6.871 x 4.224 mm, 515 faces, 16 solids (baked)
FEATURE [Part::Feature] Part__Feature120  label="pcb"
  shape: bbox 85 x 56 x 1.62 mm, 4665 faces (baked)
FEATURE [Part::Feature] Part__Feature130  label="COMPOUND015"
  shape: bbox 64.6 x 55.6 x 0.2 mm, 16 faces, 4 solids (baked)
FEATURE [Part::Feature] Part__Feature131  label="HOUSE (1)"
  shape: bbox 10 x 6 x 7.6 mm, 142 faces (baked)
FEATURE [Part::Feature] Part__Feature132  label="PIN (1)"
  shape: bbox 0.5 x 4.1 x 8.2 mm, 18 faces (baked)
FEATURE [Part::Feature] Part__Feature133  label="PIN (1)001"
  shape: bbox 0.5 x 4.1 x 8.2 mm, 18 faces (baked)
FEATURE [Part::Feature] Part__Feature134  label="FEET (1)"
  shape: bbox 0.35 x 2.55 x 2.9 mm, 6 faces (baked)
FEATURE [Part::Feature] Part__Feature135  label="FEET (1)001"
  shape: bbox 0.35 x 2.55 x 2.9 mm, 6 faces (baked)
FEATURE [Part::Feature] Part__Feature136  label="HOUSE"
  shape: bbox 10 x 6 x 7.6 mm, 142 faces (baked)
FEATURE [Part::Feature] Part__Feature137  label="PIN"
  shape: bbox 0.5 x 4.1 x 8.2 mm, 18 faces (baked)
FEATURE [Part::Feature] Part__Feature138  label="PIN001"
  shape: bbox 0.5 x 4.1 x 8.2 mm, 18 faces (baked)
FEATURE [Part::Feature] Part__Feature139  label="FEET"
  shape: bbox 0.35 x 2.55 x 2.9 mm, 6 faces (baked)
FEATURE [Part::Feature] Part__Feature140  label="FEET001"
  shape: bbox 0.35 x 2.55 x 2.9 mm, 6 faces (baked)
FEATURE [Part::Feature] Part__Feature142  label="mount points"
  shape: bbox 63.5 x 54.5 x 6.12 mm, 16 faces, 4 solids (baked)
FEATURE [Part::Feature] Part__Feature143  label="18650 battery holder"
  shape: bbox 77.5 x 39.6 x 15.33 mm, 76 faces (baked)
FEATURE [Part::Feature] Part__Feature144  label="battery leds"
  shape: bbox 1.6 x 14.7 x 1 mm, 72 faces, 4 solids (baked)
FEATURE [Part::Feature] Part__Feature145  label="power in and power switch"
  shape: bbox 9.85 x 7.5 x 7.5 mm, 8 faces (baked)
FEATURE [App::Part] Resistor_1210
  Origin = -> Origin060
FEATURE [App::Part] Resistor_1210__1_  label="Resistor_1210 (1)"
  Origin = -> Origin059
FEATURE [App::Part] Folder_152  label="Folder 152"
  Group = -> [Resistor_1210__1_,Resistor_1210]
  Origin = -> Origin061
FEATURE [App::Part] SC_88A  label="SC-88A"
  Origin = -> Origin029
FEATURE [App::Part] SC_88A__1_  label="SC-88A (1)"
  Origin = -> Origin028
FEATURE [App::Part] SC_88A__2_  label="SC-88A (2)"
  Origin = -> Origin027
FEATURE [App::Part] SC_88A__3_  label="SC-88A (3)"
  Origin = -> Origin026
FEATURE [App::Part] SC_88A__4_  label="SC-88A (4)"
  Origin = -> Origin025
FEATURE [App::Part] Folder_107  label="Folder 107"
  Group = -> [SC_88A__4_,SC_88A__3_,SC_88A__2_,SC_88A__1_,SC_88A]
  Origin = -> Origin030
FEATURE [App::Part] _r003  label="2r003"
  Origin = -> Origin007
FEATURE [App::Part] _r2  label="2r2"
  Origin = -> Origin062
FEATURE [App::Part] Folder_141  label="Folder 141"
  Group = -> [_r2,_r003]
  Origin = -> Origin008
FEATURE [App::Part] basic_chip  label="basic chip"
  Origin = -> Origin014
FEATURE [App::Part] basic_chip__1_  label="basic chip (1)"
  Origin = -> Origin013
FEATURE [App::Part] basic_chip__2_  label="basic chip (2)"
  Origin = -> Origin011
FEATURE [App::Part] basic_chip__2_001  label="basic chip (2)001"
  Origin = -> Origin012
FEATURE [App::Part] Folder_132  label="Folder 132"
  Group = -> [basic_chip__2_,basic_chip__2_001,basic_chip__1_,basic_chip]
  Origin = -> Origin015
FEATURE [App::Part] battery_side_silk  label="battery side silk"
  Group = -> [Part__Feature130]
  Origin = -> Origin037
FEATURE [App::Part] bits_and_chips  label="bits and chips"
  Group = -> [Folder_155,Folder_152,Folder_141,Folder_136,Folder_135,Folder_132,Folder_122,Folder_117,Folder_114,Folder_107,Folder_96,Folder_61,Folder_43]
  Origin = -> Origin035
FEATURE [App::Part] pi_side_silk  label="pi side silk"
  Origin = -> Origin036
FEATURE [App::Part] xh2_54_2p  label="xh2.54-2p"
  Group = -> [Part__Feature136,Part__Feature137,Part__Feature138,Part__Feature139,Part__Feature140]
  Origin = -> Origin039
FEATURE [App::Part] xh2_54_2p__1_  label="xh2.54-2p (1)"
  Group = -> [Part__Feature131,Part__Feature132,Part__Feature133,Part__Feature134,Part__Feature135]
  Origin = -> Origin038
FEATURE [App::Part] Geekworm_X1200_UPS_HAT  label="Geekworm X1200 UPS HAT"
  Group = -> [Part__Feature590,bits_and_chips,Part__Feature120,pi_side_silk,battery_side_silk,xh2_54_2p__1_,xh2_54_2p,Part__Feature142,Part__Feature143,Part__Feature144,Part__Feature145]
  Origin = -> Origin040
FEATURE [App::Part] X1200
  Group = -> [Geekworm_X1200_UPS_HAT]
  Origin = -> Origin041
  Placement = pos=(-118.9,-50.7,85.87) rot=(0.707107,0.707107,0;3.14159rad)
FEATURE [Part::Feature] Part__Feature641  label="connector"
  Placement = pos=(-70.5,-36,11.75) rot=(0,0,1;0rad)
  shape: bbox 3 x 6 x 3.5 mm, 6 faces (baked)
FEATURE [Part::Feature] Part__Feature642  label="CSI_DSI_connector"
  shape: bbox 3 x 15.5 x 4.1 mm, 24 faces, 2 solids (baked)
FEATURE [App::Part] CSI_DSI_1  label="CSI_DSI-1"
  Group = -> [Part__Feature642]
  Origin = -> Origin076
  Placement = pos=(-70.5,-36,11.75) rot=(0,0,1;0rad)
FEATURE [Part::Feature] Part__Feature643  label="CSI_DSI_connector001"
  Placement = pos=(6.2,0,0) rot=(0,0,1;0rad)
  shape: bbox 3 x 15.5 x 4.1 mm, 24 faces, 2 solids (baked)
FEATURE [App::Part] CSI_DSI_2  label="CSI_DSI-2"
  Group = -> [Part__Feature643]
  Origin = -> Origin077
  Placement = pos=(-70.5,-36,11.75) rot=(0,0,1;0rad)
FEATURE [Part::Feature] Part__Feature644  label="ethernet"
  Placement = pos=(1.39e-14,-35.55,0.8) rot=(1,0,0;1.5708rad)
  shape: bbox 23.65 x 16 x 17.25 mm, 75 faces, 4 solids (baked)
FEATURE [Part::Feature] Part__Feature645  label="gpio"
  Placement = pos=(-70.53,-36.28,11.75) rot=(0,0,1;0rad)
  shape: bbox 50.5 x 5 x 8.29 mm, 286 faces, 41 solids (baked)
FEATURE [Part::Feature] Part__Feature646  label="hdmi-micro"
  Placement = pos=(-0.3,-6.9e-15,0.8) rot=(1,0,0;1.5708rad)
  shape: bbox 6.5 x 7.7 x 2.9 mm, 28 faces, 2 solids (baked)
FEATURE [Part::Feature] Part__Feature647  label="hdmi-micro001"
  Placement = pos=(-13.8,-6.9e-15,0.8) rot=(1,0,0;1.5708rad)
  shape: bbox 6.5 x 7.7 x 2.9 mm, 28 faces, 2 solids (baked)
FEATURE [Part::Feature] Part__Feature648  label="IR"
  Placement = pos=(-70.5,-36,11.75) rot=(0,0,1;0rad)
  shape: bbox 1.734 x 3.15 x 3.26 mm, 8 faces, 2 solids (baked)
FEATURE [Part::Feature] Part__Feature649  label="mounting-holes"
  Placement = pos=(-70.5,-36,11.75) rot=(0,0,1;0rad)
  shape: bbox 64 x 54.91 x 0.02002 mm, 16 faces, 4 solids (baked)
FEATURE [Part::Feature] Part__Feature650  label="pcb001"
  Placement = pos=(-70.5,-36,11.75) rot=(0,0,1;0rad)
  shape: bbox 85 x 56 x 1.6 mm, 22 faces (baked)
FEATURE [Part::Feature] Part__Feature651  label="pcba-components Geometry"
  shape: bbox 62.02 x 39.27 x 3.37 mm, 58 faces, 7 solids (baked)
FEATURE [Part::Feature] Part__Feature652  label="chips"
  shape: bbox 13.6 x 15 x 1 mm, 66 faces, 11 solids (baked)
FEATURE [Part::Feature] Part__Feature653  label="pcie"
  Placement = pos=(-70.5,-36,11.75) rot=(0,0,1;0rad)
  shape: bbox 3 x 10.5 x 4.1 mm, 20 faces, 2 solids (baked)
FEATURE [Part::Feature] Part__Feature654  label="pmic"
  Placement = pos=(-70.5,-36,11.75) rot=(0,0,1;0rad)
  shape: bbox 6 x 6 x 0.5 mm, 6 faces (baked)
FEATURE [Part::Feature] Part__Feature655  label="poe Geometry"
  shape: bbox 5.08 x 5.08 x 1 mm, 6 faces (baked)
FEATURE [Part::Feature] Part__Feature656  label="poe-pins"
  shape: bbox 3.44 x 3.44 x 7.29 mm, 24 faces, 4 solids (baked)
FEATURE [Part::Feature] Part__Feature657  label="pwr-connector"
  Placement = pos=(-70.5,-36,11.75) rot=(0,0,1;0rad)
  shape: bbox 4 x 3 x 4.4 mm, 6 faces (baked)
FEATURE [Part::Feature] Part__Feature658  label="rp1"
  Placement = pos=(-70.5,-36,11.75) rot=(0,0,1;0rad)
  shape: bbox 12 x 12 x 0.5 mm, 6 faces (baked)
FEATURE [Part::Feature] Part__Feature660  label="switch"
  Placement = pos=(-70.5,-36,11.75) rot=(0,0,1;0rad)
  shape: bbox 2.995 x 4.75 x 1.77 mm, 16 faces, 2 solids (baked)
FEATURE [Part::Feature] Part__Feature661  label="uart"
  Placement = pos=(-70.5,-36,11.75) rot=(0,0,1;0rad)
  shape: bbox 5.25 x 3.25 x 4.4 mm, 6 faces (baked)
FEATURE [Part::Feature] Part__Feature662  label="usb-2-bank Geometry"
  shape: bbox 16.67 x 15.5 x 13.76 mm, 6 faces (baked)
FEATURE [Part::Feature] Part__Feature663  label="usb2-port"
  shape: bbox 4.42 x 5.12 x 12.5 mm, 14 faces, 2 solids (baked)
FEATURE [Part::Feature] Part__Feature664  label="usb2-port001"
  Placement = pos=(0,-8.5,0) rot=(0,0,1;0rad)
  shape: bbox 4.42 x 5.12 x 12.5 mm, 14 faces, 2 solids (baked)
FEATURE [Part::Feature] Part__Feature665  label="usb-3-bank Geometry"
  shape: bbox 16.67 x 15.5 x 13.76 mm, 6 faces (baked)
FEATURE [Part::Feature] Part__Feature666  label="usb3-port"
  shape: bbox 4.42 x 5.12 x 12.5 mm, 14 faces, 2 solids (baked)
FEATURE [Part::Feature] Part__Feature667  label="usb3-port001"
  Placement = pos=(0,-8.5,-9e-16) rot=(0,0,1;0rad)
  shape: bbox 4.42 x 5.12 x 12.5 mm, 14 faces, 2 solids (baked)
FEATURE [Part::Feature] Part__Feature668  label="usb-c"
  Placement = pos=(-70.5,-36,11.75) rot=(0,0,1;0rad)
  shape: bbox 9 x 7.5 x 3.2 mm, 10 faces (baked)
FEATURE [App::Part] pcba_components  label="pcba-components"
  Group = -> [Part__Feature651,Part__Feature652]
  Origin = -> Origin078
  Placement = pos=(-70.5,-36,11.75) rot=(0,0,1;0rad)
FEATURE [App::Part] poe
  Group = -> [Part__Feature655,Part__Feature656]
  Origin = -> Origin079
  Placement = pos=(-70.5,-36,11.75) rot=(0,0,1;0rad)
FEATURE [App::Part] usb_2_bank  label="usb-2-bank"
  Group = -> [Part__Feature662,Part__Feature663,Part__Feature664]
  Origin = -> Origin080
  Placement = pos=(-0.744279,20,0.8) rot=(1,0,0;1.5708rad)
FEATURE [App::Part] usb_3_bank  label="usb-3-bank"
  Group = -> [Part__Feature665,Part__Feature666,Part__Feature667]
  Origin = -> Origin081
  Placement = pos=(-0.544279,2.1,0.8) rot=(1,0,0;1.5708rad)
FEATURE [App::Part] raspberry_pi_5_sbc_simple  label="Raspberry pi 5 (simple ver)"
  Group = -> [Part__Feature641,CSI_DSI_1,CSI_DSI_2,Part__Feature644,Part__Feature645,Part__Feature646,Part__Feature647,Part__Feature648,Part__Feature649,Part__Feature650,pcba_components,Part__Feature653,Part__Feature654,poe,Part__Feature657,Part__Feature658,Part__Feature660,Part__Feature661,usb_2_bank,usb_3_bank,Part__Feature668]
  Origin = -> Origin082
  Placement = pos=(-81,24.5,57.4) rot=(0.707107,-0.707107,0;3.14159rad)
FEATURE [App::FeaturePython] DistantLight  # WARN: FeaturePython — macro-defined, semantics opaque (R4)
  Angle = 0
  Direction = (-1,1,-1)
  Power = 88
FEATURE [Part::Feature] Part__Feature602  label="Specer 1"
  Placement = pos=(8,0,0) rot=(0,0,1;0rad)
  shape: bbox 8 x 8 x 32 mm, 4 faces (baked)
FEATURE [Part::Feature] Part__Feature603  label="Specer 2"
  Placement = pos=(-13.9,-15,0) rot=(0,0,1;0rad)
  shape: bbox 8 x 8 x 32 mm, 4 faces (baked)
FEATURE [Part::Feature] Part__Feature604  label="Specer 3"
  Placement = pos=(-8.2,0,0) rot=(0,0,1;0rad)
  shape: bbox 8 x 8 x 32 mm, 4 faces (baked)
FEATURE [Part::Feature] Part__Feature605  label="Specer 4"
  Placement = pos=(14.1,-15,0) rot=(0,0,1;0rad)
  shape: bbox 8 x 8 x 32 mm, 4 faces (baked)
FEATURE [App::Part] Chassis_Spacer  label="Chassis Spacer"
  Group = -> [Part__Feature602,Part__Feature603,Part__Feature604,Part__Feature605]
  Origin = -> Origin064
